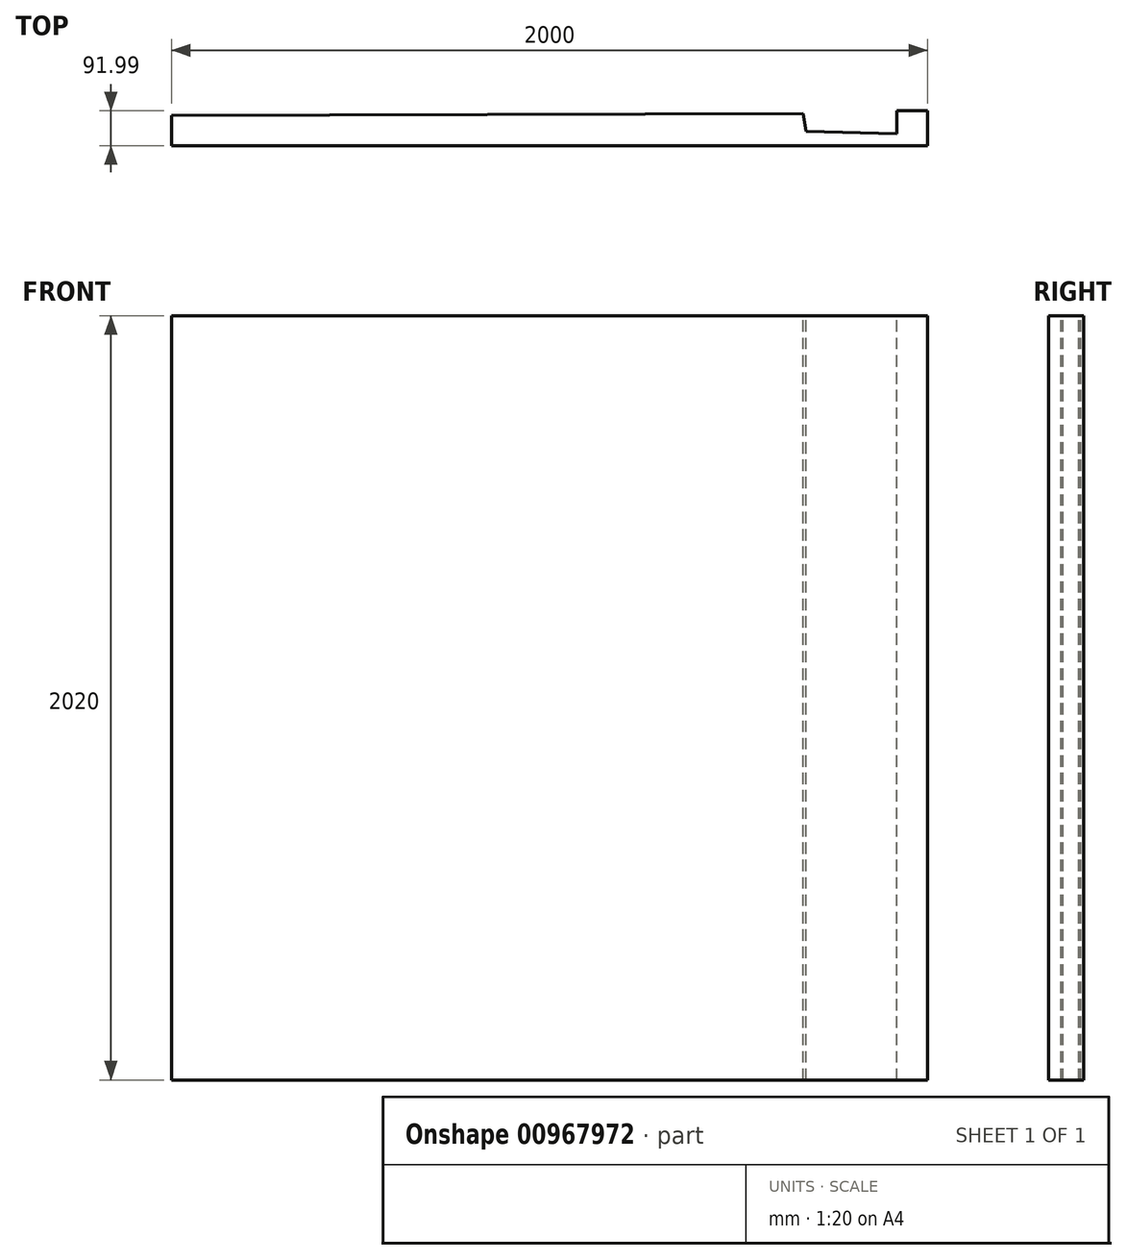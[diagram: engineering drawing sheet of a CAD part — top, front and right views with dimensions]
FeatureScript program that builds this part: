
annotation { "Feature Type Name" : "Feature", "Feature Type Description" : "" }
export const myFeature = defineFeature(function(context is Context, id is Id, definition is map)
    precondition{}
    {
        {
            var Q0;
            Q0=qCreatedBy(makeId("Front.planeOp"),FACE);
            var sketch = newSketch(context, id + "F0", { "sketchPlane" : qUnion([Q0])});
            skLineSegment(sketch, "E0.bottom", {"start": v(-1953.33, 1210) * mm, "end": v(46.67, 1210) * mm});
            skLineSegment(sketch, "E0.top", {"start": v(-1953.33, -810) * mm, "end": v(46.67, -810) * mm});
            skLineSegment(sketch, "E0.left", {"start": v(-1953.33, 1210) * mm, "end": v(-1953.33, -810) * mm});
            skLineSegment(sketch, "E0.right", {"start": v(46.67, 1210) * mm, "end": v(46.67, -810) * mm});
            skLineSegment(sketch, "E1.top", {"start": v(-1953.33, -870) * mm, "end": v(46.67, -870) * mm});
            skLineSegment(sketch, "E1.left", {"start": v(-1953.33, -810) * mm, "end": v(-1953.33, -870) * mm});
            skLineSegment(sketch, "E1.right", {"start": v(46.67, -810) * mm, "end": v(46.67, -870) * mm});
            skLineSegment(sketch, "E2.bottom", {"start": v(46.67, -870) * mm, "end": v(906.67, -870) * mm});
            skLineSegment(sketch, "E2.top", {"start": v(46.67, 1230) * mm, "end": v(906.67, 1230) * mm});
            skLineSegment(sketch, "E2.left", {"start": v(46.67, -870) * mm, "end": v(46.67, 1230) * mm});
            skLineSegment(sketch, "E2.right", {"start": v(906.67, -870) * mm, "end": v(906.67, 1230) * mm});
            skLineSegment(sketch, "E3.bottom", {"start": v(906.67, -870) * mm, "end": v(1451.67, -870) * mm});
            skLineSegment(sketch, "E3.top", {"start": v(906.67, 1210) * mm, "end": v(1451.67, 1210) * mm});
            skLineSegment(sketch, "E3.left", {"start": v(906.67, -870) * mm, "end": v(906.67, 1210) * mm});
            skLineSegment(sketch, "E3.right", {"start": v(1451.67, -870) * mm, "end": v(1451.67, 1210) * mm});
            skLineSegment(sketch, "E4.bottom", {"start": v(1451.67, 1210) * mm, "end": v(2111.67, 1210) * mm});
            skLineSegment(sketch, "E4.top", {"start": v(1451.67, 0) * mm, "end": v(2111.67, 0) * mm});
            skLineSegment(sketch, "E4.left", {"start": v(1451.67, 1210) * mm, "end": v(1451.67, 0) * mm});
            skLineSegment(sketch, "E4.right", {"start": v(2111.67, 1210) * mm, "end": v(2111.67, 0) * mm});
            skLineSegment(sketch, "E5.bottom", {"start": v(2111.67, 0) * mm, "end": v(3431.67, 0) * mm});
            skLineSegment(sketch, "E5.top", {"start": v(2111.67, 1210) * mm, "end": v(3431.67, 1210) * mm});
            skLineSegment(sketch, "E5.left", {"start": v(2111.67, 0) * mm, "end": v(2111.67, 1210) * mm});
            skLineSegment(sketch, "E5.right", {"start": v(3431.67, 0) * mm, "end": v(3431.67, 1210) * mm});
            skLineSegment(sketch, "E6.bottom", {"start": v(3431.67, 0) * mm, "end": v(3871.67, 0) * mm});
            skLineSegment(sketch, "E6.top", {"start": v(3431.67, 1210) * mm, "end": v(3871.67, 1210) * mm});
            skLineSegment(sketch, "E6.right", {"start": v(3871.67, 0) * mm, "end": v(3871.67, 1210) * mm});
            skSolve(sketch);
        }
        {
            var Q0;
            {var subQ0=sQuery(id+"F0.wireOp",EDGE,"E0.bottom");Q0=makeQuery(id+"F0.imprint","IMPRINT",FACE,{"disambiguationData":[TD([[makeQuery(id+"F0.imprint","IMPRINT",EDGE,{"derivedFrom":subQ0}),-1.0]])]});}
            var sketch = newSketch(context, id + "F1", { "sketchPlane" : qUnion([Q0])});
            skLineSegment(sketch, "E7.bottom", {"start": v(-1953.33, 1210) * mm, "end": v(-1799.33, 1210) * mm});
            skLineSegment(sketch, "E7.top", {"start": v(-1953.33, 1056) * mm, "end": v(-1799.33, 1056) * mm});
            skLineSegment(sketch, "E7.left", {"start": v(-1953.33, 1210) * mm, "end": v(-1953.33, 1056) * mm});
            skLineSegment(sketch, "E7.right", {"start": v(-1799.33, 1210) * mm, "end": v(-1799.33, 1056) * mm});
            skLineSegment(sketch, "E8.0.1.0", {"start": v(-1953.33, 1054) * mm, "end": v(-1799.33, 1054) * mm});
            skLineSegment(sketch, "E8.0.1.1", {"start": v(-1799.33, 1054) * mm, "end": v(-1799.33, 900) * mm});
            skLineSegment(sketch, "E8.0.1.2", {"start": v(-1953.33, 900) * mm, "end": v(-1799.33, 900) * mm});
            skLineSegment(sketch, "E8.0.1.3", {"start": v(-1953.33, 1054) * mm, "end": v(-1953.33, 900) * mm});
            skLineSegment(sketch, "E8.0.2.0", {"start": v(-1953.33, 898) * mm, "end": v(-1799.33, 898) * mm});
            skLineSegment(sketch, "E8.0.2.1", {"start": v(-1799.33, 898) * mm, "end": v(-1799.33, 744) * mm});
            skLineSegment(sketch, "E8.0.2.2", {"start": v(-1953.33, 744) * mm, "end": v(-1799.33, 744) * mm});
            skLineSegment(sketch, "E8.0.2.3", {"start": v(-1953.33, 898) * mm, "end": v(-1953.33, 744) * mm});
            skLineSegment(sketch, "E8.0.3.0", {"start": v(-1953.33, 742) * mm, "end": v(-1799.33, 742) * mm});
            skLineSegment(sketch, "E8.0.3.1", {"start": v(-1799.33, 742) * mm, "end": v(-1799.33, 588) * mm});
            skLineSegment(sketch, "E8.0.3.2", {"start": v(-1953.33, 588) * mm, "end": v(-1799.33, 588) * mm});
            skLineSegment(sketch, "E8.0.3.3", {"start": v(-1953.33, 742) * mm, "end": v(-1953.33, 588) * mm});
            skLineSegment(sketch, "E8.0.4.0", {"start": v(-1953.33, 586) * mm, "end": v(-1799.33, 586) * mm});
            skLineSegment(sketch, "E8.0.4.1", {"start": v(-1799.33, 586) * mm, "end": v(-1799.33, 432) * mm});
            skLineSegment(sketch, "E8.0.4.2", {"start": v(-1953.33, 432) * mm, "end": v(-1799.33, 432) * mm});
            skLineSegment(sketch, "E8.0.4.3", {"start": v(-1953.33, 586) * mm, "end": v(-1953.33, 432) * mm});
            skLineSegment(sketch, "E8.0.5.0", {"start": v(-1953.33, 430) * mm, "end": v(-1799.33, 430) * mm});
            skLineSegment(sketch, "E8.0.5.1", {"start": v(-1799.33, 430) * mm, "end": v(-1799.33, 276) * mm});
            skLineSegment(sketch, "E8.0.5.2", {"start": v(-1953.33, 276) * mm, "end": v(-1799.33, 276) * mm});
            skLineSegment(sketch, "E8.0.5.3", {"start": v(-1953.33, 430) * mm, "end": v(-1953.33, 276) * mm});
            skLineSegment(sketch, "E8.0.6.0", {"start": v(-1953.33, 274) * mm, "end": v(-1799.33, 274) * mm});
            skLineSegment(sketch, "E8.0.6.1", {"start": v(-1799.33, 274) * mm, "end": v(-1799.33, 120) * mm});
            skLineSegment(sketch, "E8.0.6.2", {"start": v(-1953.33, 120) * mm, "end": v(-1799.33, 120) * mm});
            skLineSegment(sketch, "E8.0.6.3", {"start": v(-1953.33, 274) * mm, "end": v(-1953.33, 120) * mm});
            skLineSegment(sketch, "E8.0.7.0", {"start": v(-1953.33, 118) * mm, "end": v(-1799.33, 118) * mm});
            skLineSegment(sketch, "E8.0.7.1", {"start": v(-1799.33, 118) * mm, "end": v(-1799.33, -36) * mm});
            skLineSegment(sketch, "E8.0.7.2", {"start": v(-1953.33, -36) * mm, "end": v(-1799.33, -36) * mm});
            skLineSegment(sketch, "E8.0.7.3", {"start": v(-1953.33, 118) * mm, "end": v(-1953.33, -36) * mm});
            skLineSegment(sketch, "E8.0.8.0", {"start": v(-1953.33, -38) * mm, "end": v(-1799.33, -38) * mm});
            skLineSegment(sketch, "E8.0.8.1", {"start": v(-1799.33, -38) * mm, "end": v(-1799.33, -192) * mm});
            skLineSegment(sketch, "E8.0.8.2", {"start": v(-1953.33, -192) * mm, "end": v(-1799.33, -192) * mm});
            skLineSegment(sketch, "E8.0.8.3", {"start": v(-1953.33, -38) * mm, "end": v(-1953.33, -192) * mm});
            skLineSegment(sketch, "E8.0.9.0", {"start": v(-1953.33, -194) * mm, "end": v(-1799.33, -194) * mm});
            skLineSegment(sketch, "E8.0.9.1", {"start": v(-1799.33, -194) * mm, "end": v(-1799.33, -348) * mm});
            skLineSegment(sketch, "E8.0.9.2", {"start": v(-1953.33, -348) * mm, "end": v(-1799.33, -348) * mm});
            skLineSegment(sketch, "E8.0.9.3", {"start": v(-1953.33, -194) * mm, "end": v(-1953.33, -348) * mm});
            skLineSegment(sketch, "E8.0.10.0", {"start": v(-1953.33, -350) * mm, "end": v(-1799.33, -350) * mm});
            skLineSegment(sketch, "E8.0.10.1", {"start": v(-1799.33, -350) * mm, "end": v(-1799.33, -504) * mm});
            skLineSegment(sketch, "E8.0.10.2", {"start": v(-1953.33, -504) * mm, "end": v(-1799.33, -504) * mm});
            skLineSegment(sketch, "E8.0.10.3", {"start": v(-1953.33, -350) * mm, "end": v(-1953.33, -504) * mm});
            skLineSegment(sketch, "E8.0.11.0", {"start": v(-1953.33, -506) * mm, "end": v(-1799.33, -506) * mm});
            skLineSegment(sketch, "E8.0.11.1", {"start": v(-1799.33, -506) * mm, "end": v(-1799.33, -660) * mm});
            skLineSegment(sketch, "E8.0.11.2", {"start": v(-1953.33, -660) * mm, "end": v(-1799.33, -660) * mm});
            skLineSegment(sketch, "E8.0.11.3", {"start": v(-1953.33, -506) * mm, "end": v(-1953.33, -660) * mm});
            skLineSegment(sketch, "E8.0.12.0", {"start": v(-1953.33, -662) * mm, "end": v(-1799.33, -662) * mm});
            skLineSegment(sketch, "E8.0.12.1", {"start": v(-1799.33, -662) * mm, "end": v(-1799.33, -816) * mm});
            skLineSegment(sketch, "E8.0.12.2", {"start": v(-1953.33, -816) * mm, "end": v(-1799.33, -816) * mm});
            skLineSegment(sketch, "E8.0.12.3", {"start": v(-1953.33, -662) * mm, "end": v(-1953.33, -816) * mm});
            skLineSegment(sketch, "E8.1.0.0", {"start": v(-1797.33, 1210) * mm, "end": v(-1643.33, 1210) * mm});
            skLineSegment(sketch, "E8.1.0.1", {"start": v(-1643.33, 1210) * mm, "end": v(-1643.33, 1056) * mm});
            skLineSegment(sketch, "E8.1.0.2", {"start": v(-1797.33, 1056) * mm, "end": v(-1643.33, 1056) * mm});
            skLineSegment(sketch, "E8.1.0.3", {"start": v(-1797.33, 1210) * mm, "end": v(-1797.33, 1056) * mm});
            skLineSegment(sketch, "E8.1.1.0", {"start": v(-1797.33, 1054) * mm, "end": v(-1643.33, 1054) * mm});
            skLineSegment(sketch, "E8.1.1.1", {"start": v(-1643.33, 1054) * mm, "end": v(-1643.33, 900) * mm});
            skLineSegment(sketch, "E8.1.1.2", {"start": v(-1797.33, 900) * mm, "end": v(-1643.33, 900) * mm});
            skLineSegment(sketch, "E8.1.1.3", {"start": v(-1797.33, 1054) * mm, "end": v(-1797.33, 900) * mm});
            skLineSegment(sketch, "E8.1.2.0", {"start": v(-1797.33, 898) * mm, "end": v(-1643.33, 898) * mm});
            skLineSegment(sketch, "E8.1.2.1", {"start": v(-1643.33, 898) * mm, "end": v(-1643.33, 744) * mm});
            skLineSegment(sketch, "E8.1.2.2", {"start": v(-1797.33, 744) * mm, "end": v(-1643.33, 744) * mm});
            skLineSegment(sketch, "E8.1.2.3", {"start": v(-1797.33, 898) * mm, "end": v(-1797.33, 744) * mm});
            skLineSegment(sketch, "E8.1.3.0", {"start": v(-1797.33, 742) * mm, "end": v(-1643.33, 742) * mm});
            skLineSegment(sketch, "E8.1.3.1", {"start": v(-1643.33, 742) * mm, "end": v(-1643.33, 588) * mm});
            skLineSegment(sketch, "E8.1.3.2", {"start": v(-1797.33, 588) * mm, "end": v(-1643.33, 588) * mm});
            skLineSegment(sketch, "E8.1.3.3", {"start": v(-1797.33, 742) * mm, "end": v(-1797.33, 588) * mm});
            skLineSegment(sketch, "E8.1.4.0", {"start": v(-1797.33, 586) * mm, "end": v(-1643.33, 586) * mm});
            skLineSegment(sketch, "E8.1.4.1", {"start": v(-1643.33, 586) * mm, "end": v(-1643.33, 432) * mm});
            skLineSegment(sketch, "E8.1.4.2", {"start": v(-1797.33, 432) * mm, "end": v(-1643.33, 432) * mm});
            skLineSegment(sketch, "E8.1.4.3", {"start": v(-1797.33, 586) * mm, "end": v(-1797.33, 432) * mm});
            skLineSegment(sketch, "E8.1.5.0", {"start": v(-1797.33, 430) * mm, "end": v(-1643.33, 430) * mm});
            skLineSegment(sketch, "E8.1.5.1", {"start": v(-1643.33, 430) * mm, "end": v(-1643.33, 276) * mm});
            skLineSegment(sketch, "E8.1.5.2", {"start": v(-1797.33, 276) * mm, "end": v(-1643.33, 276) * mm});
            skLineSegment(sketch, "E8.1.5.3", {"start": v(-1797.33, 430) * mm, "end": v(-1797.33, 276) * mm});
            skLineSegment(sketch, "E8.1.6.0", {"start": v(-1797.33, 274) * mm, "end": v(-1643.33, 274) * mm});
            skLineSegment(sketch, "E8.1.6.1", {"start": v(-1643.33, 274) * mm, "end": v(-1643.33, 120) * mm});
            skLineSegment(sketch, "E8.1.6.2", {"start": v(-1797.33, 120) * mm, "end": v(-1643.33, 120) * mm});
            skLineSegment(sketch, "E8.1.6.3", {"start": v(-1797.33, 274) * mm, "end": v(-1797.33, 120) * mm});
            skLineSegment(sketch, "E8.1.7.0", {"start": v(-1797.33, 118) * mm, "end": v(-1643.33, 118) * mm});
            skLineSegment(sketch, "E8.1.7.1", {"start": v(-1643.33, 118) * mm, "end": v(-1643.33, -36) * mm});
            skLineSegment(sketch, "E8.1.7.2", {"start": v(-1797.33, -36) * mm, "end": v(-1643.33, -36) * mm});
            skLineSegment(sketch, "E8.1.7.3", {"start": v(-1797.33, 118) * mm, "end": v(-1797.33, -36) * mm});
            skLineSegment(sketch, "E8.1.8.0", {"start": v(-1797.33, -38) * mm, "end": v(-1643.33, -38) * mm});
            skLineSegment(sketch, "E8.1.8.1", {"start": v(-1643.33, -38) * mm, "end": v(-1643.33, -192) * mm});
            skLineSegment(sketch, "E8.1.8.2", {"start": v(-1797.33, -192) * mm, "end": v(-1643.33, -192) * mm});
            skLineSegment(sketch, "E8.1.8.3", {"start": v(-1797.33, -38) * mm, "end": v(-1797.33, -192) * mm});
            skLineSegment(sketch, "E8.1.9.0", {"start": v(-1797.33, -194) * mm, "end": v(-1643.33, -194) * mm});
            skLineSegment(sketch, "E8.1.9.1", {"start": v(-1643.33, -194) * mm, "end": v(-1643.33, -348) * mm});
            skLineSegment(sketch, "E8.1.9.2", {"start": v(-1797.33, -348) * mm, "end": v(-1643.33, -348) * mm});
            skLineSegment(sketch, "E8.1.9.3", {"start": v(-1797.33, -194) * mm, "end": v(-1797.33, -348) * mm});
            skLineSegment(sketch, "E8.1.10.0", {"start": v(-1797.33, -350) * mm, "end": v(-1643.33, -350) * mm});
            skLineSegment(sketch, "E8.1.10.1", {"start": v(-1643.33, -350) * mm, "end": v(-1643.33, -504) * mm});
            skLineSegment(sketch, "E8.1.10.2", {"start": v(-1797.33, -504) * mm, "end": v(-1643.33, -504) * mm});
            skLineSegment(sketch, "E8.1.10.3", {"start": v(-1797.33, -350) * mm, "end": v(-1797.33, -504) * mm});
            skLineSegment(sketch, "E8.1.11.0", {"start": v(-1797.33, -506) * mm, "end": v(-1643.33, -506) * mm});
            skLineSegment(sketch, "E8.1.11.1", {"start": v(-1643.33, -506) * mm, "end": v(-1643.33, -660) * mm});
            skLineSegment(sketch, "E8.1.11.2", {"start": v(-1797.33, -660) * mm, "end": v(-1643.33, -660) * mm});
            skLineSegment(sketch, "E8.1.11.3", {"start": v(-1797.33, -506) * mm, "end": v(-1797.33, -660) * mm});
            skLineSegment(sketch, "E8.1.12.0", {"start": v(-1797.33, -662) * mm, "end": v(-1643.33, -662) * mm});
            skLineSegment(sketch, "E8.1.12.1", {"start": v(-1643.33, -662) * mm, "end": v(-1643.33, -816) * mm});
            skLineSegment(sketch, "E8.1.12.2", {"start": v(-1797.33, -816) * mm, "end": v(-1643.33, -816) * mm});
            skLineSegment(sketch, "E8.1.12.3", {"start": v(-1797.33, -662) * mm, "end": v(-1797.33, -816) * mm});
            skLineSegment(sketch, "E8.2.0.0", {"start": v(-1641.33, 1210) * mm, "end": v(-1487.33, 1210) * mm});
            skLineSegment(sketch, "E8.2.0.1", {"start": v(-1487.33, 1210) * mm, "end": v(-1487.33, 1056) * mm});
            skLineSegment(sketch, "E8.2.0.2", {"start": v(-1641.33, 1056) * mm, "end": v(-1487.33, 1056) * mm});
            skLineSegment(sketch, "E8.2.0.3", {"start": v(-1641.33, 1210) * mm, "end": v(-1641.33, 1056) * mm});
            skLineSegment(sketch, "E8.2.1.0", {"start": v(-1641.33, 1054) * mm, "end": v(-1487.33, 1054) * mm});
            skLineSegment(sketch, "E8.2.1.1", {"start": v(-1487.33, 1054) * mm, "end": v(-1487.33, 900) * mm});
            skLineSegment(sketch, "E8.2.1.2", {"start": v(-1641.33, 900) * mm, "end": v(-1487.33, 900) * mm});
            skLineSegment(sketch, "E8.2.1.3", {"start": v(-1641.33, 1054) * mm, "end": v(-1641.33, 900) * mm});
            skLineSegment(sketch, "E8.2.2.0", {"start": v(-1641.33, 898) * mm, "end": v(-1487.33, 898) * mm});
            skLineSegment(sketch, "E8.2.2.1", {"start": v(-1487.33, 898) * mm, "end": v(-1487.33, 744) * mm});
            skLineSegment(sketch, "E8.2.2.2", {"start": v(-1641.33, 744) * mm, "end": v(-1487.33, 744) * mm});
            skLineSegment(sketch, "E8.2.2.3", {"start": v(-1641.33, 898) * mm, "end": v(-1641.33, 744) * mm});
            skLineSegment(sketch, "E8.2.3.0", {"start": v(-1641.33, 742) * mm, "end": v(-1487.33, 742) * mm});
            skLineSegment(sketch, "E8.2.3.1", {"start": v(-1487.33, 742) * mm, "end": v(-1487.33, 588) * mm});
            skLineSegment(sketch, "E8.2.3.2", {"start": v(-1641.33, 588) * mm, "end": v(-1487.33, 588) * mm});
            skLineSegment(sketch, "E8.2.3.3", {"start": v(-1641.33, 742) * mm, "end": v(-1641.33, 588) * mm});
            skLineSegment(sketch, "E8.2.4.0", {"start": v(-1641.33, 586) * mm, "end": v(-1487.33, 586) * mm});
            skLineSegment(sketch, "E8.2.4.1", {"start": v(-1487.33, 586) * mm, "end": v(-1487.33, 432) * mm});
            skLineSegment(sketch, "E8.2.4.2", {"start": v(-1641.33, 432) * mm, "end": v(-1487.33, 432) * mm});
            skLineSegment(sketch, "E8.2.4.3", {"start": v(-1641.33, 586) * mm, "end": v(-1641.33, 432) * mm});
            skLineSegment(sketch, "E8.2.5.0", {"start": v(-1641.33, 430) * mm, "end": v(-1487.33, 430) * mm});
            skLineSegment(sketch, "E8.2.5.1", {"start": v(-1487.33, 430) * mm, "end": v(-1487.33, 276) * mm});
            skLineSegment(sketch, "E8.2.5.2", {"start": v(-1641.33, 276) * mm, "end": v(-1487.33, 276) * mm});
            skLineSegment(sketch, "E8.2.5.3", {"start": v(-1641.33, 430) * mm, "end": v(-1641.33, 276) * mm});
            skLineSegment(sketch, "E8.2.6.0", {"start": v(-1641.33, 274) * mm, "end": v(-1487.33, 274) * mm});
            skLineSegment(sketch, "E8.2.6.1", {"start": v(-1487.33, 274) * mm, "end": v(-1487.33, 120) * mm});
            skLineSegment(sketch, "E8.2.6.2", {"start": v(-1641.33, 120) * mm, "end": v(-1487.33, 120) * mm});
            skLineSegment(sketch, "E8.2.6.3", {"start": v(-1641.33, 274) * mm, "end": v(-1641.33, 120) * mm});
            skLineSegment(sketch, "E8.2.7.0", {"start": v(-1641.33, 118) * mm, "end": v(-1487.33, 118) * mm});
            skLineSegment(sketch, "E8.2.7.1", {"start": v(-1487.33, 118) * mm, "end": v(-1487.33, -36) * mm});
            skLineSegment(sketch, "E8.2.7.2", {"start": v(-1641.33, -36) * mm, "end": v(-1487.33, -36) * mm});
            skLineSegment(sketch, "E8.2.7.3", {"start": v(-1641.33, 118) * mm, "end": v(-1641.33, -36) * mm});
            skLineSegment(sketch, "E8.2.8.0", {"start": v(-1641.33, -38) * mm, "end": v(-1487.33, -38) * mm});
            skLineSegment(sketch, "E8.2.8.1", {"start": v(-1487.33, -38) * mm, "end": v(-1487.33, -192) * mm});
            skLineSegment(sketch, "E8.2.8.2", {"start": v(-1641.33, -192) * mm, "end": v(-1487.33, -192) * mm});
            skLineSegment(sketch, "E8.2.8.3", {"start": v(-1641.33, -38) * mm, "end": v(-1641.33, -192) * mm});
            skLineSegment(sketch, "E8.2.9.0", {"start": v(-1641.33, -194) * mm, "end": v(-1487.33, -194) * mm});
            skLineSegment(sketch, "E8.2.9.1", {"start": v(-1487.33, -194) * mm, "end": v(-1487.33, -348) * mm});
            skLineSegment(sketch, "E8.2.9.2", {"start": v(-1641.33, -348) * mm, "end": v(-1487.33, -348) * mm});
            skLineSegment(sketch, "E8.2.9.3", {"start": v(-1641.33, -194) * mm, "end": v(-1641.33, -348) * mm});
            skLineSegment(sketch, "E8.2.10.0", {"start": v(-1641.33, -350) * mm, "end": v(-1487.33, -350) * mm});
            skLineSegment(sketch, "E8.2.10.1", {"start": v(-1487.33, -350) * mm, "end": v(-1487.33, -504) * mm});
            skLineSegment(sketch, "E8.2.10.2", {"start": v(-1641.33, -504) * mm, "end": v(-1487.33, -504) * mm});
            skLineSegment(sketch, "E8.2.10.3", {"start": v(-1641.33, -350) * mm, "end": v(-1641.33, -504) * mm});
            skLineSegment(sketch, "E8.2.11.0", {"start": v(-1641.33, -506) * mm, "end": v(-1487.33, -506) * mm});
            skLineSegment(sketch, "E8.2.11.1", {"start": v(-1487.33, -506) * mm, "end": v(-1487.33, -660) * mm});
            skLineSegment(sketch, "E8.2.11.2", {"start": v(-1641.33, -660) * mm, "end": v(-1487.33, -660) * mm});
            skLineSegment(sketch, "E8.2.11.3", {"start": v(-1641.33, -506) * mm, "end": v(-1641.33, -660) * mm});
            skLineSegment(sketch, "E8.2.12.0", {"start": v(-1641.33, -662) * mm, "end": v(-1487.33, -662) * mm});
            skLineSegment(sketch, "E8.2.12.1", {"start": v(-1487.33, -662) * mm, "end": v(-1487.33, -816) * mm});
            skLineSegment(sketch, "E8.2.12.2", {"start": v(-1641.33, -816) * mm, "end": v(-1487.33, -816) * mm});
            skLineSegment(sketch, "E8.2.12.3", {"start": v(-1641.33, -662) * mm, "end": v(-1641.33, -816) * mm});
            skLineSegment(sketch, "E8.3.0.0", {"start": v(-1485.33, 1210) * mm, "end": v(-1331.33, 1210) * mm});
            skLineSegment(sketch, "E8.3.0.1", {"start": v(-1331.33, 1210) * mm, "end": v(-1331.33, 1056) * mm});
            skLineSegment(sketch, "E8.3.0.2", {"start": v(-1485.33, 1056) * mm, "end": v(-1331.33, 1056) * mm});
            skLineSegment(sketch, "E8.3.0.3", {"start": v(-1485.33, 1210) * mm, "end": v(-1485.33, 1056) * mm});
            skLineSegment(sketch, "E8.3.1.0", {"start": v(-1485.33, 1054) * mm, "end": v(-1331.33, 1054) * mm});
            skLineSegment(sketch, "E8.3.1.1", {"start": v(-1331.33, 1054) * mm, "end": v(-1331.33, 900) * mm});
            skLineSegment(sketch, "E8.3.1.2", {"start": v(-1485.33, 900) * mm, "end": v(-1331.33, 900) * mm});
            skLineSegment(sketch, "E8.3.1.3", {"start": v(-1485.33, 1054) * mm, "end": v(-1485.33, 900) * mm});
            skLineSegment(sketch, "E8.3.2.0", {"start": v(-1485.33, 898) * mm, "end": v(-1331.33, 898) * mm});
            skLineSegment(sketch, "E8.3.2.1", {"start": v(-1331.33, 898) * mm, "end": v(-1331.33, 744) * mm});
            skLineSegment(sketch, "E8.3.2.2", {"start": v(-1485.33, 744) * mm, "end": v(-1331.33, 744) * mm});
            skLineSegment(sketch, "E8.3.2.3", {"start": v(-1485.33, 898) * mm, "end": v(-1485.33, 744) * mm});
            skLineSegment(sketch, "E8.3.3.0", {"start": v(-1485.33, 742) * mm, "end": v(-1331.33, 742) * mm});
            skLineSegment(sketch, "E8.3.3.1", {"start": v(-1331.33, 742) * mm, "end": v(-1331.33, 588) * mm});
            skLineSegment(sketch, "E8.3.3.2", {"start": v(-1485.33, 588) * mm, "end": v(-1331.33, 588) * mm});
            skLineSegment(sketch, "E8.3.3.3", {"start": v(-1485.33, 742) * mm, "end": v(-1485.33, 588) * mm});
            skLineSegment(sketch, "E8.3.4.0", {"start": v(-1485.33, 586) * mm, "end": v(-1331.33, 586) * mm});
            skLineSegment(sketch, "E8.3.4.1", {"start": v(-1331.33, 586) * mm, "end": v(-1331.33, 432) * mm});
            skLineSegment(sketch, "E8.3.4.2", {"start": v(-1485.33, 432) * mm, "end": v(-1331.33, 432) * mm});
            skLineSegment(sketch, "E8.3.4.3", {"start": v(-1485.33, 586) * mm, "end": v(-1485.33, 432) * mm});
            skLineSegment(sketch, "E8.3.5.0", {"start": v(-1485.33, 430) * mm, "end": v(-1331.33, 430) * mm});
            skLineSegment(sketch, "E8.3.5.1", {"start": v(-1331.33, 430) * mm, "end": v(-1331.33, 276) * mm});
            skLineSegment(sketch, "E8.3.5.2", {"start": v(-1485.33, 276) * mm, "end": v(-1331.33, 276) * mm});
            skLineSegment(sketch, "E8.3.5.3", {"start": v(-1485.33, 430) * mm, "end": v(-1485.33, 276) * mm});
            skLineSegment(sketch, "E8.3.6.0", {"start": v(-1485.33, 274) * mm, "end": v(-1331.33, 274) * mm});
            skLineSegment(sketch, "E8.3.6.1", {"start": v(-1331.33, 274) * mm, "end": v(-1331.33, 120) * mm});
            skLineSegment(sketch, "E8.3.6.2", {"start": v(-1485.33, 120) * mm, "end": v(-1331.33, 120) * mm});
            skLineSegment(sketch, "E8.3.6.3", {"start": v(-1485.33, 274) * mm, "end": v(-1485.33, 120) * mm});
            skLineSegment(sketch, "E8.3.7.0", {"start": v(-1485.33, 118) * mm, "end": v(-1331.33, 118) * mm});
            skLineSegment(sketch, "E8.3.7.1", {"start": v(-1331.33, 118) * mm, "end": v(-1331.33, -36) * mm});
            skLineSegment(sketch, "E8.3.7.2", {"start": v(-1485.33, -36) * mm, "end": v(-1331.33, -36) * mm});
            skLineSegment(sketch, "E8.3.7.3", {"start": v(-1485.33, 118) * mm, "end": v(-1485.33, -36) * mm});
            skLineSegment(sketch, "E8.3.8.0", {"start": v(-1485.33, -38) * mm, "end": v(-1331.33, -38) * mm});
            skLineSegment(sketch, "E8.3.8.1", {"start": v(-1331.33, -38) * mm, "end": v(-1331.33, -192) * mm});
            skLineSegment(sketch, "E8.3.8.2", {"start": v(-1485.33, -192) * mm, "end": v(-1331.33, -192) * mm});
            skLineSegment(sketch, "E8.3.8.3", {"start": v(-1485.33, -38) * mm, "end": v(-1485.33, -192) * mm});
            skLineSegment(sketch, "E8.3.9.0", {"start": v(-1485.33, -194) * mm, "end": v(-1331.33, -194) * mm});
            skLineSegment(sketch, "E8.3.9.1", {"start": v(-1331.33, -194) * mm, "end": v(-1331.33, -348) * mm});
            skLineSegment(sketch, "E8.3.9.2", {"start": v(-1485.33, -348) * mm, "end": v(-1331.33, -348) * mm});
            skLineSegment(sketch, "E8.3.9.3", {"start": v(-1485.33, -194) * mm, "end": v(-1485.33, -348) * mm});
            skLineSegment(sketch, "E8.3.10.0", {"start": v(-1485.33, -350) * mm, "end": v(-1331.33, -350) * mm});
            skLineSegment(sketch, "E8.3.10.1", {"start": v(-1331.33, -350) * mm, "end": v(-1331.33, -504) * mm});
            skLineSegment(sketch, "E8.3.10.2", {"start": v(-1485.33, -504) * mm, "end": v(-1331.33, -504) * mm});
            skLineSegment(sketch, "E8.3.10.3", {"start": v(-1485.33, -350) * mm, "end": v(-1485.33, -504) * mm});
            skLineSegment(sketch, "E8.3.11.0", {"start": v(-1485.33, -506) * mm, "end": v(-1331.33, -506) * mm});
            skLineSegment(sketch, "E8.3.11.1", {"start": v(-1331.33, -506) * mm, "end": v(-1331.33, -660) * mm});
            skLineSegment(sketch, "E8.3.11.2", {"start": v(-1485.33, -660) * mm, "end": v(-1331.33, -660) * mm});
            skLineSegment(sketch, "E8.3.11.3", {"start": v(-1485.33, -506) * mm, "end": v(-1485.33, -660) * mm});
            skLineSegment(sketch, "E8.3.12.0", {"start": v(-1485.33, -662) * mm, "end": v(-1331.33, -662) * mm});
            skLineSegment(sketch, "E8.3.12.1", {"start": v(-1331.33, -662) * mm, "end": v(-1331.33, -816) * mm});
            skLineSegment(sketch, "E8.3.12.2", {"start": v(-1485.33, -816) * mm, "end": v(-1331.33, -816) * mm});
            skLineSegment(sketch, "E8.3.12.3", {"start": v(-1485.33, -662) * mm, "end": v(-1485.33, -816) * mm});
            skLineSegment(sketch, "E8.4.0.0", {"start": v(-1329.33, 1210) * mm, "end": v(-1175.33, 1210) * mm});
            skLineSegment(sketch, "E8.4.0.1", {"start": v(-1175.33, 1210) * mm, "end": v(-1175.33, 1056) * mm});
            skLineSegment(sketch, "E8.4.0.2", {"start": v(-1329.33, 1056) * mm, "end": v(-1175.33, 1056) * mm});
            skLineSegment(sketch, "E8.4.0.3", {"start": v(-1329.33, 1210) * mm, "end": v(-1329.33, 1056) * mm});
            skLineSegment(sketch, "E8.4.1.0", {"start": v(-1329.33, 1054) * mm, "end": v(-1175.33, 1054) * mm});
            skLineSegment(sketch, "E8.4.1.1", {"start": v(-1175.33, 1054) * mm, "end": v(-1175.33, 900) * mm});
            skLineSegment(sketch, "E8.4.1.2", {"start": v(-1329.33, 900) * mm, "end": v(-1175.33, 900) * mm});
            skLineSegment(sketch, "E8.4.1.3", {"start": v(-1329.33, 1054) * mm, "end": v(-1329.33, 900) * mm});
            skLineSegment(sketch, "E8.4.2.0", {"start": v(-1329.33, 898) * mm, "end": v(-1175.33, 898) * mm});
            skLineSegment(sketch, "E8.4.2.1", {"start": v(-1175.33, 898) * mm, "end": v(-1175.33, 744) * mm});
            skLineSegment(sketch, "E8.4.2.2", {"start": v(-1329.33, 744) * mm, "end": v(-1175.33, 744) * mm});
            skLineSegment(sketch, "E8.4.2.3", {"start": v(-1329.33, 898) * mm, "end": v(-1329.33, 744) * mm});
            skLineSegment(sketch, "E8.4.3.0", {"start": v(-1329.33, 742) * mm, "end": v(-1175.33, 742) * mm});
            skLineSegment(sketch, "E8.4.3.1", {"start": v(-1175.33, 742) * mm, "end": v(-1175.33, 588) * mm});
            skLineSegment(sketch, "E8.4.3.2", {"start": v(-1329.33, 588) * mm, "end": v(-1175.33, 588) * mm});
            skLineSegment(sketch, "E8.4.3.3", {"start": v(-1329.33, 742) * mm, "end": v(-1329.33, 588) * mm});
            skLineSegment(sketch, "E8.4.4.0", {"start": v(-1329.33, 586) * mm, "end": v(-1175.33, 586) * mm});
            skLineSegment(sketch, "E8.4.4.1", {"start": v(-1175.33, 586) * mm, "end": v(-1175.33, 432) * mm});
            skLineSegment(sketch, "E8.4.4.2", {"start": v(-1329.33, 432) * mm, "end": v(-1175.33, 432) * mm});
            skLineSegment(sketch, "E8.4.4.3", {"start": v(-1329.33, 586) * mm, "end": v(-1329.33, 432) * mm});
            skLineSegment(sketch, "E8.4.5.0", {"start": v(-1329.33, 430) * mm, "end": v(-1175.33, 430) * mm});
            skLineSegment(sketch, "E8.4.5.1", {"start": v(-1175.33, 430) * mm, "end": v(-1175.33, 276) * mm});
            skLineSegment(sketch, "E8.4.5.2", {"start": v(-1329.33, 276) * mm, "end": v(-1175.33, 276) * mm});
            skLineSegment(sketch, "E8.4.5.3", {"start": v(-1329.33, 430) * mm, "end": v(-1329.33, 276) * mm});
            skLineSegment(sketch, "E8.4.6.0", {"start": v(-1329.33, 274) * mm, "end": v(-1175.33, 274) * mm});
            skLineSegment(sketch, "E8.4.6.1", {"start": v(-1175.33, 274) * mm, "end": v(-1175.33, 120) * mm});
            skLineSegment(sketch, "E8.4.6.2", {"start": v(-1329.33, 120) * mm, "end": v(-1175.33, 120) * mm});
            skLineSegment(sketch, "E8.4.6.3", {"start": v(-1329.33, 274) * mm, "end": v(-1329.33, 120) * mm});
            skLineSegment(sketch, "E8.4.7.0", {"start": v(-1329.33, 118) * mm, "end": v(-1175.33, 118) * mm});
            skLineSegment(sketch, "E8.4.7.1", {"start": v(-1175.33, 118) * mm, "end": v(-1175.33, -36) * mm});
            skLineSegment(sketch, "E8.4.7.2", {"start": v(-1329.33, -36) * mm, "end": v(-1175.33, -36) * mm});
            skLineSegment(sketch, "E8.4.7.3", {"start": v(-1329.33, 118) * mm, "end": v(-1329.33, -36) * mm});
            skLineSegment(sketch, "E8.4.8.0", {"start": v(-1329.33, -38) * mm, "end": v(-1175.33, -38) * mm});
            skLineSegment(sketch, "E8.4.8.1", {"start": v(-1175.33, -38) * mm, "end": v(-1175.33, -192) * mm});
            skLineSegment(sketch, "E8.4.8.2", {"start": v(-1329.33, -192) * mm, "end": v(-1175.33, -192) * mm});
            skLineSegment(sketch, "E8.4.8.3", {"start": v(-1329.33, -38) * mm, "end": v(-1329.33, -192) * mm});
            skLineSegment(sketch, "E8.4.9.0", {"start": v(-1329.33, -194) * mm, "end": v(-1175.33, -194) * mm});
            skLineSegment(sketch, "E8.4.9.1", {"start": v(-1175.33, -194) * mm, "end": v(-1175.33, -348) * mm});
            skLineSegment(sketch, "E8.4.9.2", {"start": v(-1329.33, -348) * mm, "end": v(-1175.33, -348) * mm});
            skLineSegment(sketch, "E8.4.9.3", {"start": v(-1329.33, -194) * mm, "end": v(-1329.33, -348) * mm});
            skLineSegment(sketch, "E8.4.10.0", {"start": v(-1329.33, -350) * mm, "end": v(-1175.33, -350) * mm});
            skLineSegment(sketch, "E8.4.10.1", {"start": v(-1175.33, -350) * mm, "end": v(-1175.33, -504) * mm});
            skLineSegment(sketch, "E8.4.10.2", {"start": v(-1329.33, -504) * mm, "end": v(-1175.33, -504) * mm});
            skLineSegment(sketch, "E8.4.10.3", {"start": v(-1329.33, -350) * mm, "end": v(-1329.33, -504) * mm});
            skLineSegment(sketch, "E8.4.11.0", {"start": v(-1329.33, -506) * mm, "end": v(-1175.33, -506) * mm});
            skLineSegment(sketch, "E8.4.11.1", {"start": v(-1175.33, -506) * mm, "end": v(-1175.33, -660) * mm});
            skLineSegment(sketch, "E8.4.11.2", {"start": v(-1329.33, -660) * mm, "end": v(-1175.33, -660) * mm});
            skLineSegment(sketch, "E8.4.11.3", {"start": v(-1329.33, -506) * mm, "end": v(-1329.33, -660) * mm});
            skLineSegment(sketch, "E8.4.12.0", {"start": v(-1329.33, -662) * mm, "end": v(-1175.33, -662) * mm});
            skLineSegment(sketch, "E8.4.12.1", {"start": v(-1175.33, -662) * mm, "end": v(-1175.33, -816) * mm});
            skLineSegment(sketch, "E8.4.12.2", {"start": v(-1329.33, -816) * mm, "end": v(-1175.33, -816) * mm});
            skLineSegment(sketch, "E8.4.12.3", {"start": v(-1329.33, -662) * mm, "end": v(-1329.33, -816) * mm});
            skLineSegment(sketch, "E8.5.0.0", {"start": v(-1173.33, 1210) * mm, "end": v(-1019.33, 1210) * mm});
            skLineSegment(sketch, "E8.5.0.1", {"start": v(-1019.33, 1210) * mm, "end": v(-1019.33, 1056) * mm});
            skLineSegment(sketch, "E8.5.0.2", {"start": v(-1173.33, 1056) * mm, "end": v(-1019.33, 1056) * mm});
            skLineSegment(sketch, "E8.5.0.3", {"start": v(-1173.33, 1210) * mm, "end": v(-1173.33, 1056) * mm});
            skLineSegment(sketch, "E8.5.1.0", {"start": v(-1173.33, 1054) * mm, "end": v(-1019.33, 1054) * mm});
            skLineSegment(sketch, "E8.5.1.1", {"start": v(-1019.33, 1054) * mm, "end": v(-1019.33, 900) * mm});
            skLineSegment(sketch, "E8.5.1.2", {"start": v(-1173.33, 900) * mm, "end": v(-1019.33, 900) * mm});
            skLineSegment(sketch, "E8.5.1.3", {"start": v(-1173.33, 1054) * mm, "end": v(-1173.33, 900) * mm});
            skLineSegment(sketch, "E8.5.2.0", {"start": v(-1173.33, 898) * mm, "end": v(-1019.33, 898) * mm});
            skLineSegment(sketch, "E8.5.2.1", {"start": v(-1019.33, 898) * mm, "end": v(-1019.33, 744) * mm});
            skLineSegment(sketch, "E8.5.2.2", {"start": v(-1173.33, 744) * mm, "end": v(-1019.33, 744) * mm});
            skLineSegment(sketch, "E8.5.2.3", {"start": v(-1173.33, 898) * mm, "end": v(-1173.33, 744) * mm});
            skLineSegment(sketch, "E8.5.3.0", {"start": v(-1173.33, 742) * mm, "end": v(-1019.33, 742) * mm});
            skLineSegment(sketch, "E8.5.3.1", {"start": v(-1019.33, 742) * mm, "end": v(-1019.33, 588) * mm});
            skLineSegment(sketch, "E8.5.3.2", {"start": v(-1173.33, 588) * mm, "end": v(-1019.33, 588) * mm});
            skLineSegment(sketch, "E8.5.3.3", {"start": v(-1173.33, 742) * mm, "end": v(-1173.33, 588) * mm});
            skLineSegment(sketch, "E8.5.4.0", {"start": v(-1173.33, 586) * mm, "end": v(-1019.33, 586) * mm});
            skLineSegment(sketch, "E8.5.4.1", {"start": v(-1019.33, 586) * mm, "end": v(-1019.33, 432) * mm});
            skLineSegment(sketch, "E8.5.4.2", {"start": v(-1173.33, 432) * mm, "end": v(-1019.33, 432) * mm});
            skLineSegment(sketch, "E8.5.4.3", {"start": v(-1173.33, 586) * mm, "end": v(-1173.33, 432) * mm});
            skLineSegment(sketch, "E8.5.5.0", {"start": v(-1173.33, 430) * mm, "end": v(-1019.33, 430) * mm});
            skLineSegment(sketch, "E8.5.5.1", {"start": v(-1019.33, 430) * mm, "end": v(-1019.33, 276) * mm});
            skLineSegment(sketch, "E8.5.5.2", {"start": v(-1173.33, 276) * mm, "end": v(-1019.33, 276) * mm});
            skLineSegment(sketch, "E8.5.5.3", {"start": v(-1173.33, 430) * mm, "end": v(-1173.33, 276) * mm});
            skLineSegment(sketch, "E8.5.6.0", {"start": v(-1173.33, 274) * mm, "end": v(-1019.33, 274) * mm});
            skLineSegment(sketch, "E8.5.6.1", {"start": v(-1019.33, 274) * mm, "end": v(-1019.33, 120) * mm});
            skLineSegment(sketch, "E8.5.6.2", {"start": v(-1173.33, 120) * mm, "end": v(-1019.33, 120) * mm});
            skLineSegment(sketch, "E8.5.6.3", {"start": v(-1173.33, 274) * mm, "end": v(-1173.33, 120) * mm});
            skLineSegment(sketch, "E8.5.7.0", {"start": v(-1173.33, 118) * mm, "end": v(-1019.33, 118) * mm});
            skLineSegment(sketch, "E8.5.7.1", {"start": v(-1019.33, 118) * mm, "end": v(-1019.33, -36) * mm});
            skLineSegment(sketch, "E8.5.7.2", {"start": v(-1173.33, -36) * mm, "end": v(-1019.33, -36) * mm});
            skLineSegment(sketch, "E8.5.7.3", {"start": v(-1173.33, 118) * mm, "end": v(-1173.33, -36) * mm});
            skLineSegment(sketch, "E8.5.8.0", {"start": v(-1173.33, -38) * mm, "end": v(-1019.33, -38) * mm});
            skLineSegment(sketch, "E8.5.8.1", {"start": v(-1019.33, -38) * mm, "end": v(-1019.33, -192) * mm});
            skLineSegment(sketch, "E8.5.8.2", {"start": v(-1173.33, -192) * mm, "end": v(-1019.33, -192) * mm});
            skLineSegment(sketch, "E8.5.8.3", {"start": v(-1173.33, -38) * mm, "end": v(-1173.33, -192) * mm});
            skLineSegment(sketch, "E8.5.9.0", {"start": v(-1173.33, -194) * mm, "end": v(-1019.33, -194) * mm});
            skLineSegment(sketch, "E8.5.9.1", {"start": v(-1019.33, -194) * mm, "end": v(-1019.33, -348) * mm});
            skLineSegment(sketch, "E8.5.9.2", {"start": v(-1173.33, -348) * mm, "end": v(-1019.33, -348) * mm});
            skLineSegment(sketch, "E8.5.9.3", {"start": v(-1173.33, -194) * mm, "end": v(-1173.33, -348) * mm});
            skLineSegment(sketch, "E8.5.10.0", {"start": v(-1173.33, -350) * mm, "end": v(-1019.33, -350) * mm});
            skLineSegment(sketch, "E8.5.10.1", {"start": v(-1019.33, -350) * mm, "end": v(-1019.33, -504) * mm});
            skLineSegment(sketch, "E8.5.10.2", {"start": v(-1173.33, -504) * mm, "end": v(-1019.33, -504) * mm});
            skLineSegment(sketch, "E8.5.10.3", {"start": v(-1173.33, -350) * mm, "end": v(-1173.33, -504) * mm});
            skLineSegment(sketch, "E8.5.11.0", {"start": v(-1173.33, -506) * mm, "end": v(-1019.33, -506) * mm});
            skLineSegment(sketch, "E8.5.11.1", {"start": v(-1019.33, -506) * mm, "end": v(-1019.33, -660) * mm});
            skLineSegment(sketch, "E8.5.11.2", {"start": v(-1173.33, -660) * mm, "end": v(-1019.33, -660) * mm});
            skLineSegment(sketch, "E8.5.11.3", {"start": v(-1173.33, -506) * mm, "end": v(-1173.33, -660) * mm});
            skLineSegment(sketch, "E8.5.12.0", {"start": v(-1173.33, -662) * mm, "end": v(-1019.33, -662) * mm});
            skLineSegment(sketch, "E8.5.12.1", {"start": v(-1019.33, -662) * mm, "end": v(-1019.33, -816) * mm});
            skLineSegment(sketch, "E8.5.12.2", {"start": v(-1173.33, -816) * mm, "end": v(-1019.33, -816) * mm});
            skLineSegment(sketch, "E8.5.12.3", {"start": v(-1173.33, -662) * mm, "end": v(-1173.33, -816) * mm});
            skLineSegment(sketch, "E8.6.0.0", {"start": v(-1017.33, 1210) * mm, "end": v(-863.33, 1210) * mm});
            skLineSegment(sketch, "E8.6.0.1", {"start": v(-863.33, 1210) * mm, "end": v(-863.33, 1056) * mm});
            skLineSegment(sketch, "E8.6.0.2", {"start": v(-1017.33, 1056) * mm, "end": v(-863.33, 1056) * mm});
            skLineSegment(sketch, "E8.6.0.3", {"start": v(-1017.33, 1210) * mm, "end": v(-1017.33, 1056) * mm});
            skLineSegment(sketch, "E8.6.1.0", {"start": v(-1017.33, 1054) * mm, "end": v(-863.33, 1054) * mm});
            skLineSegment(sketch, "E8.6.1.1", {"start": v(-863.33, 1054) * mm, "end": v(-863.33, 900) * mm});
            skLineSegment(sketch, "E8.6.1.2", {"start": v(-1017.33, 900) * mm, "end": v(-863.33, 900) * mm});
            skLineSegment(sketch, "E8.6.1.3", {"start": v(-1017.33, 1054) * mm, "end": v(-1017.33, 900) * mm});
            skLineSegment(sketch, "E8.6.2.0", {"start": v(-1017.33, 898) * mm, "end": v(-863.33, 898) * mm});
            skLineSegment(sketch, "E8.6.2.1", {"start": v(-863.33, 898) * mm, "end": v(-863.33, 744) * mm});
            skLineSegment(sketch, "E8.6.2.2", {"start": v(-1017.33, 744) * mm, "end": v(-863.33, 744) * mm});
            skLineSegment(sketch, "E8.6.2.3", {"start": v(-1017.33, 898) * mm, "end": v(-1017.33, 744) * mm});
            skLineSegment(sketch, "E8.6.3.0", {"start": v(-1017.33, 742) * mm, "end": v(-863.33, 742) * mm});
            skLineSegment(sketch, "E8.6.3.1", {"start": v(-863.33, 742) * mm, "end": v(-863.33, 588) * mm});
            skLineSegment(sketch, "E8.6.3.2", {"start": v(-1017.33, 588) * mm, "end": v(-863.33, 588) * mm});
            skLineSegment(sketch, "E8.6.3.3", {"start": v(-1017.33, 742) * mm, "end": v(-1017.33, 588) * mm});
            skLineSegment(sketch, "E8.6.4.0", {"start": v(-1017.33, 586) * mm, "end": v(-863.33, 586) * mm});
            skLineSegment(sketch, "E8.6.4.1", {"start": v(-863.33, 586) * mm, "end": v(-863.33, 432) * mm});
            skLineSegment(sketch, "E8.6.4.2", {"start": v(-1017.33, 432) * mm, "end": v(-863.33, 432) * mm});
            skLineSegment(sketch, "E8.6.4.3", {"start": v(-1017.33, 586) * mm, "end": v(-1017.33, 432) * mm});
            skLineSegment(sketch, "E8.6.5.0", {"start": v(-1017.33, 430) * mm, "end": v(-863.33, 430) * mm});
            skLineSegment(sketch, "E8.6.5.1", {"start": v(-863.33, 430) * mm, "end": v(-863.33, 276) * mm});
            skLineSegment(sketch, "E8.6.5.2", {"start": v(-1017.33, 276) * mm, "end": v(-863.33, 276) * mm});
            skLineSegment(sketch, "E8.6.5.3", {"start": v(-1017.33, 430) * mm, "end": v(-1017.33, 276) * mm});
            skLineSegment(sketch, "E8.6.6.0", {"start": v(-1017.33, 274) * mm, "end": v(-863.33, 274) * mm});
            skLineSegment(sketch, "E8.6.6.1", {"start": v(-863.33, 274) * mm, "end": v(-863.33, 120) * mm});
            skLineSegment(sketch, "E8.6.6.2", {"start": v(-1017.33, 120) * mm, "end": v(-863.33, 120) * mm});
            skLineSegment(sketch, "E8.6.6.3", {"start": v(-1017.33, 274) * mm, "end": v(-1017.33, 120) * mm});
            skLineSegment(sketch, "E8.6.7.0", {"start": v(-1017.33, 118) * mm, "end": v(-863.33, 118) * mm});
            skLineSegment(sketch, "E8.6.7.1", {"start": v(-863.33, 118) * mm, "end": v(-863.33, -36) * mm});
            skLineSegment(sketch, "E8.6.7.2", {"start": v(-1017.33, -36) * mm, "end": v(-863.33, -36) * mm});
            skLineSegment(sketch, "E8.6.7.3", {"start": v(-1017.33, 118) * mm, "end": v(-1017.33, -36) * mm});
            skLineSegment(sketch, "E8.6.8.0", {"start": v(-1017.33, -38) * mm, "end": v(-863.33, -38) * mm});
            skLineSegment(sketch, "E8.6.8.1", {"start": v(-863.33, -38) * mm, "end": v(-863.33, -192) * mm});
            skLineSegment(sketch, "E8.6.8.2", {"start": v(-1017.33, -192) * mm, "end": v(-863.33, -192) * mm});
            skLineSegment(sketch, "E8.6.8.3", {"start": v(-1017.33, -38) * mm, "end": v(-1017.33, -192) * mm});
            skLineSegment(sketch, "E8.6.9.0", {"start": v(-1017.33, -194) * mm, "end": v(-863.33, -194) * mm});
            skLineSegment(sketch, "E8.6.9.1", {"start": v(-863.33, -194) * mm, "end": v(-863.33, -348) * mm});
            skLineSegment(sketch, "E8.6.9.2", {"start": v(-1017.33, -348) * mm, "end": v(-863.33, -348) * mm});
            skLineSegment(sketch, "E8.6.9.3", {"start": v(-1017.33, -194) * mm, "end": v(-1017.33, -348) * mm});
            skLineSegment(sketch, "E8.6.10.0", {"start": v(-1017.33, -350) * mm, "end": v(-863.33, -350) * mm});
            skLineSegment(sketch, "E8.6.10.1", {"start": v(-863.33, -350) * mm, "end": v(-863.33, -504) * mm});
            skLineSegment(sketch, "E8.6.10.2", {"start": v(-1017.33, -504) * mm, "end": v(-863.33, -504) * mm});
            skLineSegment(sketch, "E8.6.10.3", {"start": v(-1017.33, -350) * mm, "end": v(-1017.33, -504) * mm});
            skLineSegment(sketch, "E8.6.11.0", {"start": v(-1017.33, -506) * mm, "end": v(-863.33, -506) * mm});
            skLineSegment(sketch, "E8.6.11.1", {"start": v(-863.33, -506) * mm, "end": v(-863.33, -660) * mm});
            skLineSegment(sketch, "E8.6.11.2", {"start": v(-1017.33, -660) * mm, "end": v(-863.33, -660) * mm});
            skLineSegment(sketch, "E8.6.11.3", {"start": v(-1017.33, -506) * mm, "end": v(-1017.33, -660) * mm});
            skLineSegment(sketch, "E8.6.12.0", {"start": v(-1017.33, -662) * mm, "end": v(-863.33, -662) * mm});
            skLineSegment(sketch, "E8.6.12.1", {"start": v(-863.33, -662) * mm, "end": v(-863.33, -816) * mm});
            skLineSegment(sketch, "E8.6.12.2", {"start": v(-1017.33, -816) * mm, "end": v(-863.33, -816) * mm});
            skLineSegment(sketch, "E8.6.12.3", {"start": v(-1017.33, -662) * mm, "end": v(-1017.33, -816) * mm});
            skLineSegment(sketch, "E8.7.0.0", {"start": v(-861.33, 1210) * mm, "end": v(-707.33, 1210) * mm});
            skLineSegment(sketch, "E8.7.0.1", {"start": v(-707.33, 1210) * mm, "end": v(-707.33, 1056) * mm});
            skLineSegment(sketch, "E8.7.0.2", {"start": v(-861.33, 1056) * mm, "end": v(-707.33, 1056) * mm});
            skLineSegment(sketch, "E8.7.0.3", {"start": v(-861.33, 1210) * mm, "end": v(-861.33, 1056) * mm});
            skLineSegment(sketch, "E8.7.1.0", {"start": v(-861.33, 1054) * mm, "end": v(-707.33, 1054) * mm});
            skLineSegment(sketch, "E8.7.1.1", {"start": v(-707.33, 1054) * mm, "end": v(-707.33, 900) * mm});
            skLineSegment(sketch, "E8.7.1.2", {"start": v(-861.33, 900) * mm, "end": v(-707.33, 900) * mm});
            skLineSegment(sketch, "E8.7.1.3", {"start": v(-861.33, 1054) * mm, "end": v(-861.33, 900) * mm});
            skLineSegment(sketch, "E8.7.2.0", {"start": v(-861.33, 898) * mm, "end": v(-707.33, 898) * mm});
            skLineSegment(sketch, "E8.7.2.1", {"start": v(-707.33, 898) * mm, "end": v(-707.33, 744) * mm});
            skLineSegment(sketch, "E8.7.2.2", {"start": v(-861.33, 744) * mm, "end": v(-707.33, 744) * mm});
            skLineSegment(sketch, "E8.7.2.3", {"start": v(-861.33, 898) * mm, "end": v(-861.33, 744) * mm});
            skLineSegment(sketch, "E8.7.3.0", {"start": v(-861.33, 742) * mm, "end": v(-707.33, 742) * mm});
            skLineSegment(sketch, "E8.7.3.1", {"start": v(-707.33, 742) * mm, "end": v(-707.33, 588) * mm});
            skLineSegment(sketch, "E8.7.3.2", {"start": v(-861.33, 588) * mm, "end": v(-707.33, 588) * mm});
            skLineSegment(sketch, "E8.7.3.3", {"start": v(-861.33, 742) * mm, "end": v(-861.33, 588) * mm});
            skLineSegment(sketch, "E8.7.4.0", {"start": v(-861.33, 586) * mm, "end": v(-707.33, 586) * mm});
            skLineSegment(sketch, "E8.7.4.1", {"start": v(-707.33, 586) * mm, "end": v(-707.33, 432) * mm});
            skLineSegment(sketch, "E8.7.4.2", {"start": v(-861.33, 432) * mm, "end": v(-707.33, 432) * mm});
            skLineSegment(sketch, "E8.7.4.3", {"start": v(-861.33, 586) * mm, "end": v(-861.33, 432) * mm});
            skLineSegment(sketch, "E8.7.5.0", {"start": v(-861.33, 430) * mm, "end": v(-707.33, 430) * mm});
            skLineSegment(sketch, "E8.7.5.1", {"start": v(-707.33, 430) * mm, "end": v(-707.33, 276) * mm});
            skLineSegment(sketch, "E8.7.5.2", {"start": v(-861.33, 276) * mm, "end": v(-707.33, 276) * mm});
            skLineSegment(sketch, "E8.7.5.3", {"start": v(-861.33, 430) * mm, "end": v(-861.33, 276) * mm});
            skLineSegment(sketch, "E8.7.6.0", {"start": v(-861.33, 274) * mm, "end": v(-707.33, 274) * mm});
            skLineSegment(sketch, "E8.7.6.1", {"start": v(-707.33, 274) * mm, "end": v(-707.33, 120) * mm});
            skLineSegment(sketch, "E8.7.6.2", {"start": v(-861.33, 120) * mm, "end": v(-707.33, 120) * mm});
            skLineSegment(sketch, "E8.7.6.3", {"start": v(-861.33, 274) * mm, "end": v(-861.33, 120) * mm});
            skLineSegment(sketch, "E8.7.7.0", {"start": v(-861.33, 118) * mm, "end": v(-707.33, 118) * mm});
            skLineSegment(sketch, "E8.7.7.1", {"start": v(-707.33, 118) * mm, "end": v(-707.33, -36) * mm});
            skLineSegment(sketch, "E8.7.7.2", {"start": v(-861.33, -36) * mm, "end": v(-707.33, -36) * mm});
            skLineSegment(sketch, "E8.7.7.3", {"start": v(-861.33, 118) * mm, "end": v(-861.33, -36) * mm});
            skLineSegment(sketch, "E8.7.8.0", {"start": v(-861.33, -38) * mm, "end": v(-707.33, -38) * mm});
            skLineSegment(sketch, "E8.7.8.1", {"start": v(-707.33, -38) * mm, "end": v(-707.33, -192) * mm});
            skLineSegment(sketch, "E8.7.8.2", {"start": v(-861.33, -192) * mm, "end": v(-707.33, -192) * mm});
            skLineSegment(sketch, "E8.7.8.3", {"start": v(-861.33, -38) * mm, "end": v(-861.33, -192) * mm});
            skLineSegment(sketch, "E8.7.9.0", {"start": v(-861.33, -194) * mm, "end": v(-707.33, -194) * mm});
            skLineSegment(sketch, "E8.7.9.1", {"start": v(-707.33, -194) * mm, "end": v(-707.33, -348) * mm});
            skLineSegment(sketch, "E8.7.9.2", {"start": v(-861.33, -348) * mm, "end": v(-707.33, -348) * mm});
            skLineSegment(sketch, "E8.7.9.3", {"start": v(-861.33, -194) * mm, "end": v(-861.33, -348) * mm});
            skLineSegment(sketch, "E8.7.10.0", {"start": v(-861.33, -350) * mm, "end": v(-707.33, -350) * mm});
            skLineSegment(sketch, "E8.7.10.1", {"start": v(-707.33, -350) * mm, "end": v(-707.33, -504) * mm});
            skLineSegment(sketch, "E8.7.10.2", {"start": v(-861.33, -504) * mm, "end": v(-707.33, -504) * mm});
            skLineSegment(sketch, "E8.7.10.3", {"start": v(-861.33, -350) * mm, "end": v(-861.33, -504) * mm});
            skLineSegment(sketch, "E8.7.11.0", {"start": v(-861.33, -506) * mm, "end": v(-707.33, -506) * mm});
            skLineSegment(sketch, "E8.7.11.1", {"start": v(-707.33, -506) * mm, "end": v(-707.33, -660) * mm});
            skLineSegment(sketch, "E8.7.11.2", {"start": v(-861.33, -660) * mm, "end": v(-707.33, -660) * mm});
            skLineSegment(sketch, "E8.7.11.3", {"start": v(-861.33, -506) * mm, "end": v(-861.33, -660) * mm});
            skLineSegment(sketch, "E8.7.12.0", {"start": v(-861.33, -662) * mm, "end": v(-707.33, -662) * mm});
            skLineSegment(sketch, "E8.7.12.1", {"start": v(-707.33, -662) * mm, "end": v(-707.33, -816) * mm});
            skLineSegment(sketch, "E8.7.12.2", {"start": v(-861.33, -816) * mm, "end": v(-707.33, -816) * mm});
            skLineSegment(sketch, "E8.7.12.3", {"start": v(-861.33, -662) * mm, "end": v(-861.33, -816) * mm});
            skLineSegment(sketch, "E8.8.0.0", {"start": v(-705.33, 1210) * mm, "end": v(-551.33, 1210) * mm});
            skLineSegment(sketch, "E8.8.0.1", {"start": v(-551.33, 1210) * mm, "end": v(-551.33, 1056) * mm});
            skLineSegment(sketch, "E8.8.0.2", {"start": v(-705.33, 1056) * mm, "end": v(-551.33, 1056) * mm});
            skLineSegment(sketch, "E8.8.0.3", {"start": v(-705.33, 1210) * mm, "end": v(-705.33, 1056) * mm});
            skLineSegment(sketch, "E8.8.1.0", {"start": v(-705.33, 1054) * mm, "end": v(-551.33, 1054) * mm});
            skLineSegment(sketch, "E8.8.1.1", {"start": v(-551.33, 1054) * mm, "end": v(-551.33, 900) * mm});
            skLineSegment(sketch, "E8.8.1.2", {"start": v(-705.33, 900) * mm, "end": v(-551.33, 900) * mm});
            skLineSegment(sketch, "E8.8.1.3", {"start": v(-705.33, 1054) * mm, "end": v(-705.33, 900) * mm});
            skLineSegment(sketch, "E8.8.2.0", {"start": v(-705.33, 898) * mm, "end": v(-551.33, 898) * mm});
            skLineSegment(sketch, "E8.8.2.1", {"start": v(-551.33, 898) * mm, "end": v(-551.33, 744) * mm});
            skLineSegment(sketch, "E8.8.2.2", {"start": v(-705.33, 744) * mm, "end": v(-551.33, 744) * mm});
            skLineSegment(sketch, "E8.8.2.3", {"start": v(-705.33, 898) * mm, "end": v(-705.33, 744) * mm});
            skLineSegment(sketch, "E8.8.3.0", {"start": v(-705.33, 742) * mm, "end": v(-551.33, 742) * mm});
            skLineSegment(sketch, "E8.8.3.1", {"start": v(-551.33, 742) * mm, "end": v(-551.33, 588) * mm});
            skLineSegment(sketch, "E8.8.3.2", {"start": v(-705.33, 588) * mm, "end": v(-551.33, 588) * mm});
            skLineSegment(sketch, "E8.8.3.3", {"start": v(-705.33, 742) * mm, "end": v(-705.33, 588) * mm});
            skLineSegment(sketch, "E8.8.4.0", {"start": v(-705.33, 586) * mm, "end": v(-551.33, 586) * mm});
            skLineSegment(sketch, "E8.8.4.1", {"start": v(-551.33, 586) * mm, "end": v(-551.33, 432) * mm});
            skLineSegment(sketch, "E8.8.4.2", {"start": v(-705.33, 432) * mm, "end": v(-551.33, 432) * mm});
            skLineSegment(sketch, "E8.8.4.3", {"start": v(-705.33, 586) * mm, "end": v(-705.33, 432) * mm});
            skLineSegment(sketch, "E8.8.5.0", {"start": v(-705.33, 430) * mm, "end": v(-551.33, 430) * mm});
            skLineSegment(sketch, "E8.8.5.1", {"start": v(-551.33, 430) * mm, "end": v(-551.33, 276) * mm});
            skLineSegment(sketch, "E8.8.5.2", {"start": v(-705.33, 276) * mm, "end": v(-551.33, 276) * mm});
            skLineSegment(sketch, "E8.8.5.3", {"start": v(-705.33, 430) * mm, "end": v(-705.33, 276) * mm});
            skLineSegment(sketch, "E8.8.6.0", {"start": v(-705.33, 274) * mm, "end": v(-551.33, 274) * mm});
            skLineSegment(sketch, "E8.8.6.1", {"start": v(-551.33, 274) * mm, "end": v(-551.33, 120) * mm});
            skLineSegment(sketch, "E8.8.6.2", {"start": v(-705.33, 120) * mm, "end": v(-551.33, 120) * mm});
            skLineSegment(sketch, "E8.8.6.3", {"start": v(-705.33, 274) * mm, "end": v(-705.33, 120) * mm});
            skLineSegment(sketch, "E8.8.7.0", {"start": v(-705.33, 118) * mm, "end": v(-551.33, 118) * mm});
            skLineSegment(sketch, "E8.8.7.1", {"start": v(-551.33, 118) * mm, "end": v(-551.33, -36) * mm});
            skLineSegment(sketch, "E8.8.7.2", {"start": v(-705.33, -36) * mm, "end": v(-551.33, -36) * mm});
            skLineSegment(sketch, "E8.8.7.3", {"start": v(-705.33, 118) * mm, "end": v(-705.33, -36) * mm});
            skLineSegment(sketch, "E8.8.8.0", {"start": v(-705.33, -38) * mm, "end": v(-551.33, -38) * mm});
            skLineSegment(sketch, "E8.8.8.1", {"start": v(-551.33, -38) * mm, "end": v(-551.33, -192) * mm});
            skLineSegment(sketch, "E8.8.8.2", {"start": v(-705.33, -192) * mm, "end": v(-551.33, -192) * mm});
            skLineSegment(sketch, "E8.8.8.3", {"start": v(-705.33, -38) * mm, "end": v(-705.33, -192) * mm});
            skLineSegment(sketch, "E8.8.9.0", {"start": v(-705.33, -194) * mm, "end": v(-551.33, -194) * mm});
            skLineSegment(sketch, "E8.8.9.1", {"start": v(-551.33, -194) * mm, "end": v(-551.33, -348) * mm});
            skLineSegment(sketch, "E8.8.9.2", {"start": v(-705.33, -348) * mm, "end": v(-551.33, -348) * mm});
            skLineSegment(sketch, "E8.8.9.3", {"start": v(-705.33, -194) * mm, "end": v(-705.33, -348) * mm});
            skLineSegment(sketch, "E8.8.10.0", {"start": v(-705.33, -350) * mm, "end": v(-551.33, -350) * mm});
            skLineSegment(sketch, "E8.8.10.1", {"start": v(-551.33, -350) * mm, "end": v(-551.33, -504) * mm});
            skLineSegment(sketch, "E8.8.10.2", {"start": v(-705.33, -504) * mm, "end": v(-551.33, -504) * mm});
            skLineSegment(sketch, "E8.8.10.3", {"start": v(-705.33, -350) * mm, "end": v(-705.33, -504) * mm});
            skLineSegment(sketch, "E8.8.11.0", {"start": v(-705.33, -506) * mm, "end": v(-551.33, -506) * mm});
            skLineSegment(sketch, "E8.8.11.1", {"start": v(-551.33, -506) * mm, "end": v(-551.33, -660) * mm});
            skLineSegment(sketch, "E8.8.11.2", {"start": v(-705.33, -660) * mm, "end": v(-551.33, -660) * mm});
            skLineSegment(sketch, "E8.8.11.3", {"start": v(-705.33, -506) * mm, "end": v(-705.33, -660) * mm});
            skLineSegment(sketch, "E8.8.12.0", {"start": v(-705.33, -662) * mm, "end": v(-551.33, -662) * mm});
            skLineSegment(sketch, "E8.8.12.1", {"start": v(-551.33, -662) * mm, "end": v(-551.33, -816) * mm});
            skLineSegment(sketch, "E8.8.12.2", {"start": v(-705.33, -816) * mm, "end": v(-551.33, -816) * mm});
            skLineSegment(sketch, "E8.8.12.3", {"start": v(-705.33, -662) * mm, "end": v(-705.33, -816) * mm});
            skLineSegment(sketch, "E8.9.0.0", {"start": v(-549.33, 1210) * mm, "end": v(-395.33, 1210) * mm});
            skLineSegment(sketch, "E8.9.0.1", {"start": v(-395.33, 1210) * mm, "end": v(-395.33, 1056) * mm});
            skLineSegment(sketch, "E8.9.0.2", {"start": v(-549.33, 1056) * mm, "end": v(-395.33, 1056) * mm});
            skLineSegment(sketch, "E8.9.0.3", {"start": v(-549.33, 1210) * mm, "end": v(-549.33, 1056) * mm});
            skLineSegment(sketch, "E8.9.1.0", {"start": v(-549.33, 1054) * mm, "end": v(-395.33, 1054) * mm});
            skLineSegment(sketch, "E8.9.1.1", {"start": v(-395.33, 1054) * mm, "end": v(-395.33, 900) * mm});
            skLineSegment(sketch, "E8.9.1.2", {"start": v(-549.33, 900) * mm, "end": v(-395.33, 900) * mm});
            skLineSegment(sketch, "E8.9.1.3", {"start": v(-549.33, 1054) * mm, "end": v(-549.33, 900) * mm});
            skLineSegment(sketch, "E8.9.2.0", {"start": v(-549.33, 898) * mm, "end": v(-395.33, 898) * mm});
            skLineSegment(sketch, "E8.9.2.1", {"start": v(-395.33, 898) * mm, "end": v(-395.33, 744) * mm});
            skLineSegment(sketch, "E8.9.2.2", {"start": v(-549.33, 744) * mm, "end": v(-395.33, 744) * mm});
            skLineSegment(sketch, "E8.9.2.3", {"start": v(-549.33, 898) * mm, "end": v(-549.33, 744) * mm});
            skLineSegment(sketch, "E8.9.3.0", {"start": v(-549.33, 742) * mm, "end": v(-395.33, 742) * mm});
            skLineSegment(sketch, "E8.9.3.1", {"start": v(-395.33, 742) * mm, "end": v(-395.33, 588) * mm});
            skLineSegment(sketch, "E8.9.3.2", {"start": v(-549.33, 588) * mm, "end": v(-395.33, 588) * mm});
            skLineSegment(sketch, "E8.9.3.3", {"start": v(-549.33, 742) * mm, "end": v(-549.33, 588) * mm});
            skLineSegment(sketch, "E8.9.4.0", {"start": v(-549.33, 586) * mm, "end": v(-395.33, 586) * mm});
            skLineSegment(sketch, "E8.9.4.1", {"start": v(-395.33, 586) * mm, "end": v(-395.33, 432) * mm});
            skLineSegment(sketch, "E8.9.4.2", {"start": v(-549.33, 432) * mm, "end": v(-395.33, 432) * mm});
            skLineSegment(sketch, "E8.9.4.3", {"start": v(-549.33, 586) * mm, "end": v(-549.33, 432) * mm});
            skLineSegment(sketch, "E8.9.5.0", {"start": v(-549.33, 430) * mm, "end": v(-395.33, 430) * mm});
            skLineSegment(sketch, "E8.9.5.1", {"start": v(-395.33, 430) * mm, "end": v(-395.33, 276) * mm});
            skLineSegment(sketch, "E8.9.5.2", {"start": v(-549.33, 276) * mm, "end": v(-395.33, 276) * mm});
            skLineSegment(sketch, "E8.9.5.3", {"start": v(-549.33, 430) * mm, "end": v(-549.33, 276) * mm});
            skLineSegment(sketch, "E8.9.6.0", {"start": v(-549.33, 274) * mm, "end": v(-395.33, 274) * mm});
            skLineSegment(sketch, "E8.9.6.1", {"start": v(-395.33, 274) * mm, "end": v(-395.33, 120) * mm});
            skLineSegment(sketch, "E8.9.6.2", {"start": v(-549.33, 120) * mm, "end": v(-395.33, 120) * mm});
            skLineSegment(sketch, "E8.9.6.3", {"start": v(-549.33, 274) * mm, "end": v(-549.33, 120) * mm});
            skLineSegment(sketch, "E8.9.7.0", {"start": v(-549.33, 118) * mm, "end": v(-395.33, 118) * mm});
            skLineSegment(sketch, "E8.9.7.1", {"start": v(-395.33, 118) * mm, "end": v(-395.33, -36) * mm});
            skLineSegment(sketch, "E8.9.7.2", {"start": v(-549.33, -36) * mm, "end": v(-395.33, -36) * mm});
            skLineSegment(sketch, "E8.9.7.3", {"start": v(-549.33, 118) * mm, "end": v(-549.33, -36) * mm});
            skLineSegment(sketch, "E8.9.8.0", {"start": v(-549.33, -38) * mm, "end": v(-395.33, -38) * mm});
            skLineSegment(sketch, "E8.9.8.1", {"start": v(-395.33, -38) * mm, "end": v(-395.33, -192) * mm});
            skLineSegment(sketch, "E8.9.8.2", {"start": v(-549.33, -192) * mm, "end": v(-395.33, -192) * mm});
            skLineSegment(sketch, "E8.9.8.3", {"start": v(-549.33, -38) * mm, "end": v(-549.33, -192) * mm});
            skLineSegment(sketch, "E8.9.9.0", {"start": v(-549.33, -194) * mm, "end": v(-395.33, -194) * mm});
            skLineSegment(sketch, "E8.9.9.1", {"start": v(-395.33, -194) * mm, "end": v(-395.33, -348) * mm});
            skLineSegment(sketch, "E8.9.9.2", {"start": v(-549.33, -348) * mm, "end": v(-395.33, -348) * mm});
            skLineSegment(sketch, "E8.9.9.3", {"start": v(-549.33, -194) * mm, "end": v(-549.33, -348) * mm});
            skLineSegment(sketch, "E8.9.10.0", {"start": v(-549.33, -350) * mm, "end": v(-395.33, -350) * mm});
            skLineSegment(sketch, "E8.9.10.1", {"start": v(-395.33, -350) * mm, "end": v(-395.33, -504) * mm});
            skLineSegment(sketch, "E8.9.10.2", {"start": v(-549.33, -504) * mm, "end": v(-395.33, -504) * mm});
            skLineSegment(sketch, "E8.9.10.3", {"start": v(-549.33, -350) * mm, "end": v(-549.33, -504) * mm});
            skLineSegment(sketch, "E8.9.11.0", {"start": v(-549.33, -506) * mm, "end": v(-395.33, -506) * mm});
            skLineSegment(sketch, "E8.9.11.1", {"start": v(-395.33, -506) * mm, "end": v(-395.33, -660) * mm});
            skLineSegment(sketch, "E8.9.11.2", {"start": v(-549.33, -660) * mm, "end": v(-395.33, -660) * mm});
            skLineSegment(sketch, "E8.9.11.3", {"start": v(-549.33, -506) * mm, "end": v(-549.33, -660) * mm});
            skLineSegment(sketch, "E8.9.12.0", {"start": v(-549.33, -662) * mm, "end": v(-395.33, -662) * mm});
            skLineSegment(sketch, "E8.9.12.1", {"start": v(-395.33, -662) * mm, "end": v(-395.33, -816) * mm});
            skLineSegment(sketch, "E8.9.12.2", {"start": v(-549.33, -816) * mm, "end": v(-395.33, -816) * mm});
            skLineSegment(sketch, "E8.9.12.3", {"start": v(-549.33, -662) * mm, "end": v(-549.33, -816) * mm});
            skLineSegment(sketch, "E8.10.0.0", {"start": v(-393.33, 1210) * mm, "end": v(-239.33, 1210) * mm});
            skLineSegment(sketch, "E8.10.0.1", {"start": v(-239.33, 1210) * mm, "end": v(-239.33, 1056) * mm});
            skLineSegment(sketch, "E8.10.0.2", {"start": v(-393.33, 1056) * mm, "end": v(-239.33, 1056) * mm});
            skLineSegment(sketch, "E8.10.0.3", {"start": v(-393.33, 1210) * mm, "end": v(-393.33, 1056) * mm});
            skLineSegment(sketch, "E8.10.1.0", {"start": v(-393.33, 1054) * mm, "end": v(-239.33, 1054) * mm});
            skLineSegment(sketch, "E8.10.1.1", {"start": v(-239.33, 1054) * mm, "end": v(-239.33, 900) * mm});
            skLineSegment(sketch, "E8.10.1.2", {"start": v(-393.33, 900) * mm, "end": v(-239.33, 900) * mm});
            skLineSegment(sketch, "E8.10.1.3", {"start": v(-393.33, 1054) * mm, "end": v(-393.33, 900) * mm});
            skLineSegment(sketch, "E8.10.2.0", {"start": v(-393.33, 898) * mm, "end": v(-239.33, 898) * mm});
            skLineSegment(sketch, "E8.10.2.1", {"start": v(-239.33, 898) * mm, "end": v(-239.33, 744) * mm});
            skLineSegment(sketch, "E8.10.2.2", {"start": v(-393.33, 744) * mm, "end": v(-239.33, 744) * mm});
            skLineSegment(sketch, "E8.10.2.3", {"start": v(-393.33, 898) * mm, "end": v(-393.33, 744) * mm});
            skLineSegment(sketch, "E8.10.3.0", {"start": v(-393.33, 742) * mm, "end": v(-239.33, 742) * mm});
            skLineSegment(sketch, "E8.10.3.1", {"start": v(-239.33, 742) * mm, "end": v(-239.33, 588) * mm});
            skLineSegment(sketch, "E8.10.3.2", {"start": v(-393.33, 588) * mm, "end": v(-239.33, 588) * mm});
            skLineSegment(sketch, "E8.10.3.3", {"start": v(-393.33, 742) * mm, "end": v(-393.33, 588) * mm});
            skLineSegment(sketch, "E8.10.4.0", {"start": v(-393.33, 586) * mm, "end": v(-239.33, 586) * mm});
            skLineSegment(sketch, "E8.10.4.1", {"start": v(-239.33, 586) * mm, "end": v(-239.33, 432) * mm});
            skLineSegment(sketch, "E8.10.4.2", {"start": v(-393.33, 432) * mm, "end": v(-239.33, 432) * mm});
            skLineSegment(sketch, "E8.10.4.3", {"start": v(-393.33, 586) * mm, "end": v(-393.33, 432) * mm});
            skLineSegment(sketch, "E8.10.5.0", {"start": v(-393.33, 430) * mm, "end": v(-239.33, 430) * mm});
            skLineSegment(sketch, "E8.10.5.1", {"start": v(-239.33, 430) * mm, "end": v(-239.33, 276) * mm});
            skLineSegment(sketch, "E8.10.5.2", {"start": v(-393.33, 276) * mm, "end": v(-239.33, 276) * mm});
            skLineSegment(sketch, "E8.10.5.3", {"start": v(-393.33, 430) * mm, "end": v(-393.33, 276) * mm});
            skLineSegment(sketch, "E8.10.6.0", {"start": v(-393.33, 274) * mm, "end": v(-239.33, 274) * mm});
            skLineSegment(sketch, "E8.10.6.1", {"start": v(-239.33, 274) * mm, "end": v(-239.33, 120) * mm});
            skLineSegment(sketch, "E8.10.6.2", {"start": v(-393.33, 120) * mm, "end": v(-239.33, 120) * mm});
            skLineSegment(sketch, "E8.10.6.3", {"start": v(-393.33, 274) * mm, "end": v(-393.33, 120) * mm});
            skLineSegment(sketch, "E8.10.7.0", {"start": v(-393.33, 118) * mm, "end": v(-239.33, 118) * mm});
            skLineSegment(sketch, "E8.10.7.1", {"start": v(-239.33, 118) * mm, "end": v(-239.33, -36) * mm});
            skLineSegment(sketch, "E8.10.7.2", {"start": v(-393.33, -36) * mm, "end": v(-239.33, -36) * mm});
            skLineSegment(sketch, "E8.10.7.3", {"start": v(-393.33, 118) * mm, "end": v(-393.33, -36) * mm});
            skLineSegment(sketch, "E8.10.8.0", {"start": v(-393.33, -38) * mm, "end": v(-239.33, -38) * mm});
            skLineSegment(sketch, "E8.10.8.1", {"start": v(-239.33, -38) * mm, "end": v(-239.33, -192) * mm});
            skLineSegment(sketch, "E8.10.8.2", {"start": v(-393.33, -192) * mm, "end": v(-239.33, -192) * mm});
            skLineSegment(sketch, "E8.10.8.3", {"start": v(-393.33, -38) * mm, "end": v(-393.33, -192) * mm});
            skLineSegment(sketch, "E8.10.9.0", {"start": v(-393.33, -194) * mm, "end": v(-239.33, -194) * mm});
            skLineSegment(sketch, "E8.10.9.1", {"start": v(-239.33, -194) * mm, "end": v(-239.33, -348) * mm});
            skLineSegment(sketch, "E8.10.9.2", {"start": v(-393.33, -348) * mm, "end": v(-239.33, -348) * mm});
            skLineSegment(sketch, "E8.10.9.3", {"start": v(-393.33, -194) * mm, "end": v(-393.33, -348) * mm});
            skLineSegment(sketch, "E8.10.10.0", {"start": v(-393.33, -350) * mm, "end": v(-239.33, -350) * mm});
            skLineSegment(sketch, "E8.10.10.1", {"start": v(-239.33, -350) * mm, "end": v(-239.33, -504) * mm});
            skLineSegment(sketch, "E8.10.10.2", {"start": v(-393.33, -504) * mm, "end": v(-239.33, -504) * mm});
            skLineSegment(sketch, "E8.10.10.3", {"start": v(-393.33, -350) * mm, "end": v(-393.33, -504) * mm});
            skLineSegment(sketch, "E8.10.11.0", {"start": v(-393.33, -506) * mm, "end": v(-239.33, -506) * mm});
            skLineSegment(sketch, "E8.10.11.1", {"start": v(-239.33, -506) * mm, "end": v(-239.33, -660) * mm});
            skLineSegment(sketch, "E8.10.11.2", {"start": v(-393.33, -660) * mm, "end": v(-239.33, -660) * mm});
            skLineSegment(sketch, "E8.10.11.3", {"start": v(-393.33, -506) * mm, "end": v(-393.33, -660) * mm});
            skLineSegment(sketch, "E8.10.12.0", {"start": v(-393.33, -662) * mm, "end": v(-239.33, -662) * mm});
            skLineSegment(sketch, "E8.10.12.1", {"start": v(-239.33, -662) * mm, "end": v(-239.33, -816) * mm});
            skLineSegment(sketch, "E8.10.12.2", {"start": v(-393.33, -816) * mm, "end": v(-239.33, -816) * mm});
            skLineSegment(sketch, "E8.10.12.3", {"start": v(-393.33, -662) * mm, "end": v(-393.33, -816) * mm});
            skLineSegment(sketch, "E8.11.0.0", {"start": v(-237.33, 1210) * mm, "end": v(-83.33, 1210) * mm});
            skLineSegment(sketch, "E8.11.0.1", {"start": v(-83.33, 1210) * mm, "end": v(-83.33, 1056) * mm});
            skLineSegment(sketch, "E8.11.0.2", {"start": v(-237.33, 1056) * mm, "end": v(-83.33, 1056) * mm});
            skLineSegment(sketch, "E8.11.0.3", {"start": v(-237.33, 1210) * mm, "end": v(-237.33, 1056) * mm});
            skLineSegment(sketch, "E8.11.1.0", {"start": v(-237.33, 1054) * mm, "end": v(-83.33, 1054) * mm});
            skLineSegment(sketch, "E8.11.1.1", {"start": v(-83.33, 1054) * mm, "end": v(-83.33, 900) * mm});
            skLineSegment(sketch, "E8.11.1.2", {"start": v(-237.33, 900) * mm, "end": v(-83.33, 900) * mm});
            skLineSegment(sketch, "E8.11.1.3", {"start": v(-237.33, 1054) * mm, "end": v(-237.33, 900) * mm});
            skLineSegment(sketch, "E8.11.2.0", {"start": v(-237.33, 898) * mm, "end": v(-83.33, 898) * mm});
            skLineSegment(sketch, "E8.11.2.1", {"start": v(-83.33, 898) * mm, "end": v(-83.33, 744) * mm});
            skLineSegment(sketch, "E8.11.2.2", {"start": v(-237.33, 744) * mm, "end": v(-83.33, 744) * mm});
            skLineSegment(sketch, "E8.11.2.3", {"start": v(-237.33, 898) * mm, "end": v(-237.33, 744) * mm});
            skLineSegment(sketch, "E8.11.3.0", {"start": v(-237.33, 742) * mm, "end": v(-83.33, 742) * mm});
            skLineSegment(sketch, "E8.11.3.1", {"start": v(-83.33, 742) * mm, "end": v(-83.33, 588) * mm});
            skLineSegment(sketch, "E8.11.3.2", {"start": v(-237.33, 588) * mm, "end": v(-83.33, 588) * mm});
            skLineSegment(sketch, "E8.11.3.3", {"start": v(-237.33, 742) * mm, "end": v(-237.33, 588) * mm});
            skLineSegment(sketch, "E8.11.4.0", {"start": v(-237.33, 586) * mm, "end": v(-83.33, 586) * mm});
            skLineSegment(sketch, "E8.11.4.1", {"start": v(-83.33, 586) * mm, "end": v(-83.33, 432) * mm});
            skLineSegment(sketch, "E8.11.4.2", {"start": v(-237.33, 432) * mm, "end": v(-83.33, 432) * mm});
            skLineSegment(sketch, "E8.11.4.3", {"start": v(-237.33, 586) * mm, "end": v(-237.33, 432) * mm});
            skLineSegment(sketch, "E8.11.5.0", {"start": v(-237.33, 430) * mm, "end": v(-83.33, 430) * mm});
            skLineSegment(sketch, "E8.11.5.1", {"start": v(-83.33, 430) * mm, "end": v(-83.33, 276) * mm});
            skLineSegment(sketch, "E8.11.5.2", {"start": v(-237.33, 276) * mm, "end": v(-83.33, 276) * mm});
            skLineSegment(sketch, "E8.11.5.3", {"start": v(-237.33, 430) * mm, "end": v(-237.33, 276) * mm});
            skLineSegment(sketch, "E8.11.6.0", {"start": v(-237.33, 274) * mm, "end": v(-83.33, 274) * mm});
            skLineSegment(sketch, "E8.11.6.1", {"start": v(-83.33, 274) * mm, "end": v(-83.33, 120) * mm});
            skLineSegment(sketch, "E8.11.6.2", {"start": v(-237.33, 120) * mm, "end": v(-83.33, 120) * mm});
            skLineSegment(sketch, "E8.11.6.3", {"start": v(-237.33, 274) * mm, "end": v(-237.33, 120) * mm});
            skLineSegment(sketch, "E8.11.7.0", {"start": v(-237.33, 118) * mm, "end": v(-83.33, 118) * mm});
            skLineSegment(sketch, "E8.11.7.1", {"start": v(-83.33, 118) * mm, "end": v(-83.33, -36) * mm});
            skLineSegment(sketch, "E8.11.7.2", {"start": v(-237.33, -36) * mm, "end": v(-83.33, -36) * mm});
            skLineSegment(sketch, "E8.11.7.3", {"start": v(-237.33, 118) * mm, "end": v(-237.33, -36) * mm});
            skLineSegment(sketch, "E8.11.8.0", {"start": v(-237.33, -38) * mm, "end": v(-83.33, -38) * mm});
            skLineSegment(sketch, "E8.11.8.1", {"start": v(-83.33, -38) * mm, "end": v(-83.33, -192) * mm});
            skLineSegment(sketch, "E8.11.8.2", {"start": v(-237.33, -192) * mm, "end": v(-83.33, -192) * mm});
            skLineSegment(sketch, "E8.11.8.3", {"start": v(-237.33, -38) * mm, "end": v(-237.33, -192) * mm});
            skLineSegment(sketch, "E8.11.9.0", {"start": v(-237.33, -194) * mm, "end": v(-83.33, -194) * mm});
            skLineSegment(sketch, "E8.11.9.1", {"start": v(-83.33, -194) * mm, "end": v(-83.33, -348) * mm});
            skLineSegment(sketch, "E8.11.9.2", {"start": v(-237.33, -348) * mm, "end": v(-83.33, -348) * mm});
            skLineSegment(sketch, "E8.11.9.3", {"start": v(-237.33, -194) * mm, "end": v(-237.33, -348) * mm});
            skLineSegment(sketch, "E8.11.10.0", {"start": v(-237.33, -350) * mm, "end": v(-83.33, -350) * mm});
            skLineSegment(sketch, "E8.11.10.1", {"start": v(-83.33, -350) * mm, "end": v(-83.33, -504) * mm});
            skLineSegment(sketch, "E8.11.10.2", {"start": v(-237.33, -504) * mm, "end": v(-83.33, -504) * mm});
            skLineSegment(sketch, "E8.11.10.3", {"start": v(-237.33, -350) * mm, "end": v(-237.33, -504) * mm});
            skLineSegment(sketch, "E8.11.11.0", {"start": v(-237.33, -506) * mm, "end": v(-83.33, -506) * mm});
            skLineSegment(sketch, "E8.11.11.1", {"start": v(-83.33, -506) * mm, "end": v(-83.33, -660) * mm});
            skLineSegment(sketch, "E8.11.11.2", {"start": v(-237.33, -660) * mm, "end": v(-83.33, -660) * mm});
            skLineSegment(sketch, "E8.11.11.3", {"start": v(-237.33, -506) * mm, "end": v(-237.33, -660) * mm});
            skLineSegment(sketch, "E8.11.12.0", {"start": v(-237.33, -662) * mm, "end": v(-83.33, -662) * mm});
            skLineSegment(sketch, "E8.11.12.1", {"start": v(-83.33, -662) * mm, "end": v(-83.33, -816) * mm});
            skLineSegment(sketch, "E8.11.12.2", {"start": v(-237.33, -816) * mm, "end": v(-83.33, -816) * mm});
            skLineSegment(sketch, "E8.11.12.3", {"start": v(-237.33, -662) * mm, "end": v(-237.33, -816) * mm});
            skLineSegment(sketch, "E8.12.0.0", {"start": v(-81.33, 1210) * mm, "end": v(72.67, 1210) * mm});
            skLineSegment(sketch, "E8.12.0.1", {"start": v(72.67, 1210) * mm, "end": v(72.67, 1056) * mm});
            skLineSegment(sketch, "E8.12.0.2", {"start": v(-81.33, 1056) * mm, "end": v(72.67, 1056) * mm});
            skLineSegment(sketch, "E8.12.0.3", {"start": v(-81.33, 1210) * mm, "end": v(-81.33, 1056) * mm});
            skLineSegment(sketch, "E8.12.1.0", {"start": v(-81.33, 1054) * mm, "end": v(72.67, 1054) * mm});
            skLineSegment(sketch, "E8.12.1.1", {"start": v(72.67, 1054) * mm, "end": v(72.67, 900) * mm});
            skLineSegment(sketch, "E8.12.1.2", {"start": v(-81.33, 900) * mm, "end": v(72.67, 900) * mm});
            skLineSegment(sketch, "E8.12.1.3", {"start": v(-81.33, 1054) * mm, "end": v(-81.33, 900) * mm});
            skLineSegment(sketch, "E8.12.2.0", {"start": v(-81.33, 898) * mm, "end": v(72.67, 898) * mm});
            skLineSegment(sketch, "E8.12.2.1", {"start": v(72.67, 898) * mm, "end": v(72.67, 744) * mm});
            skLineSegment(sketch, "E8.12.2.2", {"start": v(-81.33, 744) * mm, "end": v(72.67, 744) * mm});
            skLineSegment(sketch, "E8.12.2.3", {"start": v(-81.33, 898) * mm, "end": v(-81.33, 744) * mm});
            skLineSegment(sketch, "E8.12.3.0", {"start": v(-81.33, 742) * mm, "end": v(72.67, 742) * mm});
            skLineSegment(sketch, "E8.12.3.1", {"start": v(72.67, 742) * mm, "end": v(72.67, 588) * mm});
            skLineSegment(sketch, "E8.12.3.2", {"start": v(-81.33, 588) * mm, "end": v(72.67, 588) * mm});
            skLineSegment(sketch, "E8.12.3.3", {"start": v(-81.33, 742) * mm, "end": v(-81.33, 588) * mm});
            skLineSegment(sketch, "E8.12.4.0", {"start": v(-81.33, 586) * mm, "end": v(72.67, 586) * mm});
            skLineSegment(sketch, "E8.12.4.1", {"start": v(72.67, 586) * mm, "end": v(72.67, 432) * mm});
            skLineSegment(sketch, "E8.12.4.2", {"start": v(-81.33, 432) * mm, "end": v(72.67, 432) * mm});
            skLineSegment(sketch, "E8.12.4.3", {"start": v(-81.33, 586) * mm, "end": v(-81.33, 432) * mm});
            skLineSegment(sketch, "E8.12.5.0", {"start": v(-81.33, 430) * mm, "end": v(72.67, 430) * mm});
            skLineSegment(sketch, "E8.12.5.1", {"start": v(72.67, 430) * mm, "end": v(72.67, 276) * mm});
            skLineSegment(sketch, "E8.12.5.2", {"start": v(-81.33, 276) * mm, "end": v(72.67, 276) * mm});
            skLineSegment(sketch, "E8.12.5.3", {"start": v(-81.33, 430) * mm, "end": v(-81.33, 276) * mm});
            skLineSegment(sketch, "E8.12.6.0", {"start": v(-81.33, 274) * mm, "end": v(72.67, 274) * mm});
            skLineSegment(sketch, "E8.12.6.1", {"start": v(72.67, 274) * mm, "end": v(72.67, 120) * mm});
            skLineSegment(sketch, "E8.12.6.2", {"start": v(-81.33, 120) * mm, "end": v(72.67, 120) * mm});
            skLineSegment(sketch, "E8.12.6.3", {"start": v(-81.33, 274) * mm, "end": v(-81.33, 120) * mm});
            skLineSegment(sketch, "E8.12.7.0", {"start": v(-81.33, 118) * mm, "end": v(72.67, 118) * mm});
            skLineSegment(sketch, "E8.12.7.1", {"start": v(72.67, 118) * mm, "end": v(72.67, -36) * mm});
            skLineSegment(sketch, "E8.12.7.2", {"start": v(-81.33, -36) * mm, "end": v(72.67, -36) * mm});
            skLineSegment(sketch, "E8.12.7.3", {"start": v(-81.33, 118) * mm, "end": v(-81.33, -36) * mm});
            skLineSegment(sketch, "E8.12.8.0", {"start": v(-81.33, -38) * mm, "end": v(72.67, -38) * mm});
            skLineSegment(sketch, "E8.12.8.1", {"start": v(72.67, -38) * mm, "end": v(72.67, -192) * mm});
            skLineSegment(sketch, "E8.12.8.2", {"start": v(-81.33, -192) * mm, "end": v(72.67, -192) * mm});
            skLineSegment(sketch, "E8.12.8.3", {"start": v(-81.33, -38) * mm, "end": v(-81.33, -192) * mm});
            skLineSegment(sketch, "E8.12.9.0", {"start": v(-81.33, -194) * mm, "end": v(72.67, -194) * mm});
            skLineSegment(sketch, "E8.12.9.1", {"start": v(72.67, -194) * mm, "end": v(72.67, -348) * mm});
            skLineSegment(sketch, "E8.12.9.2", {"start": v(-81.33, -348) * mm, "end": v(72.67, -348) * mm});
            skLineSegment(sketch, "E8.12.9.3", {"start": v(-81.33, -194) * mm, "end": v(-81.33, -348) * mm});
            skLineSegment(sketch, "E8.12.10.0", {"start": v(-81.33, -350) * mm, "end": v(72.67, -350) * mm});
            skLineSegment(sketch, "E8.12.10.1", {"start": v(72.67, -350) * mm, "end": v(72.67, -504) * mm});
            skLineSegment(sketch, "E8.12.10.2", {"start": v(-81.33, -504) * mm, "end": v(72.67, -504) * mm});
            skLineSegment(sketch, "E8.12.10.3", {"start": v(-81.33, -350) * mm, "end": v(-81.33, -504) * mm});
            skLineSegment(sketch, "E8.12.11.0", {"start": v(-81.33, -506) * mm, "end": v(72.67, -506) * mm});
            skLineSegment(sketch, "E8.12.11.1", {"start": v(72.67, -506) * mm, "end": v(72.67, -660) * mm});
            skLineSegment(sketch, "E8.12.11.2", {"start": v(-81.33, -660) * mm, "end": v(72.67, -660) * mm});
            skLineSegment(sketch, "E8.12.11.3", {"start": v(-81.33, -506) * mm, "end": v(-81.33, -660) * mm});
            skLineSegment(sketch, "E8.12.12.0", {"start": v(-81.33, -662) * mm, "end": v(72.67, -662) * mm});
            skLineSegment(sketch, "E8.12.12.1", {"start": v(72.67, -662) * mm, "end": v(72.67, -816) * mm});
            skLineSegment(sketch, "E8.12.12.2", {"start": v(-81.33, -816) * mm, "end": v(72.67, -816) * mm});
            skLineSegment(sketch, "E8.12.12.3", {"start": v(-81.33, -662) * mm, "end": v(-81.33, -816) * mm});
            skLineSegment(sketch, "E8.13.0.0", {"start": v(74.67, 1210) * mm, "end": v(228.67, 1210) * mm});
            skLineSegment(sketch, "E8.13.0.1", {"start": v(228.67, 1210) * mm, "end": v(228.67, 1056) * mm});
            skLineSegment(sketch, "E8.13.0.2", {"start": v(74.67, 1056) * mm, "end": v(228.67, 1056) * mm});
            skLineSegment(sketch, "E8.13.0.3", {"start": v(74.67, 1210) * mm, "end": v(74.67, 1056) * mm});
            skLineSegment(sketch, "E8.13.1.0", {"start": v(74.67, 1054) * mm, "end": v(228.67, 1054) * mm});
            skLineSegment(sketch, "E8.13.1.1", {"start": v(228.67, 1054) * mm, "end": v(228.67, 900) * mm});
            skLineSegment(sketch, "E8.13.1.2", {"start": v(74.67, 900) * mm, "end": v(228.67, 900) * mm});
            skLineSegment(sketch, "E8.13.1.3", {"start": v(74.67, 1054) * mm, "end": v(74.67, 900) * mm});
            skLineSegment(sketch, "E8.13.2.0", {"start": v(74.67, 898) * mm, "end": v(228.67, 898) * mm});
            skLineSegment(sketch, "E8.13.2.1", {"start": v(228.67, 898) * mm, "end": v(228.67, 744) * mm});
            skLineSegment(sketch, "E8.13.2.2", {"start": v(74.67, 744) * mm, "end": v(228.67, 744) * mm});
            skLineSegment(sketch, "E8.13.2.3", {"start": v(74.67, 898) * mm, "end": v(74.67, 744) * mm});
            skLineSegment(sketch, "E8.13.3.0", {"start": v(74.67, 742) * mm, "end": v(228.67, 742) * mm});
            skLineSegment(sketch, "E8.13.3.1", {"start": v(228.67, 742) * mm, "end": v(228.67, 588) * mm});
            skLineSegment(sketch, "E8.13.3.2", {"start": v(74.67, 588) * mm, "end": v(228.67, 588) * mm});
            skLineSegment(sketch, "E8.13.3.3", {"start": v(74.67, 742) * mm, "end": v(74.67, 588) * mm});
            skLineSegment(sketch, "E8.13.4.0", {"start": v(74.67, 586) * mm, "end": v(228.67, 586) * mm});
            skLineSegment(sketch, "E8.13.4.1", {"start": v(228.67, 586) * mm, "end": v(228.67, 432) * mm});
            skLineSegment(sketch, "E8.13.4.2", {"start": v(74.67, 432) * mm, "end": v(228.67, 432) * mm});
            skLineSegment(sketch, "E8.13.4.3", {"start": v(74.67, 586) * mm, "end": v(74.67, 432) * mm});
            skLineSegment(sketch, "E8.13.5.0", {"start": v(74.67, 430) * mm, "end": v(228.67, 430) * mm});
            skLineSegment(sketch, "E8.13.5.1", {"start": v(228.67, 430) * mm, "end": v(228.67, 276) * mm});
            skLineSegment(sketch, "E8.13.5.2", {"start": v(74.67, 276) * mm, "end": v(228.67, 276) * mm});
            skLineSegment(sketch, "E8.13.5.3", {"start": v(74.67, 430) * mm, "end": v(74.67, 276) * mm});
            skLineSegment(sketch, "E8.13.6.0", {"start": v(74.67, 274) * mm, "end": v(228.67, 274) * mm});
            skLineSegment(sketch, "E8.13.6.1", {"start": v(228.67, 274) * mm, "end": v(228.67, 120) * mm});
            skLineSegment(sketch, "E8.13.6.2", {"start": v(74.67, 120) * mm, "end": v(228.67, 120) * mm});
            skLineSegment(sketch, "E8.13.6.3", {"start": v(74.67, 274) * mm, "end": v(74.67, 120) * mm});
            skLineSegment(sketch, "E8.13.7.0", {"start": v(74.67, 118) * mm, "end": v(228.67, 118) * mm});
            skLineSegment(sketch, "E8.13.7.1", {"start": v(228.67, 118) * mm, "end": v(228.67, -36) * mm});
            skLineSegment(sketch, "E8.13.7.2", {"start": v(74.67, -36) * mm, "end": v(228.67, -36) * mm});
            skLineSegment(sketch, "E8.13.7.3", {"start": v(74.67, 118) * mm, "end": v(74.67, -36) * mm});
            skLineSegment(sketch, "E8.13.8.0", {"start": v(74.67, -38) * mm, "end": v(228.67, -38) * mm});
            skLineSegment(sketch, "E8.13.8.1", {"start": v(228.67, -38) * mm, "end": v(228.67, -192) * mm});
            skLineSegment(sketch, "E8.13.8.2", {"start": v(74.67, -192) * mm, "end": v(228.67, -192) * mm});
            skLineSegment(sketch, "E8.13.8.3", {"start": v(74.67, -38) * mm, "end": v(74.67, -192) * mm});
            skLineSegment(sketch, "E8.13.9.0", {"start": v(74.67, -194) * mm, "end": v(228.67, -194) * mm});
            skLineSegment(sketch, "E8.13.9.1", {"start": v(228.67, -194) * mm, "end": v(228.67, -348) * mm});
            skLineSegment(sketch, "E8.13.9.2", {"start": v(74.67, -348) * mm, "end": v(228.67, -348) * mm});
            skLineSegment(sketch, "E8.13.9.3", {"start": v(74.67, -194) * mm, "end": v(74.67, -348) * mm});
            skLineSegment(sketch, "E8.13.10.0", {"start": v(74.67, -350) * mm, "end": v(228.67, -350) * mm});
            skLineSegment(sketch, "E8.13.10.1", {"start": v(228.67, -350) * mm, "end": v(228.67, -504) * mm});
            skLineSegment(sketch, "E8.13.10.2", {"start": v(74.67, -504) * mm, "end": v(228.67, -504) * mm});
            skLineSegment(sketch, "E8.13.10.3", {"start": v(74.67, -350) * mm, "end": v(74.67, -504) * mm});
            skLineSegment(sketch, "E8.13.11.0", {"start": v(74.67, -506) * mm, "end": v(228.67, -506) * mm});
            skLineSegment(sketch, "E8.13.11.1", {"start": v(228.67, -506) * mm, "end": v(228.67, -660) * mm});
            skLineSegment(sketch, "E8.13.11.2", {"start": v(74.67, -660) * mm, "end": v(228.67, -660) * mm});
            skLineSegment(sketch, "E8.13.11.3", {"start": v(74.67, -506) * mm, "end": v(74.67, -660) * mm});
            skLineSegment(sketch, "E8.13.12.0", {"start": v(74.67, -662) * mm, "end": v(228.67, -662) * mm});
            skLineSegment(sketch, "E8.13.12.1", {"start": v(228.67, -662) * mm, "end": v(228.67, -816) * mm});
            skLineSegment(sketch, "E8.13.12.2", {"start": v(74.67, -816) * mm, "end": v(228.67, -816) * mm});
            skLineSegment(sketch, "E8.13.12.3", {"start": v(74.67, -662) * mm, "end": v(74.67, -816) * mm});
            skLineSegment(sketch, "E8.14.0.0", {"start": v(230.67, 1210) * mm, "end": v(384.67, 1210) * mm});
            skLineSegment(sketch, "E8.14.0.1", {"start": v(384.67, 1210) * mm, "end": v(384.67, 1056) * mm});
            skLineSegment(sketch, "E8.14.0.2", {"start": v(230.67, 1056) * mm, "end": v(384.67, 1056) * mm});
            skLineSegment(sketch, "E8.14.0.3", {"start": v(230.67, 1210) * mm, "end": v(230.67, 1056) * mm});
            skLineSegment(sketch, "E8.14.1.0", {"start": v(230.67, 1054) * mm, "end": v(384.67, 1054) * mm});
            skLineSegment(sketch, "E8.14.1.1", {"start": v(384.67, 1054) * mm, "end": v(384.67, 900) * mm});
            skLineSegment(sketch, "E8.14.1.2", {"start": v(230.67, 900) * mm, "end": v(384.67, 900) * mm});
            skLineSegment(sketch, "E8.14.1.3", {"start": v(230.67, 1054) * mm, "end": v(230.67, 900) * mm});
            skLineSegment(sketch, "E8.14.2.0", {"start": v(230.67, 898) * mm, "end": v(384.67, 898) * mm});
            skLineSegment(sketch, "E8.14.2.1", {"start": v(384.67, 898) * mm, "end": v(384.67, 744) * mm});
            skLineSegment(sketch, "E8.14.2.2", {"start": v(230.67, 744) * mm, "end": v(384.67, 744) * mm});
            skLineSegment(sketch, "E8.14.2.3", {"start": v(230.67, 898) * mm, "end": v(230.67, 744) * mm});
            skLineSegment(sketch, "E8.14.3.0", {"start": v(230.67, 742) * mm, "end": v(384.67, 742) * mm});
            skLineSegment(sketch, "E8.14.3.1", {"start": v(384.67, 742) * mm, "end": v(384.67, 588) * mm});
            skLineSegment(sketch, "E8.14.3.2", {"start": v(230.67, 588) * mm, "end": v(384.67, 588) * mm});
            skLineSegment(sketch, "E8.14.3.3", {"start": v(230.67, 742) * mm, "end": v(230.67, 588) * mm});
            skLineSegment(sketch, "E8.14.4.0", {"start": v(230.67, 586) * mm, "end": v(384.67, 586) * mm});
            skLineSegment(sketch, "E8.14.4.1", {"start": v(384.67, 586) * mm, "end": v(384.67, 432) * mm});
            skLineSegment(sketch, "E8.14.4.2", {"start": v(230.67, 432) * mm, "end": v(384.67, 432) * mm});
            skLineSegment(sketch, "E8.14.4.3", {"start": v(230.67, 586) * mm, "end": v(230.67, 432) * mm});
            skLineSegment(sketch, "E8.14.5.0", {"start": v(230.67, 430) * mm, "end": v(384.67, 430) * mm});
            skLineSegment(sketch, "E8.14.5.1", {"start": v(384.67, 430) * mm, "end": v(384.67, 276) * mm});
            skLineSegment(sketch, "E8.14.5.2", {"start": v(230.67, 276) * mm, "end": v(384.67, 276) * mm});
            skLineSegment(sketch, "E8.14.5.3", {"start": v(230.67, 430) * mm, "end": v(230.67, 276) * mm});
            skLineSegment(sketch, "E8.14.6.0", {"start": v(230.67, 274) * mm, "end": v(384.67, 274) * mm});
            skLineSegment(sketch, "E8.14.6.1", {"start": v(384.67, 274) * mm, "end": v(384.67, 120) * mm});
            skLineSegment(sketch, "E8.14.6.2", {"start": v(230.67, 120) * mm, "end": v(384.67, 120) * mm});
            skLineSegment(sketch, "E8.14.6.3", {"start": v(230.67, 274) * mm, "end": v(230.67, 120) * mm});
            skLineSegment(sketch, "E8.14.7.0", {"start": v(230.67, 118) * mm, "end": v(384.67, 118) * mm});
            skLineSegment(sketch, "E8.14.7.1", {"start": v(384.67, 118) * mm, "end": v(384.67, -36) * mm});
            skLineSegment(sketch, "E8.14.7.2", {"start": v(230.67, -36) * mm, "end": v(384.67, -36) * mm});
            skLineSegment(sketch, "E8.14.7.3", {"start": v(230.67, 118) * mm, "end": v(230.67, -36) * mm});
            skLineSegment(sketch, "E8.14.8.0", {"start": v(230.67, -38) * mm, "end": v(384.67, -38) * mm});
            skLineSegment(sketch, "E8.14.8.1", {"start": v(384.67, -38) * mm, "end": v(384.67, -192) * mm});
            skLineSegment(sketch, "E8.14.8.2", {"start": v(230.67, -192) * mm, "end": v(384.67, -192) * mm});
            skLineSegment(sketch, "E8.14.8.3", {"start": v(230.67, -38) * mm, "end": v(230.67, -192) * mm});
            skLineSegment(sketch, "E8.14.9.0", {"start": v(230.67, -194) * mm, "end": v(384.67, -194) * mm});
            skLineSegment(sketch, "E8.14.9.1", {"start": v(384.67, -194) * mm, "end": v(384.67, -348) * mm});
            skLineSegment(sketch, "E8.14.9.2", {"start": v(230.67, -348) * mm, "end": v(384.67, -348) * mm});
            skLineSegment(sketch, "E8.14.9.3", {"start": v(230.67, -194) * mm, "end": v(230.67, -348) * mm});
            skLineSegment(sketch, "E8.14.10.0", {"start": v(230.67, -350) * mm, "end": v(384.67, -350) * mm});
            skLineSegment(sketch, "E8.14.10.1", {"start": v(384.67, -350) * mm, "end": v(384.67, -504) * mm});
            skLineSegment(sketch, "E8.14.10.2", {"start": v(230.67, -504) * mm, "end": v(384.67, -504) * mm});
            skLineSegment(sketch, "E8.14.10.3", {"start": v(230.67, -350) * mm, "end": v(230.67, -504) * mm});
            skLineSegment(sketch, "E8.14.11.0", {"start": v(230.67, -506) * mm, "end": v(384.67, -506) * mm});
            skLineSegment(sketch, "E8.14.11.1", {"start": v(384.67, -506) * mm, "end": v(384.67, -660) * mm});
            skLineSegment(sketch, "E8.14.11.2", {"start": v(230.67, -660) * mm, "end": v(384.67, -660) * mm});
            skLineSegment(sketch, "E8.14.11.3", {"start": v(230.67, -506) * mm, "end": v(230.67, -660) * mm});
            skLineSegment(sketch, "E8.14.12.0", {"start": v(230.67, -662) * mm, "end": v(384.67, -662) * mm});
            skLineSegment(sketch, "E8.14.12.1", {"start": v(384.67, -662) * mm, "end": v(384.67, -816) * mm});
            skLineSegment(sketch, "E8.14.12.2", {"start": v(230.67, -816) * mm, "end": v(384.67, -816) * mm});
            skLineSegment(sketch, "E8.14.12.3", {"start": v(230.67, -662) * mm, "end": v(230.67, -816) * mm});
            skLineSegment(sketch, "E8.15.0.0", {"start": v(386.67, 1210) * mm, "end": v(540.67, 1210) * mm});
            skLineSegment(sketch, "E8.15.0.1", {"start": v(540.67, 1210) * mm, "end": v(540.67, 1056) * mm});
            skLineSegment(sketch, "E8.15.0.2", {"start": v(386.67, 1056) * mm, "end": v(540.67, 1056) * mm});
            skLineSegment(sketch, "E8.15.0.3", {"start": v(386.67, 1210) * mm, "end": v(386.67, 1056) * mm});
            skLineSegment(sketch, "E8.15.1.0", {"start": v(386.67, 1054) * mm, "end": v(540.67, 1054) * mm});
            skLineSegment(sketch, "E8.15.1.1", {"start": v(540.67, 1054) * mm, "end": v(540.67, 900) * mm});
            skLineSegment(sketch, "E8.15.1.2", {"start": v(386.67, 900) * mm, "end": v(540.67, 900) * mm});
            skLineSegment(sketch, "E8.15.1.3", {"start": v(386.67, 1054) * mm, "end": v(386.67, 900) * mm});
            skLineSegment(sketch, "E8.15.2.0", {"start": v(386.67, 898) * mm, "end": v(540.67, 898) * mm});
            skLineSegment(sketch, "E8.15.2.1", {"start": v(540.67, 898) * mm, "end": v(540.67, 744) * mm});
            skLineSegment(sketch, "E8.15.2.2", {"start": v(386.67, 744) * mm, "end": v(540.67, 744) * mm});
            skLineSegment(sketch, "E8.15.2.3", {"start": v(386.67, 898) * mm, "end": v(386.67, 744) * mm});
            skLineSegment(sketch, "E8.15.3.0", {"start": v(386.67, 742) * mm, "end": v(540.67, 742) * mm});
            skLineSegment(sketch, "E8.15.3.1", {"start": v(540.67, 742) * mm, "end": v(540.67, 588) * mm});
            skLineSegment(sketch, "E8.15.3.2", {"start": v(386.67, 588) * mm, "end": v(540.67, 588) * mm});
            skLineSegment(sketch, "E8.15.3.3", {"start": v(386.67, 742) * mm, "end": v(386.67, 588) * mm});
            skLineSegment(sketch, "E8.15.4.0", {"start": v(386.67, 586) * mm, "end": v(540.67, 586) * mm});
            skLineSegment(sketch, "E8.15.4.1", {"start": v(540.67, 586) * mm, "end": v(540.67, 432) * mm});
            skLineSegment(sketch, "E8.15.4.2", {"start": v(386.67, 432) * mm, "end": v(540.67, 432) * mm});
            skLineSegment(sketch, "E8.15.4.3", {"start": v(386.67, 586) * mm, "end": v(386.67, 432) * mm});
            skLineSegment(sketch, "E8.15.5.0", {"start": v(386.67, 430) * mm, "end": v(540.67, 430) * mm});
            skLineSegment(sketch, "E8.15.5.1", {"start": v(540.67, 430) * mm, "end": v(540.67, 276) * mm});
            skLineSegment(sketch, "E8.15.5.2", {"start": v(386.67, 276) * mm, "end": v(540.67, 276) * mm});
            skLineSegment(sketch, "E8.15.5.3", {"start": v(386.67, 430) * mm, "end": v(386.67, 276) * mm});
            skLineSegment(sketch, "E8.15.6.0", {"start": v(386.67, 274) * mm, "end": v(540.67, 274) * mm});
            skLineSegment(sketch, "E8.15.6.1", {"start": v(540.67, 274) * mm, "end": v(540.67, 120) * mm});
            skLineSegment(sketch, "E8.15.6.2", {"start": v(386.67, 120) * mm, "end": v(540.67, 120) * mm});
            skLineSegment(sketch, "E8.15.6.3", {"start": v(386.67, 274) * mm, "end": v(386.67, 120) * mm});
            skLineSegment(sketch, "E8.15.7.0", {"start": v(386.67, 118) * mm, "end": v(540.67, 118) * mm});
            skLineSegment(sketch, "E8.15.7.1", {"start": v(540.67, 118) * mm, "end": v(540.67, -36) * mm});
            skLineSegment(sketch, "E8.15.7.2", {"start": v(386.67, -36) * mm, "end": v(540.67, -36) * mm});
            skLineSegment(sketch, "E8.15.7.3", {"start": v(386.67, 118) * mm, "end": v(386.67, -36) * mm});
            skLineSegment(sketch, "E8.15.8.0", {"start": v(386.67, -38) * mm, "end": v(540.67, -38) * mm});
            skLineSegment(sketch, "E8.15.8.1", {"start": v(540.67, -38) * mm, "end": v(540.67, -192) * mm});
            skLineSegment(sketch, "E8.15.8.2", {"start": v(386.67, -192) * mm, "end": v(540.67, -192) * mm});
            skLineSegment(sketch, "E8.15.8.3", {"start": v(386.67, -38) * mm, "end": v(386.67, -192) * mm});
            skLineSegment(sketch, "E8.15.9.0", {"start": v(386.67, -194) * mm, "end": v(540.67, -194) * mm});
            skLineSegment(sketch, "E8.15.9.1", {"start": v(540.67, -194) * mm, "end": v(540.67, -348) * mm});
            skLineSegment(sketch, "E8.15.9.2", {"start": v(386.67, -348) * mm, "end": v(540.67, -348) * mm});
            skLineSegment(sketch, "E8.15.9.3", {"start": v(386.67, -194) * mm, "end": v(386.67, -348) * mm});
            skLineSegment(sketch, "E8.15.10.0", {"start": v(386.67, -350) * mm, "end": v(540.67, -350) * mm});
            skLineSegment(sketch, "E8.15.10.1", {"start": v(540.67, -350) * mm, "end": v(540.67, -504) * mm});
            skLineSegment(sketch, "E8.15.10.2", {"start": v(386.67, -504) * mm, "end": v(540.67, -504) * mm});
            skLineSegment(sketch, "E8.15.10.3", {"start": v(386.67, -350) * mm, "end": v(386.67, -504) * mm});
            skLineSegment(sketch, "E8.15.11.0", {"start": v(386.67, -506) * mm, "end": v(540.67, -506) * mm});
            skLineSegment(sketch, "E8.15.11.1", {"start": v(540.67, -506) * mm, "end": v(540.67, -660) * mm});
            skLineSegment(sketch, "E8.15.11.2", {"start": v(386.67, -660) * mm, "end": v(540.67, -660) * mm});
            skLineSegment(sketch, "E8.15.11.3", {"start": v(386.67, -506) * mm, "end": v(386.67, -660) * mm});
            skLineSegment(sketch, "E8.15.12.0", {"start": v(386.67, -662) * mm, "end": v(540.67, -662) * mm});
            skLineSegment(sketch, "E8.15.12.1", {"start": v(540.67, -662) * mm, "end": v(540.67, -816) * mm});
            skLineSegment(sketch, "E8.15.12.2", {"start": v(386.67, -816) * mm, "end": v(540.67, -816) * mm});
            skLineSegment(sketch, "E8.15.12.3", {"start": v(386.67, -662) * mm, "end": v(386.67, -816) * mm});
            skLineSegment(sketch, "E8.16.0.0", {"start": v(542.67, 1210) * mm, "end": v(696.67, 1210) * mm});
            skLineSegment(sketch, "E8.16.0.1", {"start": v(696.67, 1210) * mm, "end": v(696.67, 1056) * mm});
            skLineSegment(sketch, "E8.16.0.2", {"start": v(542.67, 1056) * mm, "end": v(696.67, 1056) * mm});
            skLineSegment(sketch, "E8.16.0.3", {"start": v(542.67, 1210) * mm, "end": v(542.67, 1056) * mm});
            skLineSegment(sketch, "E8.16.1.0", {"start": v(542.67, 1054) * mm, "end": v(696.67, 1054) * mm});
            skLineSegment(sketch, "E8.16.1.1", {"start": v(696.67, 1054) * mm, "end": v(696.67, 900) * mm});
            skLineSegment(sketch, "E8.16.1.2", {"start": v(542.67, 900) * mm, "end": v(696.67, 900) * mm});
            skLineSegment(sketch, "E8.16.1.3", {"start": v(542.67, 1054) * mm, "end": v(542.67, 900) * mm});
            skLineSegment(sketch, "E8.16.2.0", {"start": v(542.67, 898) * mm, "end": v(696.67, 898) * mm});
            skLineSegment(sketch, "E8.16.2.1", {"start": v(696.67, 898) * mm, "end": v(696.67, 744) * mm});
            skLineSegment(sketch, "E8.16.2.2", {"start": v(542.67, 744) * mm, "end": v(696.67, 744) * mm});
            skLineSegment(sketch, "E8.16.2.3", {"start": v(542.67, 898) * mm, "end": v(542.67, 744) * mm});
            skLineSegment(sketch, "E8.16.3.0", {"start": v(542.67, 742) * mm, "end": v(696.67, 742) * mm});
            skLineSegment(sketch, "E8.16.3.1", {"start": v(696.67, 742) * mm, "end": v(696.67, 588) * mm});
            skLineSegment(sketch, "E8.16.3.2", {"start": v(542.67, 588) * mm, "end": v(696.67, 588) * mm});
            skLineSegment(sketch, "E8.16.3.3", {"start": v(542.67, 742) * mm, "end": v(542.67, 588) * mm});
            skLineSegment(sketch, "E8.16.4.0", {"start": v(542.67, 586) * mm, "end": v(696.67, 586) * mm});
            skLineSegment(sketch, "E8.16.4.1", {"start": v(696.67, 586) * mm, "end": v(696.67, 432) * mm});
            skLineSegment(sketch, "E8.16.4.2", {"start": v(542.67, 432) * mm, "end": v(696.67, 432) * mm});
            skLineSegment(sketch, "E8.16.4.3", {"start": v(542.67, 586) * mm, "end": v(542.67, 432) * mm});
            skLineSegment(sketch, "E8.16.5.0", {"start": v(542.67, 430) * mm, "end": v(696.67, 430) * mm});
            skLineSegment(sketch, "E8.16.5.1", {"start": v(696.67, 430) * mm, "end": v(696.67, 276) * mm});
            skLineSegment(sketch, "E8.16.5.2", {"start": v(542.67, 276) * mm, "end": v(696.67, 276) * mm});
            skLineSegment(sketch, "E8.16.5.3", {"start": v(542.67, 430) * mm, "end": v(542.67, 276) * mm});
            skLineSegment(sketch, "E8.16.6.0", {"start": v(542.67, 274) * mm, "end": v(696.67, 274) * mm});
            skLineSegment(sketch, "E8.16.6.1", {"start": v(696.67, 274) * mm, "end": v(696.67, 120) * mm});
            skLineSegment(sketch, "E8.16.6.2", {"start": v(542.67, 120) * mm, "end": v(696.67, 120) * mm});
            skLineSegment(sketch, "E8.16.6.3", {"start": v(542.67, 274) * mm, "end": v(542.67, 120) * mm});
            skLineSegment(sketch, "E8.16.7.0", {"start": v(542.67, 118) * mm, "end": v(696.67, 118) * mm});
            skLineSegment(sketch, "E8.16.7.1", {"start": v(696.67, 118) * mm, "end": v(696.67, -36) * mm});
            skLineSegment(sketch, "E8.16.7.2", {"start": v(542.67, -36) * mm, "end": v(696.67, -36) * mm});
            skLineSegment(sketch, "E8.16.7.3", {"start": v(542.67, 118) * mm, "end": v(542.67, -36) * mm});
            skLineSegment(sketch, "E8.16.8.0", {"start": v(542.67, -38) * mm, "end": v(696.67, -38) * mm});
            skLineSegment(sketch, "E8.16.8.1", {"start": v(696.67, -38) * mm, "end": v(696.67, -192) * mm});
            skLineSegment(sketch, "E8.16.8.2", {"start": v(542.67, -192) * mm, "end": v(696.67, -192) * mm});
            skLineSegment(sketch, "E8.16.8.3", {"start": v(542.67, -38) * mm, "end": v(542.67, -192) * mm});
            skLineSegment(sketch, "E8.16.9.0", {"start": v(542.67, -194) * mm, "end": v(696.67, -194) * mm});
            skLineSegment(sketch, "E8.16.9.1", {"start": v(696.67, -194) * mm, "end": v(696.67, -348) * mm});
            skLineSegment(sketch, "E8.16.9.2", {"start": v(542.67, -348) * mm, "end": v(696.67, -348) * mm});
            skLineSegment(sketch, "E8.16.9.3", {"start": v(542.67, -194) * mm, "end": v(542.67, -348) * mm});
            skLineSegment(sketch, "E8.16.10.0", {"start": v(542.67, -350) * mm, "end": v(696.67, -350) * mm});
            skLineSegment(sketch, "E8.16.10.1", {"start": v(696.67, -350) * mm, "end": v(696.67, -504) * mm});
            skLineSegment(sketch, "E8.16.10.2", {"start": v(542.67, -504) * mm, "end": v(696.67, -504) * mm});
            skLineSegment(sketch, "E8.16.10.3", {"start": v(542.67, -350) * mm, "end": v(542.67, -504) * mm});
            skLineSegment(sketch, "E8.16.11.0", {"start": v(542.67, -506) * mm, "end": v(696.67, -506) * mm});
            skLineSegment(sketch, "E8.16.11.1", {"start": v(696.67, -506) * mm, "end": v(696.67, -660) * mm});
            skLineSegment(sketch, "E8.16.11.2", {"start": v(542.67, -660) * mm, "end": v(696.67, -660) * mm});
            skLineSegment(sketch, "E8.16.11.3", {"start": v(542.67, -506) * mm, "end": v(542.67, -660) * mm});
            skLineSegment(sketch, "E8.16.12.0", {"start": v(542.67, -662) * mm, "end": v(696.67, -662) * mm});
            skLineSegment(sketch, "E8.16.12.1", {"start": v(696.67, -662) * mm, "end": v(696.67, -816) * mm});
            skLineSegment(sketch, "E8.16.12.2", {"start": v(542.67, -816) * mm, "end": v(696.67, -816) * mm});
            skLineSegment(sketch, "E8.16.12.3", {"start": v(542.67, -662) * mm, "end": v(542.67, -816) * mm});
            skLineSegment(sketch, "E8.17.0.0", {"start": v(698.67, 1210) * mm, "end": v(852.67, 1210) * mm});
            skLineSegment(sketch, "E8.17.0.1", {"start": v(852.67, 1210) * mm, "end": v(852.67, 1056) * mm});
            skLineSegment(sketch, "E8.17.0.2", {"start": v(698.67, 1056) * mm, "end": v(852.67, 1056) * mm});
            skLineSegment(sketch, "E8.17.0.3", {"start": v(698.67, 1210) * mm, "end": v(698.67, 1056) * mm});
            skLineSegment(sketch, "E8.17.1.0", {"start": v(698.67, 1054) * mm, "end": v(852.67, 1054) * mm});
            skLineSegment(sketch, "E8.17.1.1", {"start": v(852.67, 1054) * mm, "end": v(852.67, 900) * mm});
            skLineSegment(sketch, "E8.17.1.2", {"start": v(698.67, 900) * mm, "end": v(852.67, 900) * mm});
            skLineSegment(sketch, "E8.17.1.3", {"start": v(698.67, 1054) * mm, "end": v(698.67, 900) * mm});
            skLineSegment(sketch, "E8.17.2.0", {"start": v(698.67, 898) * mm, "end": v(852.67, 898) * mm});
            skLineSegment(sketch, "E8.17.2.1", {"start": v(852.67, 898) * mm, "end": v(852.67, 744) * mm});
            skLineSegment(sketch, "E8.17.2.2", {"start": v(698.67, 744) * mm, "end": v(852.67, 744) * mm});
            skLineSegment(sketch, "E8.17.2.3", {"start": v(698.67, 898) * mm, "end": v(698.67, 744) * mm});
            skLineSegment(sketch, "E8.17.3.0", {"start": v(698.67, 742) * mm, "end": v(852.67, 742) * mm});
            skLineSegment(sketch, "E8.17.3.1", {"start": v(852.67, 742) * mm, "end": v(852.67, 588) * mm});
            skLineSegment(sketch, "E8.17.3.2", {"start": v(698.67, 588) * mm, "end": v(852.67, 588) * mm});
            skLineSegment(sketch, "E8.17.3.3", {"start": v(698.67, 742) * mm, "end": v(698.67, 588) * mm});
            skLineSegment(sketch, "E8.17.4.0", {"start": v(698.67, 586) * mm, "end": v(852.67, 586) * mm});
            skLineSegment(sketch, "E8.17.4.1", {"start": v(852.67, 586) * mm, "end": v(852.67, 432) * mm});
            skLineSegment(sketch, "E8.17.4.2", {"start": v(698.67, 432) * mm, "end": v(852.67, 432) * mm});
            skLineSegment(sketch, "E8.17.4.3", {"start": v(698.67, 586) * mm, "end": v(698.67, 432) * mm});
            skLineSegment(sketch, "E8.17.5.0", {"start": v(698.67, 430) * mm, "end": v(852.67, 430) * mm});
            skLineSegment(sketch, "E8.17.5.1", {"start": v(852.67, 430) * mm, "end": v(852.67, 276) * mm});
            skLineSegment(sketch, "E8.17.5.2", {"start": v(698.67, 276) * mm, "end": v(852.67, 276) * mm});
            skLineSegment(sketch, "E8.17.5.3", {"start": v(698.67, 430) * mm, "end": v(698.67, 276) * mm});
            skLineSegment(sketch, "E8.17.6.0", {"start": v(698.67, 274) * mm, "end": v(852.67, 274) * mm});
            skLineSegment(sketch, "E8.17.6.1", {"start": v(852.67, 274) * mm, "end": v(852.67, 120) * mm});
            skLineSegment(sketch, "E8.17.6.2", {"start": v(698.67, 120) * mm, "end": v(852.67, 120) * mm});
            skLineSegment(sketch, "E8.17.6.3", {"start": v(698.67, 274) * mm, "end": v(698.67, 120) * mm});
            skLineSegment(sketch, "E8.17.7.0", {"start": v(698.67, 118) * mm, "end": v(852.67, 118) * mm});
            skLineSegment(sketch, "E8.17.7.1", {"start": v(852.67, 118) * mm, "end": v(852.67, -36) * mm});
            skLineSegment(sketch, "E8.17.7.2", {"start": v(698.67, -36) * mm, "end": v(852.67, -36) * mm});
            skLineSegment(sketch, "E8.17.7.3", {"start": v(698.67, 118) * mm, "end": v(698.67, -36) * mm});
            skLineSegment(sketch, "E8.17.8.0", {"start": v(698.67, -38) * mm, "end": v(852.67, -38) * mm});
            skLineSegment(sketch, "E8.17.8.1", {"start": v(852.67, -38) * mm, "end": v(852.67, -192) * mm});
            skLineSegment(sketch, "E8.17.8.2", {"start": v(698.67, -192) * mm, "end": v(852.67, -192) * mm});
            skLineSegment(sketch, "E8.17.8.3", {"start": v(698.67, -38) * mm, "end": v(698.67, -192) * mm});
            skLineSegment(sketch, "E8.17.9.0", {"start": v(698.67, -194) * mm, "end": v(852.67, -194) * mm});
            skLineSegment(sketch, "E8.17.9.1", {"start": v(852.67, -194) * mm, "end": v(852.67, -348) * mm});
            skLineSegment(sketch, "E8.17.9.2", {"start": v(698.67, -348) * mm, "end": v(852.67, -348) * mm});
            skLineSegment(sketch, "E8.17.9.3", {"start": v(698.67, -194) * mm, "end": v(698.67, -348) * mm});
            skLineSegment(sketch, "E8.17.10.0", {"start": v(698.67, -350) * mm, "end": v(852.67, -350) * mm});
            skLineSegment(sketch, "E8.17.10.1", {"start": v(852.67, -350) * mm, "end": v(852.67, -504) * mm});
            skLineSegment(sketch, "E8.17.10.2", {"start": v(698.67, -504) * mm, "end": v(852.67, -504) * mm});
            skLineSegment(sketch, "E8.17.10.3", {"start": v(698.67, -350) * mm, "end": v(698.67, -504) * mm});
            skLineSegment(sketch, "E8.17.11.0", {"start": v(698.67, -506) * mm, "end": v(852.67, -506) * mm});
            skLineSegment(sketch, "E8.17.11.1", {"start": v(852.67, -506) * mm, "end": v(852.67, -660) * mm});
            skLineSegment(sketch, "E8.17.11.2", {"start": v(698.67, -660) * mm, "end": v(852.67, -660) * mm});
            skLineSegment(sketch, "E8.17.11.3", {"start": v(698.67, -506) * mm, "end": v(698.67, -660) * mm});
            skLineSegment(sketch, "E8.17.12.0", {"start": v(698.67, -662) * mm, "end": v(852.67, -662) * mm});
            skLineSegment(sketch, "E8.17.12.1", {"start": v(852.67, -662) * mm, "end": v(852.67, -816) * mm});
            skLineSegment(sketch, "E8.17.12.2", {"start": v(698.67, -816) * mm, "end": v(852.67, -816) * mm});
            skLineSegment(sketch, "E8.17.12.3", {"start": v(698.67, -662) * mm, "end": v(698.67, -816) * mm});
            skLineSegment(sketch, "E8.18.0.0", {"start": v(854.67, 1210) * mm, "end": v(1008.67, 1210) * mm});
            skLineSegment(sketch, "E8.18.0.1", {"start": v(1008.67, 1210) * mm, "end": v(1008.67, 1056) * mm});
            skLineSegment(sketch, "E8.18.0.2", {"start": v(854.67, 1056) * mm, "end": v(1008.67, 1056) * mm});
            skLineSegment(sketch, "E8.18.0.3", {"start": v(854.67, 1210) * mm, "end": v(854.67, 1056) * mm});
            skLineSegment(sketch, "E8.18.1.0", {"start": v(854.67, 1054) * mm, "end": v(1008.67, 1054) * mm});
            skLineSegment(sketch, "E8.18.1.1", {"start": v(1008.67, 1054) * mm, "end": v(1008.67, 900) * mm});
            skLineSegment(sketch, "E8.18.1.2", {"start": v(854.67, 900) * mm, "end": v(1008.67, 900) * mm});
            skLineSegment(sketch, "E8.18.1.3", {"start": v(854.67, 1054) * mm, "end": v(854.67, 900) * mm});
            skLineSegment(sketch, "E8.18.2.0", {"start": v(854.67, 898) * mm, "end": v(1008.67, 898) * mm});
            skLineSegment(sketch, "E8.18.2.1", {"start": v(1008.67, 898) * mm, "end": v(1008.67, 744) * mm});
            skLineSegment(sketch, "E8.18.2.2", {"start": v(854.67, 744) * mm, "end": v(1008.67, 744) * mm});
            skLineSegment(sketch, "E8.18.2.3", {"start": v(854.67, 898) * mm, "end": v(854.67, 744) * mm});
            skLineSegment(sketch, "E8.18.3.0", {"start": v(854.67, 742) * mm, "end": v(1008.67, 742) * mm});
            skLineSegment(sketch, "E8.18.3.1", {"start": v(1008.67, 742) * mm, "end": v(1008.67, 588) * mm});
            skLineSegment(sketch, "E8.18.3.2", {"start": v(854.67, 588) * mm, "end": v(1008.67, 588) * mm});
            skLineSegment(sketch, "E8.18.3.3", {"start": v(854.67, 742) * mm, "end": v(854.67, 588) * mm});
            skLineSegment(sketch, "E8.18.4.0", {"start": v(854.67, 586) * mm, "end": v(1008.67, 586) * mm});
            skLineSegment(sketch, "E8.18.4.1", {"start": v(1008.67, 586) * mm, "end": v(1008.67, 432) * mm});
            skLineSegment(sketch, "E8.18.4.2", {"start": v(854.67, 432) * mm, "end": v(1008.67, 432) * mm});
            skLineSegment(sketch, "E8.18.4.3", {"start": v(854.67, 586) * mm, "end": v(854.67, 432) * mm});
            skLineSegment(sketch, "E8.18.5.0", {"start": v(854.67, 430) * mm, "end": v(1008.67, 430) * mm});
            skLineSegment(sketch, "E8.18.5.1", {"start": v(1008.67, 430) * mm, "end": v(1008.67, 276) * mm});
            skLineSegment(sketch, "E8.18.5.2", {"start": v(854.67, 276) * mm, "end": v(1008.67, 276) * mm});
            skLineSegment(sketch, "E8.18.5.3", {"start": v(854.67, 430) * mm, "end": v(854.67, 276) * mm});
            skLineSegment(sketch, "E8.18.6.0", {"start": v(854.67, 274) * mm, "end": v(1008.67, 274) * mm});
            skLineSegment(sketch, "E8.18.6.1", {"start": v(1008.67, 274) * mm, "end": v(1008.67, 120) * mm});
            skLineSegment(sketch, "E8.18.6.2", {"start": v(854.67, 120) * mm, "end": v(1008.67, 120) * mm});
            skLineSegment(sketch, "E8.18.6.3", {"start": v(854.67, 274) * mm, "end": v(854.67, 120) * mm});
            skLineSegment(sketch, "E8.18.7.0", {"start": v(854.67, 118) * mm, "end": v(1008.67, 118) * mm});
            skLineSegment(sketch, "E8.18.7.1", {"start": v(1008.67, 118) * mm, "end": v(1008.67, -36) * mm});
            skLineSegment(sketch, "E8.18.7.2", {"start": v(854.67, -36) * mm, "end": v(1008.67, -36) * mm});
            skLineSegment(sketch, "E8.18.7.3", {"start": v(854.67, 118) * mm, "end": v(854.67, -36) * mm});
            skLineSegment(sketch, "E8.18.8.0", {"start": v(854.67, -38) * mm, "end": v(1008.67, -38) * mm});
            skLineSegment(sketch, "E8.18.8.1", {"start": v(1008.67, -38) * mm, "end": v(1008.67, -192) * mm});
            skLineSegment(sketch, "E8.18.8.2", {"start": v(854.67, -192) * mm, "end": v(1008.67, -192) * mm});
            skLineSegment(sketch, "E8.18.8.3", {"start": v(854.67, -38) * mm, "end": v(854.67, -192) * mm});
            skLineSegment(sketch, "E8.18.9.0", {"start": v(854.67, -194) * mm, "end": v(1008.67, -194) * mm});
            skLineSegment(sketch, "E8.18.9.1", {"start": v(1008.67, -194) * mm, "end": v(1008.67, -348) * mm});
            skLineSegment(sketch, "E8.18.9.2", {"start": v(854.67, -348) * mm, "end": v(1008.67, -348) * mm});
            skLineSegment(sketch, "E8.18.9.3", {"start": v(854.67, -194) * mm, "end": v(854.67, -348) * mm});
            skLineSegment(sketch, "E8.18.10.0", {"start": v(854.67, -350) * mm, "end": v(1008.67, -350) * mm});
            skLineSegment(sketch, "E8.18.10.1", {"start": v(1008.67, -350) * mm, "end": v(1008.67, -504) * mm});
            skLineSegment(sketch, "E8.18.10.2", {"start": v(854.67, -504) * mm, "end": v(1008.67, -504) * mm});
            skLineSegment(sketch, "E8.18.10.3", {"start": v(854.67, -350) * mm, "end": v(854.67, -504) * mm});
            skLineSegment(sketch, "E8.18.11.0", {"start": v(854.67, -506) * mm, "end": v(1008.67, -506) * mm});
            skLineSegment(sketch, "E8.18.11.1", {"start": v(1008.67, -506) * mm, "end": v(1008.67, -660) * mm});
            skLineSegment(sketch, "E8.18.11.2", {"start": v(854.67, -660) * mm, "end": v(1008.67, -660) * mm});
            skLineSegment(sketch, "E8.18.11.3", {"start": v(854.67, -506) * mm, "end": v(854.67, -660) * mm});
            skLineSegment(sketch, "E8.18.12.0", {"start": v(854.67, -662) * mm, "end": v(1008.67, -662) * mm});
            skLineSegment(sketch, "E8.18.12.1", {"start": v(1008.67, -662) * mm, "end": v(1008.67, -816) * mm});
            skLineSegment(sketch, "E8.18.12.2", {"start": v(854.67, -816) * mm, "end": v(1008.67, -816) * mm});
            skLineSegment(sketch, "E8.18.12.3", {"start": v(854.67, -662) * mm, "end": v(854.67, -816) * mm});
            skLineSegment(sketch, "E8.19.0.0", {"start": v(1010.67, 1210) * mm, "end": v(1164.67, 1210) * mm});
            skLineSegment(sketch, "E8.19.0.1", {"start": v(1164.67, 1210) * mm, "end": v(1164.67, 1056) * mm});
            skLineSegment(sketch, "E8.19.0.2", {"start": v(1010.67, 1056) * mm, "end": v(1164.67, 1056) * mm});
            skLineSegment(sketch, "E8.19.0.3", {"start": v(1010.67, 1210) * mm, "end": v(1010.67, 1056) * mm});
            skLineSegment(sketch, "E8.19.1.0", {"start": v(1010.67, 1054) * mm, "end": v(1164.67, 1054) * mm});
            skLineSegment(sketch, "E8.19.1.1", {"start": v(1164.67, 1054) * mm, "end": v(1164.67, 900) * mm});
            skLineSegment(sketch, "E8.19.1.2", {"start": v(1010.67, 900) * mm, "end": v(1164.67, 900) * mm});
            skLineSegment(sketch, "E8.19.1.3", {"start": v(1010.67, 1054) * mm, "end": v(1010.67, 900) * mm});
            skLineSegment(sketch, "E8.19.2.0", {"start": v(1010.67, 898) * mm, "end": v(1164.67, 898) * mm});
            skLineSegment(sketch, "E8.19.2.1", {"start": v(1164.67, 898) * mm, "end": v(1164.67, 744) * mm});
            skLineSegment(sketch, "E8.19.2.2", {"start": v(1010.67, 744) * mm, "end": v(1164.67, 744) * mm});
            skLineSegment(sketch, "E8.19.2.3", {"start": v(1010.67, 898) * mm, "end": v(1010.67, 744) * mm});
            skLineSegment(sketch, "E8.19.3.0", {"start": v(1010.67, 742) * mm, "end": v(1164.67, 742) * mm});
            skLineSegment(sketch, "E8.19.3.1", {"start": v(1164.67, 742) * mm, "end": v(1164.67, 588) * mm});
            skLineSegment(sketch, "E8.19.3.2", {"start": v(1010.67, 588) * mm, "end": v(1164.67, 588) * mm});
            skLineSegment(sketch, "E8.19.3.3", {"start": v(1010.67, 742) * mm, "end": v(1010.67, 588) * mm});
            skLineSegment(sketch, "E8.19.4.0", {"start": v(1010.67, 586) * mm, "end": v(1164.67, 586) * mm});
            skLineSegment(sketch, "E8.19.4.1", {"start": v(1164.67, 586) * mm, "end": v(1164.67, 432) * mm});
            skLineSegment(sketch, "E8.19.4.2", {"start": v(1010.67, 432) * mm, "end": v(1164.67, 432) * mm});
            skLineSegment(sketch, "E8.19.4.3", {"start": v(1010.67, 586) * mm, "end": v(1010.67, 432) * mm});
            skLineSegment(sketch, "E8.19.5.0", {"start": v(1010.67, 430) * mm, "end": v(1164.67, 430) * mm});
            skLineSegment(sketch, "E8.19.5.1", {"start": v(1164.67, 430) * mm, "end": v(1164.67, 276) * mm});
            skLineSegment(sketch, "E8.19.5.2", {"start": v(1010.67, 276) * mm, "end": v(1164.67, 276) * mm});
            skLineSegment(sketch, "E8.19.5.3", {"start": v(1010.67, 430) * mm, "end": v(1010.67, 276) * mm});
            skLineSegment(sketch, "E8.19.6.0", {"start": v(1010.67, 274) * mm, "end": v(1164.67, 274) * mm});
            skLineSegment(sketch, "E8.19.6.1", {"start": v(1164.67, 274) * mm, "end": v(1164.67, 120) * mm});
            skLineSegment(sketch, "E8.19.6.2", {"start": v(1010.67, 120) * mm, "end": v(1164.67, 120) * mm});
            skLineSegment(sketch, "E8.19.6.3", {"start": v(1010.67, 274) * mm, "end": v(1010.67, 120) * mm});
            skLineSegment(sketch, "E8.19.7.0", {"start": v(1010.67, 118) * mm, "end": v(1164.67, 118) * mm});
            skLineSegment(sketch, "E8.19.7.1", {"start": v(1164.67, 118) * mm, "end": v(1164.67, -36) * mm});
            skLineSegment(sketch, "E8.19.7.2", {"start": v(1010.67, -36) * mm, "end": v(1164.67, -36) * mm});
            skLineSegment(sketch, "E8.19.7.3", {"start": v(1010.67, 118) * mm, "end": v(1010.67, -36) * mm});
            skLineSegment(sketch, "E8.19.8.0", {"start": v(1010.67, -38) * mm, "end": v(1164.67, -38) * mm});
            skLineSegment(sketch, "E8.19.8.1", {"start": v(1164.67, -38) * mm, "end": v(1164.67, -192) * mm});
            skLineSegment(sketch, "E8.19.8.2", {"start": v(1010.67, -192) * mm, "end": v(1164.67, -192) * mm});
            skLineSegment(sketch, "E8.19.8.3", {"start": v(1010.67, -38) * mm, "end": v(1010.67, -192) * mm});
            skLineSegment(sketch, "E8.19.9.0", {"start": v(1010.67, -194) * mm, "end": v(1164.67, -194) * mm});
            skLineSegment(sketch, "E8.19.9.1", {"start": v(1164.67, -194) * mm, "end": v(1164.67, -348) * mm});
            skLineSegment(sketch, "E8.19.9.2", {"start": v(1010.67, -348) * mm, "end": v(1164.67, -348) * mm});
            skLineSegment(sketch, "E8.19.9.3", {"start": v(1010.67, -194) * mm, "end": v(1010.67, -348) * mm});
            skLineSegment(sketch, "E8.19.10.0", {"start": v(1010.67, -350) * mm, "end": v(1164.67, -350) * mm});
            skLineSegment(sketch, "E8.19.10.1", {"start": v(1164.67, -350) * mm, "end": v(1164.67, -504) * mm});
            skLineSegment(sketch, "E8.19.10.2", {"start": v(1010.67, -504) * mm, "end": v(1164.67, -504) * mm});
            skLineSegment(sketch, "E8.19.10.3", {"start": v(1010.67, -350) * mm, "end": v(1010.67, -504) * mm});
            skLineSegment(sketch, "E8.19.11.0", {"start": v(1010.67, -506) * mm, "end": v(1164.67, -506) * mm});
            skLineSegment(sketch, "E8.19.11.1", {"start": v(1164.67, -506) * mm, "end": v(1164.67, -660) * mm});
            skLineSegment(sketch, "E8.19.11.2", {"start": v(1010.67, -660) * mm, "end": v(1164.67, -660) * mm});
            skLineSegment(sketch, "E8.19.11.3", {"start": v(1010.67, -506) * mm, "end": v(1010.67, -660) * mm});
            skLineSegment(sketch, "E8.19.12.0", {"start": v(1010.67, -662) * mm, "end": v(1164.67, -662) * mm});
            skLineSegment(sketch, "E8.19.12.1", {"start": v(1164.67, -662) * mm, "end": v(1164.67, -816) * mm});
            skLineSegment(sketch, "E8.19.12.2", {"start": v(1010.67, -816) * mm, "end": v(1164.67, -816) * mm});
            skLineSegment(sketch, "E8.19.12.3", {"start": v(1010.67, -662) * mm, "end": v(1010.67, -816) * mm});
            skLineSegment(sketch, "E8.20.0.0", {"start": v(1166.67, 1210) * mm, "end": v(1320.67, 1210) * mm});
            skLineSegment(sketch, "E8.20.0.1", {"start": v(1320.67, 1210) * mm, "end": v(1320.67, 1056) * mm});
            skLineSegment(sketch, "E8.20.0.2", {"start": v(1166.67, 1056) * mm, "end": v(1320.67, 1056) * mm});
            skLineSegment(sketch, "E8.20.0.3", {"start": v(1166.67, 1210) * mm, "end": v(1166.67, 1056) * mm});
            skLineSegment(sketch, "E8.20.1.0", {"start": v(1166.67, 1054) * mm, "end": v(1320.67, 1054) * mm});
            skLineSegment(sketch, "E8.20.1.1", {"start": v(1320.67, 1054) * mm, "end": v(1320.67, 900) * mm});
            skLineSegment(sketch, "E8.20.1.2", {"start": v(1166.67, 900) * mm, "end": v(1320.67, 900) * mm});
            skLineSegment(sketch, "E8.20.1.3", {"start": v(1166.67, 1054) * mm, "end": v(1166.67, 900) * mm});
            skLineSegment(sketch, "E8.20.2.0", {"start": v(1166.67, 898) * mm, "end": v(1320.67, 898) * mm});
            skLineSegment(sketch, "E8.20.2.1", {"start": v(1320.67, 898) * mm, "end": v(1320.67, 744) * mm});
            skLineSegment(sketch, "E8.20.2.2", {"start": v(1166.67, 744) * mm, "end": v(1320.67, 744) * mm});
            skLineSegment(sketch, "E8.20.2.3", {"start": v(1166.67, 898) * mm, "end": v(1166.67, 744) * mm});
            skLineSegment(sketch, "E8.20.3.0", {"start": v(1166.67, 742) * mm, "end": v(1320.67, 742) * mm});
            skLineSegment(sketch, "E8.20.3.1", {"start": v(1320.67, 742) * mm, "end": v(1320.67, 588) * mm});
            skLineSegment(sketch, "E8.20.3.2", {"start": v(1166.67, 588) * mm, "end": v(1320.67, 588) * mm});
            skLineSegment(sketch, "E8.20.3.3", {"start": v(1166.67, 742) * mm, "end": v(1166.67, 588) * mm});
            skLineSegment(sketch, "E8.20.4.0", {"start": v(1166.67, 586) * mm, "end": v(1320.67, 586) * mm});
            skLineSegment(sketch, "E8.20.4.1", {"start": v(1320.67, 586) * mm, "end": v(1320.67, 432) * mm});
            skLineSegment(sketch, "E8.20.4.2", {"start": v(1166.67, 432) * mm, "end": v(1320.67, 432) * mm});
            skLineSegment(sketch, "E8.20.4.3", {"start": v(1166.67, 586) * mm, "end": v(1166.67, 432) * mm});
            skLineSegment(sketch, "E8.20.5.0", {"start": v(1166.67, 430) * mm, "end": v(1320.67, 430) * mm});
            skLineSegment(sketch, "E8.20.5.1", {"start": v(1320.67, 430) * mm, "end": v(1320.67, 276) * mm});
            skLineSegment(sketch, "E8.20.5.2", {"start": v(1166.67, 276) * mm, "end": v(1320.67, 276) * mm});
            skLineSegment(sketch, "E8.20.5.3", {"start": v(1166.67, 430) * mm, "end": v(1166.67, 276) * mm});
            skLineSegment(sketch, "E8.20.6.0", {"start": v(1166.67, 274) * mm, "end": v(1320.67, 274) * mm});
            skLineSegment(sketch, "E8.20.6.1", {"start": v(1320.67, 274) * mm, "end": v(1320.67, 120) * mm});
            skLineSegment(sketch, "E8.20.6.2", {"start": v(1166.67, 120) * mm, "end": v(1320.67, 120) * mm});
            skLineSegment(sketch, "E8.20.6.3", {"start": v(1166.67, 274) * mm, "end": v(1166.67, 120) * mm});
            skLineSegment(sketch, "E8.20.7.0", {"start": v(1166.67, 118) * mm, "end": v(1320.67, 118) * mm});
            skLineSegment(sketch, "E8.20.7.1", {"start": v(1320.67, 118) * mm, "end": v(1320.67, -36) * mm});
            skLineSegment(sketch, "E8.20.7.2", {"start": v(1166.67, -36) * mm, "end": v(1320.67, -36) * mm});
            skLineSegment(sketch, "E8.20.7.3", {"start": v(1166.67, 118) * mm, "end": v(1166.67, -36) * mm});
            skLineSegment(sketch, "E8.20.8.0", {"start": v(1166.67, -38) * mm, "end": v(1320.67, -38) * mm});
            skLineSegment(sketch, "E8.20.8.1", {"start": v(1320.67, -38) * mm, "end": v(1320.67, -192) * mm});
            skLineSegment(sketch, "E8.20.8.2", {"start": v(1166.67, -192) * mm, "end": v(1320.67, -192) * mm});
            skLineSegment(sketch, "E8.20.8.3", {"start": v(1166.67, -38) * mm, "end": v(1166.67, -192) * mm});
            skLineSegment(sketch, "E8.20.9.0", {"start": v(1166.67, -194) * mm, "end": v(1320.67, -194) * mm});
            skLineSegment(sketch, "E8.20.9.1", {"start": v(1320.67, -194) * mm, "end": v(1320.67, -348) * mm});
            skLineSegment(sketch, "E8.20.9.2", {"start": v(1166.67, -348) * mm, "end": v(1320.67, -348) * mm});
            skLineSegment(sketch, "E8.20.9.3", {"start": v(1166.67, -194) * mm, "end": v(1166.67, -348) * mm});
            skLineSegment(sketch, "E8.20.10.0", {"start": v(1166.67, -350) * mm, "end": v(1320.67, -350) * mm});
            skLineSegment(sketch, "E8.20.10.1", {"start": v(1320.67, -350) * mm, "end": v(1320.67, -504) * mm});
            skLineSegment(sketch, "E8.20.10.2", {"start": v(1166.67, -504) * mm, "end": v(1320.67, -504) * mm});
            skLineSegment(sketch, "E8.20.10.3", {"start": v(1166.67, -350) * mm, "end": v(1166.67, -504) * mm});
            skLineSegment(sketch, "E8.20.11.0", {"start": v(1166.67, -506) * mm, "end": v(1320.67, -506) * mm});
            skLineSegment(sketch, "E8.20.11.1", {"start": v(1320.67, -506) * mm, "end": v(1320.67, -660) * mm});
            skLineSegment(sketch, "E8.20.11.2", {"start": v(1166.67, -660) * mm, "end": v(1320.67, -660) * mm});
            skLineSegment(sketch, "E8.20.11.3", {"start": v(1166.67, -506) * mm, "end": v(1166.67, -660) * mm});
            skLineSegment(sketch, "E8.20.12.0", {"start": v(1166.67, -662) * mm, "end": v(1320.67, -662) * mm});
            skLineSegment(sketch, "E8.20.12.1", {"start": v(1320.67, -662) * mm, "end": v(1320.67, -816) * mm});
            skLineSegment(sketch, "E8.20.12.2", {"start": v(1166.67, -816) * mm, "end": v(1320.67, -816) * mm});
            skLineSegment(sketch, "E8.20.12.3", {"start": v(1166.67, -662) * mm, "end": v(1166.67, -816) * mm});
            skLineSegment(sketch, "E8.21.0.0", {"start": v(1322.67, 1210) * mm, "end": v(1476.67, 1210) * mm});
            skLineSegment(sketch, "E8.21.0.1", {"start": v(1476.67, 1210) * mm, "end": v(1476.67, 1056) * mm});
            skLineSegment(sketch, "E8.21.0.2", {"start": v(1322.67, 1056) * mm, "end": v(1476.67, 1056) * mm});
            skLineSegment(sketch, "E8.21.0.3", {"start": v(1322.67, 1210) * mm, "end": v(1322.67, 1056) * mm});
            skLineSegment(sketch, "E8.21.1.0", {"start": v(1322.67, 1054) * mm, "end": v(1476.67, 1054) * mm});
            skLineSegment(sketch, "E8.21.1.1", {"start": v(1476.67, 1054) * mm, "end": v(1476.67, 900) * mm});
            skLineSegment(sketch, "E8.21.1.2", {"start": v(1322.67, 900) * mm, "end": v(1476.67, 900) * mm});
            skLineSegment(sketch, "E8.21.1.3", {"start": v(1322.67, 1054) * mm, "end": v(1322.67, 900) * mm});
            skLineSegment(sketch, "E8.21.2.0", {"start": v(1322.67, 898) * mm, "end": v(1476.67, 898) * mm});
            skLineSegment(sketch, "E8.21.2.1", {"start": v(1476.67, 898) * mm, "end": v(1476.67, 744) * mm});
            skLineSegment(sketch, "E8.21.2.2", {"start": v(1322.67, 744) * mm, "end": v(1476.67, 744) * mm});
            skLineSegment(sketch, "E8.21.2.3", {"start": v(1322.67, 898) * mm, "end": v(1322.67, 744) * mm});
            skLineSegment(sketch, "E8.21.3.0", {"start": v(1322.67, 742) * mm, "end": v(1476.67, 742) * mm});
            skLineSegment(sketch, "E8.21.3.1", {"start": v(1476.67, 742) * mm, "end": v(1476.67, 588) * mm});
            skLineSegment(sketch, "E8.21.3.2", {"start": v(1322.67, 588) * mm, "end": v(1476.67, 588) * mm});
            skLineSegment(sketch, "E8.21.3.3", {"start": v(1322.67, 742) * mm, "end": v(1322.67, 588) * mm});
            skLineSegment(sketch, "E8.21.4.0", {"start": v(1322.67, 586) * mm, "end": v(1476.67, 586) * mm});
            skLineSegment(sketch, "E8.21.4.1", {"start": v(1476.67, 586) * mm, "end": v(1476.67, 432) * mm});
            skLineSegment(sketch, "E8.21.4.2", {"start": v(1322.67, 432) * mm, "end": v(1476.67, 432) * mm});
            skLineSegment(sketch, "E8.21.4.3", {"start": v(1322.67, 586) * mm, "end": v(1322.67, 432) * mm});
            skLineSegment(sketch, "E8.21.5.0", {"start": v(1322.67, 430) * mm, "end": v(1476.67, 430) * mm});
            skLineSegment(sketch, "E8.21.5.1", {"start": v(1476.67, 430) * mm, "end": v(1476.67, 276) * mm});
            skLineSegment(sketch, "E8.21.5.2", {"start": v(1322.67, 276) * mm, "end": v(1476.67, 276) * mm});
            skLineSegment(sketch, "E8.21.5.3", {"start": v(1322.67, 430) * mm, "end": v(1322.67, 276) * mm});
            skLineSegment(sketch, "E8.21.6.0", {"start": v(1322.67, 274) * mm, "end": v(1476.67, 274) * mm});
            skLineSegment(sketch, "E8.21.6.1", {"start": v(1476.67, 274) * mm, "end": v(1476.67, 120) * mm});
            skLineSegment(sketch, "E8.21.6.2", {"start": v(1322.67, 120) * mm, "end": v(1476.67, 120) * mm});
            skLineSegment(sketch, "E8.21.6.3", {"start": v(1322.67, 274) * mm, "end": v(1322.67, 120) * mm});
            skLineSegment(sketch, "E8.21.7.0", {"start": v(1322.67, 118) * mm, "end": v(1476.67, 118) * mm});
            skLineSegment(sketch, "E8.21.7.1", {"start": v(1476.67, 118) * mm, "end": v(1476.67, -36) * mm});
            skLineSegment(sketch, "E8.21.7.2", {"start": v(1322.67, -36) * mm, "end": v(1476.67, -36) * mm});
            skLineSegment(sketch, "E8.21.7.3", {"start": v(1322.67, 118) * mm, "end": v(1322.67, -36) * mm});
            skLineSegment(sketch, "E8.21.8.0", {"start": v(1322.67, -38) * mm, "end": v(1476.67, -38) * mm});
            skLineSegment(sketch, "E8.21.8.1", {"start": v(1476.67, -38) * mm, "end": v(1476.67, -192) * mm});
            skLineSegment(sketch, "E8.21.8.2", {"start": v(1322.67, -192) * mm, "end": v(1476.67, -192) * mm});
            skLineSegment(sketch, "E8.21.8.3", {"start": v(1322.67, -38) * mm, "end": v(1322.67, -192) * mm});
            skLineSegment(sketch, "E8.21.9.0", {"start": v(1322.67, -194) * mm, "end": v(1476.67, -194) * mm});
            skLineSegment(sketch, "E8.21.9.1", {"start": v(1476.67, -194) * mm, "end": v(1476.67, -348) * mm});
            skLineSegment(sketch, "E8.21.9.2", {"start": v(1322.67, -348) * mm, "end": v(1476.67, -348) * mm});
            skLineSegment(sketch, "E8.21.9.3", {"start": v(1322.67, -194) * mm, "end": v(1322.67, -348) * mm});
            skLineSegment(sketch, "E8.21.10.0", {"start": v(1322.67, -350) * mm, "end": v(1476.67, -350) * mm});
            skLineSegment(sketch, "E8.21.10.1", {"start": v(1476.67, -350) * mm, "end": v(1476.67, -504) * mm});
            skLineSegment(sketch, "E8.21.10.2", {"start": v(1322.67, -504) * mm, "end": v(1476.67, -504) * mm});
            skLineSegment(sketch, "E8.21.10.3", {"start": v(1322.67, -350) * mm, "end": v(1322.67, -504) * mm});
            skLineSegment(sketch, "E8.21.11.0", {"start": v(1322.67, -506) * mm, "end": v(1476.67, -506) * mm});
            skLineSegment(sketch, "E8.21.11.1", {"start": v(1476.67, -506) * mm, "end": v(1476.67, -660) * mm});
            skLineSegment(sketch, "E8.21.11.2", {"start": v(1322.67, -660) * mm, "end": v(1476.67, -660) * mm});
            skLineSegment(sketch, "E8.21.11.3", {"start": v(1322.67, -506) * mm, "end": v(1322.67, -660) * mm});
            skLineSegment(sketch, "E8.21.12.0", {"start": v(1322.67, -662) * mm, "end": v(1476.67, -662) * mm});
            skLineSegment(sketch, "E8.21.12.1", {"start": v(1476.67, -662) * mm, "end": v(1476.67, -816) * mm});
            skLineSegment(sketch, "E8.21.12.2", {"start": v(1322.67, -816) * mm, "end": v(1476.67, -816) * mm});
            skLineSegment(sketch, "E8.21.12.3", {"start": v(1322.67, -662) * mm, "end": v(1322.67, -816) * mm});
            skLineSegment(sketch, "E8.22.0.0", {"start": v(1478.67, 1210) * mm, "end": v(1632.67, 1210) * mm});
            skLineSegment(sketch, "E8.22.0.1", {"start": v(1632.67, 1210) * mm, "end": v(1632.67, 1056) * mm});
            skLineSegment(sketch, "E8.22.0.2", {"start": v(1478.67, 1056) * mm, "end": v(1632.67, 1056) * mm});
            skLineSegment(sketch, "E8.22.0.3", {"start": v(1478.67, 1210) * mm, "end": v(1478.67, 1056) * mm});
            skLineSegment(sketch, "E8.22.1.0", {"start": v(1478.67, 1054) * mm, "end": v(1632.67, 1054) * mm});
            skLineSegment(sketch, "E8.22.1.1", {"start": v(1632.67, 1054) * mm, "end": v(1632.67, 900) * mm});
            skLineSegment(sketch, "E8.22.1.2", {"start": v(1478.67, 900) * mm, "end": v(1632.67, 900) * mm});
            skLineSegment(sketch, "E8.22.1.3", {"start": v(1478.67, 1054) * mm, "end": v(1478.67, 900) * mm});
            skLineSegment(sketch, "E8.22.2.0", {"start": v(1478.67, 898) * mm, "end": v(1632.67, 898) * mm});
            skLineSegment(sketch, "E8.22.2.1", {"start": v(1632.67, 898) * mm, "end": v(1632.67, 744) * mm});
            skLineSegment(sketch, "E8.22.2.2", {"start": v(1478.67, 744) * mm, "end": v(1632.67, 744) * mm});
            skLineSegment(sketch, "E8.22.2.3", {"start": v(1478.67, 898) * mm, "end": v(1478.67, 744) * mm});
            skLineSegment(sketch, "E8.22.3.0", {"start": v(1478.67, 742) * mm, "end": v(1632.67, 742) * mm});
            skLineSegment(sketch, "E8.22.3.1", {"start": v(1632.67, 742) * mm, "end": v(1632.67, 588) * mm});
            skLineSegment(sketch, "E8.22.3.2", {"start": v(1478.67, 588) * mm, "end": v(1632.67, 588) * mm});
            skLineSegment(sketch, "E8.22.3.3", {"start": v(1478.67, 742) * mm, "end": v(1478.67, 588) * mm});
            skLineSegment(sketch, "E8.22.4.0", {"start": v(1478.67, 586) * mm, "end": v(1632.67, 586) * mm});
            skLineSegment(sketch, "E8.22.4.1", {"start": v(1632.67, 586) * mm, "end": v(1632.67, 432) * mm});
            skLineSegment(sketch, "E8.22.4.2", {"start": v(1478.67, 432) * mm, "end": v(1632.67, 432) * mm});
            skLineSegment(sketch, "E8.22.4.3", {"start": v(1478.67, 586) * mm, "end": v(1478.67, 432) * mm});
            skLineSegment(sketch, "E8.22.5.0", {"start": v(1478.67, 430) * mm, "end": v(1632.67, 430) * mm});
            skLineSegment(sketch, "E8.22.5.1", {"start": v(1632.67, 430) * mm, "end": v(1632.67, 276) * mm});
            skLineSegment(sketch, "E8.22.5.2", {"start": v(1478.67, 276) * mm, "end": v(1632.67, 276) * mm});
            skLineSegment(sketch, "E8.22.5.3", {"start": v(1478.67, 430) * mm, "end": v(1478.67, 276) * mm});
            skLineSegment(sketch, "E8.22.6.0", {"start": v(1478.67, 274) * mm, "end": v(1632.67, 274) * mm});
            skLineSegment(sketch, "E8.22.6.1", {"start": v(1632.67, 274) * mm, "end": v(1632.67, 120) * mm});
            skLineSegment(sketch, "E8.22.6.2", {"start": v(1478.67, 120) * mm, "end": v(1632.67, 120) * mm});
            skLineSegment(sketch, "E8.22.6.3", {"start": v(1478.67, 274) * mm, "end": v(1478.67, 120) * mm});
            skLineSegment(sketch, "E8.22.7.0", {"start": v(1478.67, 118) * mm, "end": v(1632.67, 118) * mm});
            skLineSegment(sketch, "E8.22.7.1", {"start": v(1632.67, 118) * mm, "end": v(1632.67, -36) * mm});
            skLineSegment(sketch, "E8.22.7.2", {"start": v(1478.67, -36) * mm, "end": v(1632.67, -36) * mm});
            skLineSegment(sketch, "E8.22.7.3", {"start": v(1478.67, 118) * mm, "end": v(1478.67, -36) * mm});
            skLineSegment(sketch, "E8.22.8.0", {"start": v(1478.67, -38) * mm, "end": v(1632.67, -38) * mm});
            skLineSegment(sketch, "E8.22.8.1", {"start": v(1632.67, -38) * mm, "end": v(1632.67, -192) * mm});
            skLineSegment(sketch, "E8.22.8.2", {"start": v(1478.67, -192) * mm, "end": v(1632.67, -192) * mm});
            skLineSegment(sketch, "E8.22.8.3", {"start": v(1478.67, -38) * mm, "end": v(1478.67, -192) * mm});
            skLineSegment(sketch, "E8.22.9.0", {"start": v(1478.67, -194) * mm, "end": v(1632.67, -194) * mm});
            skLineSegment(sketch, "E8.22.9.1", {"start": v(1632.67, -194) * mm, "end": v(1632.67, -348) * mm});
            skLineSegment(sketch, "E8.22.9.2", {"start": v(1478.67, -348) * mm, "end": v(1632.67, -348) * mm});
            skLineSegment(sketch, "E8.22.9.3", {"start": v(1478.67, -194) * mm, "end": v(1478.67, -348) * mm});
            skLineSegment(sketch, "E8.22.10.0", {"start": v(1478.67, -350) * mm, "end": v(1632.67, -350) * mm});
            skLineSegment(sketch, "E8.22.10.1", {"start": v(1632.67, -350) * mm, "end": v(1632.67, -504) * mm});
            skLineSegment(sketch, "E8.22.10.2", {"start": v(1478.67, -504) * mm, "end": v(1632.67, -504) * mm});
            skLineSegment(sketch, "E8.22.10.3", {"start": v(1478.67, -350) * mm, "end": v(1478.67, -504) * mm});
            skLineSegment(sketch, "E8.22.11.0", {"start": v(1478.67, -506) * mm, "end": v(1632.67, -506) * mm});
            skLineSegment(sketch, "E8.22.11.1", {"start": v(1632.67, -506) * mm, "end": v(1632.67, -660) * mm});
            skLineSegment(sketch, "E8.22.11.2", {"start": v(1478.67, -660) * mm, "end": v(1632.67, -660) * mm});
            skLineSegment(sketch, "E8.22.11.3", {"start": v(1478.67, -506) * mm, "end": v(1478.67, -660) * mm});
            skLineSegment(sketch, "E8.22.12.0", {"start": v(1478.67, -662) * mm, "end": v(1632.67, -662) * mm});
            skLineSegment(sketch, "E8.22.12.1", {"start": v(1632.67, -662) * mm, "end": v(1632.67, -816) * mm});
            skLineSegment(sketch, "E8.22.12.2", {"start": v(1478.67, -816) * mm, "end": v(1632.67, -816) * mm});
            skLineSegment(sketch, "E8.22.12.3", {"start": v(1478.67, -662) * mm, "end": v(1478.67, -816) * mm});
            skLineSegment(sketch, "E8.23.0.0", {"start": v(1634.67, 1210) * mm, "end": v(1788.67, 1210) * mm});
            skLineSegment(sketch, "E8.23.0.1", {"start": v(1788.67, 1210) * mm, "end": v(1788.67, 1056) * mm});
            skLineSegment(sketch, "E8.23.0.2", {"start": v(1634.67, 1056) * mm, "end": v(1788.67, 1056) * mm});
            skLineSegment(sketch, "E8.23.0.3", {"start": v(1634.67, 1210) * mm, "end": v(1634.67, 1056) * mm});
            skLineSegment(sketch, "E8.23.1.0", {"start": v(1634.67, 1054) * mm, "end": v(1788.67, 1054) * mm});
            skLineSegment(sketch, "E8.23.1.1", {"start": v(1788.67, 1054) * mm, "end": v(1788.67, 900) * mm});
            skLineSegment(sketch, "E8.23.1.2", {"start": v(1634.67, 900) * mm, "end": v(1788.67, 900) * mm});
            skLineSegment(sketch, "E8.23.1.3", {"start": v(1634.67, 1054) * mm, "end": v(1634.67, 900) * mm});
            skLineSegment(sketch, "E8.23.2.0", {"start": v(1634.67, 898) * mm, "end": v(1788.67, 898) * mm});
            skLineSegment(sketch, "E8.23.2.1", {"start": v(1788.67, 898) * mm, "end": v(1788.67, 744) * mm});
            skLineSegment(sketch, "E8.23.2.2", {"start": v(1634.67, 744) * mm, "end": v(1788.67, 744) * mm});
            skLineSegment(sketch, "E8.23.2.3", {"start": v(1634.67, 898) * mm, "end": v(1634.67, 744) * mm});
            skLineSegment(sketch, "E8.23.3.0", {"start": v(1634.67, 742) * mm, "end": v(1788.67, 742) * mm});
            skLineSegment(sketch, "E8.23.3.1", {"start": v(1788.67, 742) * mm, "end": v(1788.67, 588) * mm});
            skLineSegment(sketch, "E8.23.3.2", {"start": v(1634.67, 588) * mm, "end": v(1788.67, 588) * mm});
            skLineSegment(sketch, "E8.23.3.3", {"start": v(1634.67, 742) * mm, "end": v(1634.67, 588) * mm});
            skLineSegment(sketch, "E8.23.4.0", {"start": v(1634.67, 586) * mm, "end": v(1788.67, 586) * mm});
            skLineSegment(sketch, "E8.23.4.1", {"start": v(1788.67, 586) * mm, "end": v(1788.67, 432) * mm});
            skLineSegment(sketch, "E8.23.4.2", {"start": v(1634.67, 432) * mm, "end": v(1788.67, 432) * mm});
            skLineSegment(sketch, "E8.23.4.3", {"start": v(1634.67, 586) * mm, "end": v(1634.67, 432) * mm});
            skLineSegment(sketch, "E8.23.5.0", {"start": v(1634.67, 430) * mm, "end": v(1788.67, 430) * mm});
            skLineSegment(sketch, "E8.23.5.1", {"start": v(1788.67, 430) * mm, "end": v(1788.67, 276) * mm});
            skLineSegment(sketch, "E8.23.5.2", {"start": v(1634.67, 276) * mm, "end": v(1788.67, 276) * mm});
            skLineSegment(sketch, "E8.23.5.3", {"start": v(1634.67, 430) * mm, "end": v(1634.67, 276) * mm});
            skLineSegment(sketch, "E8.23.6.0", {"start": v(1634.67, 274) * mm, "end": v(1788.67, 274) * mm});
            skLineSegment(sketch, "E8.23.6.1", {"start": v(1788.67, 274) * mm, "end": v(1788.67, 120) * mm});
            skLineSegment(sketch, "E8.23.6.2", {"start": v(1634.67, 120) * mm, "end": v(1788.67, 120) * mm});
            skLineSegment(sketch, "E8.23.6.3", {"start": v(1634.67, 274) * mm, "end": v(1634.67, 120) * mm});
            skLineSegment(sketch, "E8.23.7.0", {"start": v(1634.67, 118) * mm, "end": v(1788.67, 118) * mm});
            skLineSegment(sketch, "E8.23.7.1", {"start": v(1788.67, 118) * mm, "end": v(1788.67, -36) * mm});
            skLineSegment(sketch, "E8.23.7.2", {"start": v(1634.67, -36) * mm, "end": v(1788.67, -36) * mm});
            skLineSegment(sketch, "E8.23.7.3", {"start": v(1634.67, 118) * mm, "end": v(1634.67, -36) * mm});
            skLineSegment(sketch, "E8.23.8.0", {"start": v(1634.67, -38) * mm, "end": v(1788.67, -38) * mm});
            skLineSegment(sketch, "E8.23.8.1", {"start": v(1788.67, -38) * mm, "end": v(1788.67, -192) * mm});
            skLineSegment(sketch, "E8.23.8.2", {"start": v(1634.67, -192) * mm, "end": v(1788.67, -192) * mm});
            skLineSegment(sketch, "E8.23.8.3", {"start": v(1634.67, -38) * mm, "end": v(1634.67, -192) * mm});
            skLineSegment(sketch, "E8.23.9.0", {"start": v(1634.67, -194) * mm, "end": v(1788.67, -194) * mm});
            skLineSegment(sketch, "E8.23.9.1", {"start": v(1788.67, -194) * mm, "end": v(1788.67, -348) * mm});
            skLineSegment(sketch, "E8.23.9.2", {"start": v(1634.67, -348) * mm, "end": v(1788.67, -348) * mm});
            skLineSegment(sketch, "E8.23.9.3", {"start": v(1634.67, -194) * mm, "end": v(1634.67, -348) * mm});
            skLineSegment(sketch, "E8.23.10.0", {"start": v(1634.67, -350) * mm, "end": v(1788.67, -350) * mm});
            skLineSegment(sketch, "E8.23.10.1", {"start": v(1788.67, -350) * mm, "end": v(1788.67, -504) * mm});
            skLineSegment(sketch, "E8.23.10.2", {"start": v(1634.67, -504) * mm, "end": v(1788.67, -504) * mm});
            skLineSegment(sketch, "E8.23.10.3", {"start": v(1634.67, -350) * mm, "end": v(1634.67, -504) * mm});
            skLineSegment(sketch, "E8.23.11.0", {"start": v(1634.67, -506) * mm, "end": v(1788.67, -506) * mm});
            skLineSegment(sketch, "E8.23.11.1", {"start": v(1788.67, -506) * mm, "end": v(1788.67, -660) * mm});
            skLineSegment(sketch, "E8.23.11.2", {"start": v(1634.67, -660) * mm, "end": v(1788.67, -660) * mm});
            skLineSegment(sketch, "E8.23.11.3", {"start": v(1634.67, -506) * mm, "end": v(1634.67, -660) * mm});
            skLineSegment(sketch, "E8.23.12.0", {"start": v(1634.67, -662) * mm, "end": v(1788.67, -662) * mm});
            skLineSegment(sketch, "E8.23.12.1", {"start": v(1788.67, -662) * mm, "end": v(1788.67, -816) * mm});
            skLineSegment(sketch, "E8.23.12.2", {"start": v(1634.67, -816) * mm, "end": v(1788.67, -816) * mm});
            skLineSegment(sketch, "E8.23.12.3", {"start": v(1634.67, -662) * mm, "end": v(1634.67, -816) * mm});
            skLineSegment(sketch, "E8.24.0.0", {"start": v(1790.67, 1210) * mm, "end": v(1944.67, 1210) * mm});
            skLineSegment(sketch, "E8.24.0.1", {"start": v(1944.67, 1210) * mm, "end": v(1944.67, 1056) * mm});
            skLineSegment(sketch, "E8.24.0.2", {"start": v(1790.67, 1056) * mm, "end": v(1944.67, 1056) * mm});
            skLineSegment(sketch, "E8.24.0.3", {"start": v(1790.67, 1210) * mm, "end": v(1790.67, 1056) * mm});
            skLineSegment(sketch, "E8.24.1.0", {"start": v(1790.67, 1054) * mm, "end": v(1944.67, 1054) * mm});
            skLineSegment(sketch, "E8.24.1.1", {"start": v(1944.67, 1054) * mm, "end": v(1944.67, 900) * mm});
            skLineSegment(sketch, "E8.24.1.2", {"start": v(1790.67, 900) * mm, "end": v(1944.67, 900) * mm});
            skLineSegment(sketch, "E8.24.1.3", {"start": v(1790.67, 1054) * mm, "end": v(1790.67, 900) * mm});
            skLineSegment(sketch, "E8.24.2.0", {"start": v(1790.67, 898) * mm, "end": v(1944.67, 898) * mm});
            skLineSegment(sketch, "E8.24.2.1", {"start": v(1944.67, 898) * mm, "end": v(1944.67, 744) * mm});
            skLineSegment(sketch, "E8.24.2.2", {"start": v(1790.67, 744) * mm, "end": v(1944.67, 744) * mm});
            skLineSegment(sketch, "E8.24.2.3", {"start": v(1790.67, 898) * mm, "end": v(1790.67, 744) * mm});
            skLineSegment(sketch, "E8.24.3.0", {"start": v(1790.67, 742) * mm, "end": v(1944.67, 742) * mm});
            skLineSegment(sketch, "E8.24.3.1", {"start": v(1944.67, 742) * mm, "end": v(1944.67, 588) * mm});
            skLineSegment(sketch, "E8.24.3.2", {"start": v(1790.67, 588) * mm, "end": v(1944.67, 588) * mm});
            skLineSegment(sketch, "E8.24.3.3", {"start": v(1790.67, 742) * mm, "end": v(1790.67, 588) * mm});
            skLineSegment(sketch, "E8.24.4.0", {"start": v(1790.67, 586) * mm, "end": v(1944.67, 586) * mm});
            skLineSegment(sketch, "E8.24.4.1", {"start": v(1944.67, 586) * mm, "end": v(1944.67, 432) * mm});
            skLineSegment(sketch, "E8.24.4.2", {"start": v(1790.67, 432) * mm, "end": v(1944.67, 432) * mm});
            skLineSegment(sketch, "E8.24.4.3", {"start": v(1790.67, 586) * mm, "end": v(1790.67, 432) * mm});
            skLineSegment(sketch, "E8.24.5.0", {"start": v(1790.67, 430) * mm, "end": v(1944.67, 430) * mm});
            skLineSegment(sketch, "E8.24.5.1", {"start": v(1944.67, 430) * mm, "end": v(1944.67, 276) * mm});
            skLineSegment(sketch, "E8.24.5.2", {"start": v(1790.67, 276) * mm, "end": v(1944.67, 276) * mm});
            skLineSegment(sketch, "E8.24.5.3", {"start": v(1790.67, 430) * mm, "end": v(1790.67, 276) * mm});
            skLineSegment(sketch, "E8.24.6.0", {"start": v(1790.67, 274) * mm, "end": v(1944.67, 274) * mm});
            skLineSegment(sketch, "E8.24.6.1", {"start": v(1944.67, 274) * mm, "end": v(1944.67, 120) * mm});
            skLineSegment(sketch, "E8.24.6.2", {"start": v(1790.67, 120) * mm, "end": v(1944.67, 120) * mm});
            skLineSegment(sketch, "E8.24.6.3", {"start": v(1790.67, 274) * mm, "end": v(1790.67, 120) * mm});
            skLineSegment(sketch, "E8.24.7.0", {"start": v(1790.67, 118) * mm, "end": v(1944.67, 118) * mm});
            skLineSegment(sketch, "E8.24.7.1", {"start": v(1944.67, 118) * mm, "end": v(1944.67, -36) * mm});
            skLineSegment(sketch, "E8.24.7.2", {"start": v(1790.67, -36) * mm, "end": v(1944.67, -36) * mm});
            skLineSegment(sketch, "E8.24.7.3", {"start": v(1790.67, 118) * mm, "end": v(1790.67, -36) * mm});
            skLineSegment(sketch, "E8.24.8.0", {"start": v(1790.67, -38) * mm, "end": v(1944.67, -38) * mm});
            skLineSegment(sketch, "E8.24.8.1", {"start": v(1944.67, -38) * mm, "end": v(1944.67, -192) * mm});
            skLineSegment(sketch, "E8.24.8.2", {"start": v(1790.67, -192) * mm, "end": v(1944.67, -192) * mm});
            skLineSegment(sketch, "E8.24.8.3", {"start": v(1790.67, -38) * mm, "end": v(1790.67, -192) * mm});
            skLineSegment(sketch, "E8.24.9.0", {"start": v(1790.67, -194) * mm, "end": v(1944.67, -194) * mm});
            skLineSegment(sketch, "E8.24.9.1", {"start": v(1944.67, -194) * mm, "end": v(1944.67, -348) * mm});
            skLineSegment(sketch, "E8.24.9.2", {"start": v(1790.67, -348) * mm, "end": v(1944.67, -348) * mm});
            skLineSegment(sketch, "E8.24.9.3", {"start": v(1790.67, -194) * mm, "end": v(1790.67, -348) * mm});
            skLineSegment(sketch, "E8.24.10.0", {"start": v(1790.67, -350) * mm, "end": v(1944.67, -350) * mm});
            skLineSegment(sketch, "E8.24.10.1", {"start": v(1944.67, -350) * mm, "end": v(1944.67, -504) * mm});
            skLineSegment(sketch, "E8.24.10.2", {"start": v(1790.67, -504) * mm, "end": v(1944.67, -504) * mm});
            skLineSegment(sketch, "E8.24.10.3", {"start": v(1790.67, -350) * mm, "end": v(1790.67, -504) * mm});
            skLineSegment(sketch, "E8.24.11.0", {"start": v(1790.67, -506) * mm, "end": v(1944.67, -506) * mm});
            skLineSegment(sketch, "E8.24.11.1", {"start": v(1944.67, -506) * mm, "end": v(1944.67, -660) * mm});
            skLineSegment(sketch, "E8.24.11.2", {"start": v(1790.67, -660) * mm, "end": v(1944.67, -660) * mm});
            skLineSegment(sketch, "E8.24.11.3", {"start": v(1790.67, -506) * mm, "end": v(1790.67, -660) * mm});
            skLineSegment(sketch, "E8.24.12.0", {"start": v(1790.67, -662) * mm, "end": v(1944.67, -662) * mm});
            skLineSegment(sketch, "E8.24.12.1", {"start": v(1944.67, -662) * mm, "end": v(1944.67, -816) * mm});
            skLineSegment(sketch, "E8.24.12.2", {"start": v(1790.67, -816) * mm, "end": v(1944.67, -816) * mm});
            skLineSegment(sketch, "E8.24.12.3", {"start": v(1790.67, -662) * mm, "end": v(1790.67, -816) * mm});
            skLineSegment(sketch, "E8.25.0.0", {"start": v(1946.67, 1210) * mm, "end": v(2100.67, 1210) * mm});
            skLineSegment(sketch, "E8.25.0.1", {"start": v(2100.67, 1210) * mm, "end": v(2100.67, 1056) * mm});
            skLineSegment(sketch, "E8.25.0.2", {"start": v(1946.67, 1056) * mm, "end": v(2100.67, 1056) * mm});
            skLineSegment(sketch, "E8.25.0.3", {"start": v(1946.67, 1210) * mm, "end": v(1946.67, 1056) * mm});
            skLineSegment(sketch, "E8.25.1.0", {"start": v(1946.67, 1054) * mm, "end": v(2100.67, 1054) * mm});
            skLineSegment(sketch, "E8.25.1.1", {"start": v(2100.67, 1054) * mm, "end": v(2100.67, 900) * mm});
            skLineSegment(sketch, "E8.25.1.2", {"start": v(1946.67, 900) * mm, "end": v(2100.67, 900) * mm});
            skLineSegment(sketch, "E8.25.1.3", {"start": v(1946.67, 1054) * mm, "end": v(1946.67, 900) * mm});
            skLineSegment(sketch, "E8.25.2.0", {"start": v(1946.67, 898) * mm, "end": v(2100.67, 898) * mm});
            skLineSegment(sketch, "E8.25.2.1", {"start": v(2100.67, 898) * mm, "end": v(2100.67, 744) * mm});
            skLineSegment(sketch, "E8.25.2.2", {"start": v(1946.67, 744) * mm, "end": v(2100.67, 744) * mm});
            skLineSegment(sketch, "E8.25.2.3", {"start": v(1946.67, 898) * mm, "end": v(1946.67, 744) * mm});
            skLineSegment(sketch, "E8.25.3.0", {"start": v(1946.67, 742) * mm, "end": v(2100.67, 742) * mm});
            skLineSegment(sketch, "E8.25.3.1", {"start": v(2100.67, 742) * mm, "end": v(2100.67, 588) * mm});
            skLineSegment(sketch, "E8.25.3.2", {"start": v(1946.67, 588) * mm, "end": v(2100.67, 588) * mm});
            skLineSegment(sketch, "E8.25.3.3", {"start": v(1946.67, 742) * mm, "end": v(1946.67, 588) * mm});
            skLineSegment(sketch, "E8.25.4.0", {"start": v(1946.67, 586) * mm, "end": v(2100.67, 586) * mm});
            skLineSegment(sketch, "E8.25.4.1", {"start": v(2100.67, 586) * mm, "end": v(2100.67, 432) * mm});
            skLineSegment(sketch, "E8.25.4.2", {"start": v(1946.67, 432) * mm, "end": v(2100.67, 432) * mm});
            skLineSegment(sketch, "E8.25.4.3", {"start": v(1946.67, 586) * mm, "end": v(1946.67, 432) * mm});
            skLineSegment(sketch, "E8.25.5.0", {"start": v(1946.67, 430) * mm, "end": v(2100.67, 430) * mm});
            skLineSegment(sketch, "E8.25.5.1", {"start": v(2100.67, 430) * mm, "end": v(2100.67, 276) * mm});
            skLineSegment(sketch, "E8.25.5.2", {"start": v(1946.67, 276) * mm, "end": v(2100.67, 276) * mm});
            skLineSegment(sketch, "E8.25.5.3", {"start": v(1946.67, 430) * mm, "end": v(1946.67, 276) * mm});
            skLineSegment(sketch, "E8.25.6.0", {"start": v(1946.67, 274) * mm, "end": v(2100.67, 274) * mm});
            skLineSegment(sketch, "E8.25.6.1", {"start": v(2100.67, 274) * mm, "end": v(2100.67, 120) * mm});
            skLineSegment(sketch, "E8.25.6.2", {"start": v(1946.67, 120) * mm, "end": v(2100.67, 120) * mm});
            skLineSegment(sketch, "E8.25.6.3", {"start": v(1946.67, 274) * mm, "end": v(1946.67, 120) * mm});
            skLineSegment(sketch, "E8.25.7.0", {"start": v(1946.67, 118) * mm, "end": v(2100.67, 118) * mm});
            skLineSegment(sketch, "E8.25.7.1", {"start": v(2100.67, 118) * mm, "end": v(2100.67, -36) * mm});
            skLineSegment(sketch, "E8.25.7.2", {"start": v(1946.67, -36) * mm, "end": v(2100.67, -36) * mm});
            skLineSegment(sketch, "E8.25.7.3", {"start": v(1946.67, 118) * mm, "end": v(1946.67, -36) * mm});
            skLineSegment(sketch, "E8.25.8.0", {"start": v(1946.67, -38) * mm, "end": v(2100.67, -38) * mm});
            skLineSegment(sketch, "E8.25.8.1", {"start": v(2100.67, -38) * mm, "end": v(2100.67, -192) * mm});
            skLineSegment(sketch, "E8.25.8.2", {"start": v(1946.67, -192) * mm, "end": v(2100.67, -192) * mm});
            skLineSegment(sketch, "E8.25.8.3", {"start": v(1946.67, -38) * mm, "end": v(1946.67, -192) * mm});
            skLineSegment(sketch, "E8.25.9.0", {"start": v(1946.67, -194) * mm, "end": v(2100.67, -194) * mm});
            skLineSegment(sketch, "E8.25.9.1", {"start": v(2100.67, -194) * mm, "end": v(2100.67, -348) * mm});
            skLineSegment(sketch, "E8.25.9.2", {"start": v(1946.67, -348) * mm, "end": v(2100.67, -348) * mm});
            skLineSegment(sketch, "E8.25.9.3", {"start": v(1946.67, -194) * mm, "end": v(1946.67, -348) * mm});
            skLineSegment(sketch, "E8.25.10.0", {"start": v(1946.67, -350) * mm, "end": v(2100.67, -350) * mm});
            skLineSegment(sketch, "E8.25.10.1", {"start": v(2100.67, -350) * mm, "end": v(2100.67, -504) * mm});
            skLineSegment(sketch, "E8.25.10.2", {"start": v(1946.67, -504) * mm, "end": v(2100.67, -504) * mm});
            skLineSegment(sketch, "E8.25.10.3", {"start": v(1946.67, -350) * mm, "end": v(1946.67, -504) * mm});
            skLineSegment(sketch, "E8.25.11.0", {"start": v(1946.67, -506) * mm, "end": v(2100.67, -506) * mm});
            skLineSegment(sketch, "E8.25.11.1", {"start": v(2100.67, -506) * mm, "end": v(2100.67, -660) * mm});
            skLineSegment(sketch, "E8.25.11.2", {"start": v(1946.67, -660) * mm, "end": v(2100.67, -660) * mm});
            skLineSegment(sketch, "E8.25.11.3", {"start": v(1946.67, -506) * mm, "end": v(1946.67, -660) * mm});
            skLineSegment(sketch, "E8.25.12.0", {"start": v(1946.67, -662) * mm, "end": v(2100.67, -662) * mm});
            skLineSegment(sketch, "E8.25.12.1", {"start": v(2100.67, -662) * mm, "end": v(2100.67, -816) * mm});
            skLineSegment(sketch, "E8.25.12.2", {"start": v(1946.67, -816) * mm, "end": v(2100.67, -816) * mm});
            skLineSegment(sketch, "E8.25.12.3", {"start": v(1946.67, -662) * mm, "end": v(1946.67, -816) * mm});
            skLineSegment(sketch, "E8.26.0.0", {"start": v(2102.67, 1210) * mm, "end": v(2256.67, 1210) * mm});
            skLineSegment(sketch, "E8.26.0.1", {"start": v(2256.67, 1210) * mm, "end": v(2256.67, 1056) * mm});
            skLineSegment(sketch, "E8.26.0.2", {"start": v(2102.67, 1056) * mm, "end": v(2256.67, 1056) * mm});
            skLineSegment(sketch, "E8.26.0.3", {"start": v(2102.67, 1210) * mm, "end": v(2102.67, 1056) * mm});
            skLineSegment(sketch, "E8.26.1.0", {"start": v(2102.67, 1054) * mm, "end": v(2256.67, 1054) * mm});
            skLineSegment(sketch, "E8.26.1.1", {"start": v(2256.67, 1054) * mm, "end": v(2256.67, 900) * mm});
            skLineSegment(sketch, "E8.26.1.2", {"start": v(2102.67, 900) * mm, "end": v(2256.67, 900) * mm});
            skLineSegment(sketch, "E8.26.1.3", {"start": v(2102.67, 1054) * mm, "end": v(2102.67, 900) * mm});
            skLineSegment(sketch, "E8.26.2.0", {"start": v(2102.67, 898) * mm, "end": v(2256.67, 898) * mm});
            skLineSegment(sketch, "E8.26.2.1", {"start": v(2256.67, 898) * mm, "end": v(2256.67, 744) * mm});
            skLineSegment(sketch, "E8.26.2.2", {"start": v(2102.67, 744) * mm, "end": v(2256.67, 744) * mm});
            skLineSegment(sketch, "E8.26.2.3", {"start": v(2102.67, 898) * mm, "end": v(2102.67, 744) * mm});
            skLineSegment(sketch, "E8.26.3.0", {"start": v(2102.67, 742) * mm, "end": v(2256.67, 742) * mm});
            skLineSegment(sketch, "E8.26.3.1", {"start": v(2256.67, 742) * mm, "end": v(2256.67, 588) * mm});
            skLineSegment(sketch, "E8.26.3.2", {"start": v(2102.67, 588) * mm, "end": v(2256.67, 588) * mm});
            skLineSegment(sketch, "E8.26.3.3", {"start": v(2102.67, 742) * mm, "end": v(2102.67, 588) * mm});
            skLineSegment(sketch, "E8.26.4.0", {"start": v(2102.67, 586) * mm, "end": v(2256.67, 586) * mm});
            skLineSegment(sketch, "E8.26.4.1", {"start": v(2256.67, 586) * mm, "end": v(2256.67, 432) * mm});
            skLineSegment(sketch, "E8.26.4.2", {"start": v(2102.67, 432) * mm, "end": v(2256.67, 432) * mm});
            skLineSegment(sketch, "E8.26.4.3", {"start": v(2102.67, 586) * mm, "end": v(2102.67, 432) * mm});
            skLineSegment(sketch, "E8.26.5.0", {"start": v(2102.67, 430) * mm, "end": v(2256.67, 430) * mm});
            skLineSegment(sketch, "E8.26.5.1", {"start": v(2256.67, 430) * mm, "end": v(2256.67, 276) * mm});
            skLineSegment(sketch, "E8.26.5.2", {"start": v(2102.67, 276) * mm, "end": v(2256.67, 276) * mm});
            skLineSegment(sketch, "E8.26.5.3", {"start": v(2102.67, 430) * mm, "end": v(2102.67, 276) * mm});
            skLineSegment(sketch, "E8.26.6.0", {"start": v(2102.67, 274) * mm, "end": v(2256.67, 274) * mm});
            skLineSegment(sketch, "E8.26.6.1", {"start": v(2256.67, 274) * mm, "end": v(2256.67, 120) * mm});
            skLineSegment(sketch, "E8.26.6.2", {"start": v(2102.67, 120) * mm, "end": v(2256.67, 120) * mm});
            skLineSegment(sketch, "E8.26.6.3", {"start": v(2102.67, 274) * mm, "end": v(2102.67, 120) * mm});
            skLineSegment(sketch, "E8.26.7.0", {"start": v(2102.67, 118) * mm, "end": v(2256.67, 118) * mm});
            skLineSegment(sketch, "E8.26.7.1", {"start": v(2256.67, 118) * mm, "end": v(2256.67, -36) * mm});
            skLineSegment(sketch, "E8.26.7.2", {"start": v(2102.67, -36) * mm, "end": v(2256.67, -36) * mm});
            skLineSegment(sketch, "E8.26.7.3", {"start": v(2102.67, 118) * mm, "end": v(2102.67, -36) * mm});
            skLineSegment(sketch, "E8.26.8.0", {"start": v(2102.67, -38) * mm, "end": v(2256.67, -38) * mm});
            skLineSegment(sketch, "E8.26.8.1", {"start": v(2256.67, -38) * mm, "end": v(2256.67, -192) * mm});
            skLineSegment(sketch, "E8.26.8.2", {"start": v(2102.67, -192) * mm, "end": v(2256.67, -192) * mm});
            skLineSegment(sketch, "E8.26.8.3", {"start": v(2102.67, -38) * mm, "end": v(2102.67, -192) * mm});
            skLineSegment(sketch, "E8.26.9.0", {"start": v(2102.67, -194) * mm, "end": v(2256.67, -194) * mm});
            skLineSegment(sketch, "E8.26.9.1", {"start": v(2256.67, -194) * mm, "end": v(2256.67, -348) * mm});
            skLineSegment(sketch, "E8.26.9.2", {"start": v(2102.67, -348) * mm, "end": v(2256.67, -348) * mm});
            skLineSegment(sketch, "E8.26.9.3", {"start": v(2102.67, -194) * mm, "end": v(2102.67, -348) * mm});
            skLineSegment(sketch, "E8.26.10.0", {"start": v(2102.67, -350) * mm, "end": v(2256.67, -350) * mm});
            skLineSegment(sketch, "E8.26.10.1", {"start": v(2256.67, -350) * mm, "end": v(2256.67, -504) * mm});
            skLineSegment(sketch, "E8.26.10.2", {"start": v(2102.67, -504) * mm, "end": v(2256.67, -504) * mm});
            skLineSegment(sketch, "E8.26.10.3", {"start": v(2102.67, -350) * mm, "end": v(2102.67, -504) * mm});
            skLineSegment(sketch, "E8.26.11.0", {"start": v(2102.67, -506) * mm, "end": v(2256.67, -506) * mm});
            skLineSegment(sketch, "E8.26.11.1", {"start": v(2256.67, -506) * mm, "end": v(2256.67, -660) * mm});
            skLineSegment(sketch, "E8.26.11.2", {"start": v(2102.67, -660) * mm, "end": v(2256.67, -660) * mm});
            skLineSegment(sketch, "E8.26.11.3", {"start": v(2102.67, -506) * mm, "end": v(2102.67, -660) * mm});
            skLineSegment(sketch, "E8.26.12.0", {"start": v(2102.67, -662) * mm, "end": v(2256.67, -662) * mm});
            skLineSegment(sketch, "E8.26.12.1", {"start": v(2256.67, -662) * mm, "end": v(2256.67, -816) * mm});
            skLineSegment(sketch, "E8.26.12.2", {"start": v(2102.67, -816) * mm, "end": v(2256.67, -816) * mm});
            skLineSegment(sketch, "E8.26.12.3", {"start": v(2102.67, -662) * mm, "end": v(2102.67, -816) * mm});
            skLineSegment(sketch, "E8.27.0.0", {"start": v(2258.67, 1210) * mm, "end": v(2412.67, 1210) * mm});
            skLineSegment(sketch, "E8.27.0.1", {"start": v(2412.67, 1210) * mm, "end": v(2412.67, 1056) * mm});
            skLineSegment(sketch, "E8.27.0.2", {"start": v(2258.67, 1056) * mm, "end": v(2412.67, 1056) * mm});
            skLineSegment(sketch, "E8.27.0.3", {"start": v(2258.67, 1210) * mm, "end": v(2258.67, 1056) * mm});
            skLineSegment(sketch, "E8.27.1.0", {"start": v(2258.67, 1054) * mm, "end": v(2412.67, 1054) * mm});
            skLineSegment(sketch, "E8.27.1.1", {"start": v(2412.67, 1054) * mm, "end": v(2412.67, 900) * mm});
            skLineSegment(sketch, "E8.27.1.2", {"start": v(2258.67, 900) * mm, "end": v(2412.67, 900) * mm});
            skLineSegment(sketch, "E8.27.1.3", {"start": v(2258.67, 1054) * mm, "end": v(2258.67, 900) * mm});
            skLineSegment(sketch, "E8.27.2.0", {"start": v(2258.67, 898) * mm, "end": v(2412.67, 898) * mm});
            skLineSegment(sketch, "E8.27.2.1", {"start": v(2412.67, 898) * mm, "end": v(2412.67, 744) * mm});
            skLineSegment(sketch, "E8.27.2.2", {"start": v(2258.67, 744) * mm, "end": v(2412.67, 744) * mm});
            skLineSegment(sketch, "E8.27.2.3", {"start": v(2258.67, 898) * mm, "end": v(2258.67, 744) * mm});
            skLineSegment(sketch, "E8.27.3.0", {"start": v(2258.67, 742) * mm, "end": v(2412.67, 742) * mm});
            skLineSegment(sketch, "E8.27.3.1", {"start": v(2412.67, 742) * mm, "end": v(2412.67, 588) * mm});
            skLineSegment(sketch, "E8.27.3.2", {"start": v(2258.67, 588) * mm, "end": v(2412.67, 588) * mm});
            skLineSegment(sketch, "E8.27.3.3", {"start": v(2258.67, 742) * mm, "end": v(2258.67, 588) * mm});
            skLineSegment(sketch, "E8.27.4.0", {"start": v(2258.67, 586) * mm, "end": v(2412.67, 586) * mm});
            skLineSegment(sketch, "E8.27.4.1", {"start": v(2412.67, 586) * mm, "end": v(2412.67, 432) * mm});
            skLineSegment(sketch, "E8.27.4.2", {"start": v(2258.67, 432) * mm, "end": v(2412.67, 432) * mm});
            skLineSegment(sketch, "E8.27.4.3", {"start": v(2258.67, 586) * mm, "end": v(2258.67, 432) * mm});
            skLineSegment(sketch, "E8.27.5.0", {"start": v(2258.67, 430) * mm, "end": v(2412.67, 430) * mm});
            skLineSegment(sketch, "E8.27.5.1", {"start": v(2412.67, 430) * mm, "end": v(2412.67, 276) * mm});
            skLineSegment(sketch, "E8.27.5.2", {"start": v(2258.67, 276) * mm, "end": v(2412.67, 276) * mm});
            skLineSegment(sketch, "E8.27.5.3", {"start": v(2258.67, 430) * mm, "end": v(2258.67, 276) * mm});
            skLineSegment(sketch, "E8.27.6.0", {"start": v(2258.67, 274) * mm, "end": v(2412.67, 274) * mm});
            skLineSegment(sketch, "E8.27.6.1", {"start": v(2412.67, 274) * mm, "end": v(2412.67, 120) * mm});
            skLineSegment(sketch, "E8.27.6.2", {"start": v(2258.67, 120) * mm, "end": v(2412.67, 120) * mm});
            skLineSegment(sketch, "E8.27.6.3", {"start": v(2258.67, 274) * mm, "end": v(2258.67, 120) * mm});
            skLineSegment(sketch, "E8.27.7.0", {"start": v(2258.67, 118) * mm, "end": v(2412.67, 118) * mm});
            skLineSegment(sketch, "E8.27.7.1", {"start": v(2412.67, 118) * mm, "end": v(2412.67, -36) * mm});
            skLineSegment(sketch, "E8.27.7.2", {"start": v(2258.67, -36) * mm, "end": v(2412.67, -36) * mm});
            skLineSegment(sketch, "E8.27.7.3", {"start": v(2258.67, 118) * mm, "end": v(2258.67, -36) * mm});
            skLineSegment(sketch, "E8.27.8.0", {"start": v(2258.67, -38) * mm, "end": v(2412.67, -38) * mm});
            skLineSegment(sketch, "E8.27.8.1", {"start": v(2412.67, -38) * mm, "end": v(2412.67, -192) * mm});
            skLineSegment(sketch, "E8.27.8.2", {"start": v(2258.67, -192) * mm, "end": v(2412.67, -192) * mm});
            skLineSegment(sketch, "E8.27.8.3", {"start": v(2258.67, -38) * mm, "end": v(2258.67, -192) * mm});
            skLineSegment(sketch, "E8.27.9.0", {"start": v(2258.67, -194) * mm, "end": v(2412.67, -194) * mm});
            skLineSegment(sketch, "E8.27.9.1", {"start": v(2412.67, -194) * mm, "end": v(2412.67, -348) * mm});
            skLineSegment(sketch, "E8.27.9.2", {"start": v(2258.67, -348) * mm, "end": v(2412.67, -348) * mm});
            skLineSegment(sketch, "E8.27.9.3", {"start": v(2258.67, -194) * mm, "end": v(2258.67, -348) * mm});
            skLineSegment(sketch, "E8.27.10.0", {"start": v(2258.67, -350) * mm, "end": v(2412.67, -350) * mm});
            skLineSegment(sketch, "E8.27.10.1", {"start": v(2412.67, -350) * mm, "end": v(2412.67, -504) * mm});
            skLineSegment(sketch, "E8.27.10.2", {"start": v(2258.67, -504) * mm, "end": v(2412.67, -504) * mm});
            skLineSegment(sketch, "E8.27.10.3", {"start": v(2258.67, -350) * mm, "end": v(2258.67, -504) * mm});
            skLineSegment(sketch, "E8.27.11.0", {"start": v(2258.67, -506) * mm, "end": v(2412.67, -506) * mm});
            skLineSegment(sketch, "E8.27.11.1", {"start": v(2412.67, -506) * mm, "end": v(2412.67, -660) * mm});
            skLineSegment(sketch, "E8.27.11.2", {"start": v(2258.67, -660) * mm, "end": v(2412.67, -660) * mm});
            skLineSegment(sketch, "E8.27.11.3", {"start": v(2258.67, -506) * mm, "end": v(2258.67, -660) * mm});
            skLineSegment(sketch, "E8.27.12.0", {"start": v(2258.67, -662) * mm, "end": v(2412.67, -662) * mm});
            skLineSegment(sketch, "E8.27.12.1", {"start": v(2412.67, -662) * mm, "end": v(2412.67, -816) * mm});
            skLineSegment(sketch, "E8.27.12.2", {"start": v(2258.67, -816) * mm, "end": v(2412.67, -816) * mm});
            skLineSegment(sketch, "E8.27.12.3", {"start": v(2258.67, -662) * mm, "end": v(2258.67, -816) * mm});
            skLineSegment(sketch, "E8.28.0.0", {"start": v(2414.67, 1210) * mm, "end": v(2568.67, 1210) * mm});
            skLineSegment(sketch, "E8.28.0.1", {"start": v(2568.67, 1210) * mm, "end": v(2568.67, 1056) * mm});
            skLineSegment(sketch, "E8.28.0.2", {"start": v(2414.67, 1056) * mm, "end": v(2568.67, 1056) * mm});
            skLineSegment(sketch, "E8.28.0.3", {"start": v(2414.67, 1210) * mm, "end": v(2414.67, 1056) * mm});
            skLineSegment(sketch, "E8.28.1.0", {"start": v(2414.67, 1054) * mm, "end": v(2568.67, 1054) * mm});
            skLineSegment(sketch, "E8.28.1.1", {"start": v(2568.67, 1054) * mm, "end": v(2568.67, 900) * mm});
            skLineSegment(sketch, "E8.28.1.2", {"start": v(2414.67, 900) * mm, "end": v(2568.67, 900) * mm});
            skLineSegment(sketch, "E8.28.1.3", {"start": v(2414.67, 1054) * mm, "end": v(2414.67, 900) * mm});
            skLineSegment(sketch, "E8.28.2.0", {"start": v(2414.67, 898) * mm, "end": v(2568.67, 898) * mm});
            skLineSegment(sketch, "E8.28.2.1", {"start": v(2568.67, 898) * mm, "end": v(2568.67, 744) * mm});
            skLineSegment(sketch, "E8.28.2.2", {"start": v(2414.67, 744) * mm, "end": v(2568.67, 744) * mm});
            skLineSegment(sketch, "E8.28.2.3", {"start": v(2414.67, 898) * mm, "end": v(2414.67, 744) * mm});
            skLineSegment(sketch, "E8.28.3.0", {"start": v(2414.67, 742) * mm, "end": v(2568.67, 742) * mm});
            skLineSegment(sketch, "E8.28.3.1", {"start": v(2568.67, 742) * mm, "end": v(2568.67, 588) * mm});
            skLineSegment(sketch, "E8.28.3.2", {"start": v(2414.67, 588) * mm, "end": v(2568.67, 588) * mm});
            skLineSegment(sketch, "E8.28.3.3", {"start": v(2414.67, 742) * mm, "end": v(2414.67, 588) * mm});
            skLineSegment(sketch, "E8.28.4.0", {"start": v(2414.67, 586) * mm, "end": v(2568.67, 586) * mm});
            skLineSegment(sketch, "E8.28.4.1", {"start": v(2568.67, 586) * mm, "end": v(2568.67, 432) * mm});
            skLineSegment(sketch, "E8.28.4.2", {"start": v(2414.67, 432) * mm, "end": v(2568.67, 432) * mm});
            skLineSegment(sketch, "E8.28.4.3", {"start": v(2414.67, 586) * mm, "end": v(2414.67, 432) * mm});
            skLineSegment(sketch, "E8.28.5.0", {"start": v(2414.67, 430) * mm, "end": v(2568.67, 430) * mm});
            skLineSegment(sketch, "E8.28.5.1", {"start": v(2568.67, 430) * mm, "end": v(2568.67, 276) * mm});
            skLineSegment(sketch, "E8.28.5.2", {"start": v(2414.67, 276) * mm, "end": v(2568.67, 276) * mm});
            skLineSegment(sketch, "E8.28.5.3", {"start": v(2414.67, 430) * mm, "end": v(2414.67, 276) * mm});
            skLineSegment(sketch, "E8.28.6.0", {"start": v(2414.67, 274) * mm, "end": v(2568.67, 274) * mm});
            skLineSegment(sketch, "E8.28.6.1", {"start": v(2568.67, 274) * mm, "end": v(2568.67, 120) * mm});
            skLineSegment(sketch, "E8.28.6.2", {"start": v(2414.67, 120) * mm, "end": v(2568.67, 120) * mm});
            skLineSegment(sketch, "E8.28.6.3", {"start": v(2414.67, 274) * mm, "end": v(2414.67, 120) * mm});
            skLineSegment(sketch, "E8.28.7.0", {"start": v(2414.67, 118) * mm, "end": v(2568.67, 118) * mm});
            skLineSegment(sketch, "E8.28.7.1", {"start": v(2568.67, 118) * mm, "end": v(2568.67, -36) * mm});
            skLineSegment(sketch, "E8.28.7.2", {"start": v(2414.67, -36) * mm, "end": v(2568.67, -36) * mm});
            skLineSegment(sketch, "E8.28.7.3", {"start": v(2414.67, 118) * mm, "end": v(2414.67, -36) * mm});
            skLineSegment(sketch, "E8.28.8.0", {"start": v(2414.67, -38) * mm, "end": v(2568.67, -38) * mm});
            skLineSegment(sketch, "E8.28.8.1", {"start": v(2568.67, -38) * mm, "end": v(2568.67, -192) * mm});
            skLineSegment(sketch, "E8.28.8.2", {"start": v(2414.67, -192) * mm, "end": v(2568.67, -192) * mm});
            skLineSegment(sketch, "E8.28.8.3", {"start": v(2414.67, -38) * mm, "end": v(2414.67, -192) * mm});
            skLineSegment(sketch, "E8.28.9.0", {"start": v(2414.67, -194) * mm, "end": v(2568.67, -194) * mm});
            skLineSegment(sketch, "E8.28.9.1", {"start": v(2568.67, -194) * mm, "end": v(2568.67, -348) * mm});
            skLineSegment(sketch, "E8.28.9.2", {"start": v(2414.67, -348) * mm, "end": v(2568.67, -348) * mm});
            skLineSegment(sketch, "E8.28.9.3", {"start": v(2414.67, -194) * mm, "end": v(2414.67, -348) * mm});
            skLineSegment(sketch, "E8.28.10.0", {"start": v(2414.67, -350) * mm, "end": v(2568.67, -350) * mm});
            skLineSegment(sketch, "E8.28.10.1", {"start": v(2568.67, -350) * mm, "end": v(2568.67, -504) * mm});
            skLineSegment(sketch, "E8.28.10.2", {"start": v(2414.67, -504) * mm, "end": v(2568.67, -504) * mm});
            skLineSegment(sketch, "E8.28.10.3", {"start": v(2414.67, -350) * mm, "end": v(2414.67, -504) * mm});
            skLineSegment(sketch, "E8.28.11.0", {"start": v(2414.67, -506) * mm, "end": v(2568.67, -506) * mm});
            skLineSegment(sketch, "E8.28.11.1", {"start": v(2568.67, -506) * mm, "end": v(2568.67, -660) * mm});
            skLineSegment(sketch, "E8.28.11.2", {"start": v(2414.67, -660) * mm, "end": v(2568.67, -660) * mm});
            skLineSegment(sketch, "E8.28.11.3", {"start": v(2414.67, -506) * mm, "end": v(2414.67, -660) * mm});
            skLineSegment(sketch, "E8.28.12.0", {"start": v(2414.67, -662) * mm, "end": v(2568.67, -662) * mm});
            skLineSegment(sketch, "E8.28.12.1", {"start": v(2568.67, -662) * mm, "end": v(2568.67, -816) * mm});
            skLineSegment(sketch, "E8.28.12.2", {"start": v(2414.67, -816) * mm, "end": v(2568.67, -816) * mm});
            skLineSegment(sketch, "E8.28.12.3", {"start": v(2414.67, -662) * mm, "end": v(2414.67, -816) * mm});
            skLineSegment(sketch, "E8.29.0.0", {"start": v(2570.67, 1210) * mm, "end": v(2724.67, 1210) * mm});
            skLineSegment(sketch, "E8.29.0.1", {"start": v(2724.67, 1210) * mm, "end": v(2724.67, 1056) * mm});
            skLineSegment(sketch, "E8.29.0.2", {"start": v(2570.67, 1056) * mm, "end": v(2724.67, 1056) * mm});
            skLineSegment(sketch, "E8.29.0.3", {"start": v(2570.67, 1210) * mm, "end": v(2570.67, 1056) * mm});
            skLineSegment(sketch, "E8.29.1.0", {"start": v(2570.67, 1054) * mm, "end": v(2724.67, 1054) * mm});
            skLineSegment(sketch, "E8.29.1.1", {"start": v(2724.67, 1054) * mm, "end": v(2724.67, 900) * mm});
            skLineSegment(sketch, "E8.29.1.2", {"start": v(2570.67, 900) * mm, "end": v(2724.67, 900) * mm});
            skLineSegment(sketch, "E8.29.1.3", {"start": v(2570.67, 1054) * mm, "end": v(2570.67, 900) * mm});
            skLineSegment(sketch, "E8.29.2.0", {"start": v(2570.67, 898) * mm, "end": v(2724.67, 898) * mm});
            skLineSegment(sketch, "E8.29.2.1", {"start": v(2724.67, 898) * mm, "end": v(2724.67, 744) * mm});
            skLineSegment(sketch, "E8.29.2.2", {"start": v(2570.67, 744) * mm, "end": v(2724.67, 744) * mm});
            skLineSegment(sketch, "E8.29.2.3", {"start": v(2570.67, 898) * mm, "end": v(2570.67, 744) * mm});
            skLineSegment(sketch, "E8.29.3.0", {"start": v(2570.67, 742) * mm, "end": v(2724.67, 742) * mm});
            skLineSegment(sketch, "E8.29.3.1", {"start": v(2724.67, 742) * mm, "end": v(2724.67, 588) * mm});
            skLineSegment(sketch, "E8.29.3.2", {"start": v(2570.67, 588) * mm, "end": v(2724.67, 588) * mm});
            skLineSegment(sketch, "E8.29.3.3", {"start": v(2570.67, 742) * mm, "end": v(2570.67, 588) * mm});
            skLineSegment(sketch, "E8.29.4.0", {"start": v(2570.67, 586) * mm, "end": v(2724.67, 586) * mm});
            skLineSegment(sketch, "E8.29.4.1", {"start": v(2724.67, 586) * mm, "end": v(2724.67, 432) * mm});
            skLineSegment(sketch, "E8.29.4.2", {"start": v(2570.67, 432) * mm, "end": v(2724.67, 432) * mm});
            skLineSegment(sketch, "E8.29.4.3", {"start": v(2570.67, 586) * mm, "end": v(2570.67, 432) * mm});
            skLineSegment(sketch, "E8.29.5.0", {"start": v(2570.67, 430) * mm, "end": v(2724.67, 430) * mm});
            skLineSegment(sketch, "E8.29.5.1", {"start": v(2724.67, 430) * mm, "end": v(2724.67, 276) * mm});
            skLineSegment(sketch, "E8.29.5.2", {"start": v(2570.67, 276) * mm, "end": v(2724.67, 276) * mm});
            skLineSegment(sketch, "E8.29.5.3", {"start": v(2570.67, 430) * mm, "end": v(2570.67, 276) * mm});
            skLineSegment(sketch, "E8.29.6.0", {"start": v(2570.67, 274) * mm, "end": v(2724.67, 274) * mm});
            skLineSegment(sketch, "E8.29.6.1", {"start": v(2724.67, 274) * mm, "end": v(2724.67, 120) * mm});
            skLineSegment(sketch, "E8.29.6.2", {"start": v(2570.67, 120) * mm, "end": v(2724.67, 120) * mm});
            skLineSegment(sketch, "E8.29.6.3", {"start": v(2570.67, 274) * mm, "end": v(2570.67, 120) * mm});
            skLineSegment(sketch, "E8.29.7.0", {"start": v(2570.67, 118) * mm, "end": v(2724.67, 118) * mm});
            skLineSegment(sketch, "E8.29.7.1", {"start": v(2724.67, 118) * mm, "end": v(2724.67, -36) * mm});
            skLineSegment(sketch, "E8.29.7.2", {"start": v(2570.67, -36) * mm, "end": v(2724.67, -36) * mm});
            skLineSegment(sketch, "E8.29.7.3", {"start": v(2570.67, 118) * mm, "end": v(2570.67, -36) * mm});
            skLineSegment(sketch, "E8.29.8.0", {"start": v(2570.67, -38) * mm, "end": v(2724.67, -38) * mm});
            skLineSegment(sketch, "E8.29.8.1", {"start": v(2724.67, -38) * mm, "end": v(2724.67, -192) * mm});
            skLineSegment(sketch, "E8.29.8.2", {"start": v(2570.67, -192) * mm, "end": v(2724.67, -192) * mm});
            skLineSegment(sketch, "E8.29.8.3", {"start": v(2570.67, -38) * mm, "end": v(2570.67, -192) * mm});
            skLineSegment(sketch, "E8.29.9.0", {"start": v(2570.67, -194) * mm, "end": v(2724.67, -194) * mm});
            skLineSegment(sketch, "E8.29.9.1", {"start": v(2724.67, -194) * mm, "end": v(2724.67, -348) * mm});
            skLineSegment(sketch, "E8.29.9.2", {"start": v(2570.67, -348) * mm, "end": v(2724.67, -348) * mm});
            skLineSegment(sketch, "E8.29.9.3", {"start": v(2570.67, -194) * mm, "end": v(2570.67, -348) * mm});
            skLineSegment(sketch, "E8.29.10.0", {"start": v(2570.67, -350) * mm, "end": v(2724.67, -350) * mm});
            skLineSegment(sketch, "E8.29.10.1", {"start": v(2724.67, -350) * mm, "end": v(2724.67, -504) * mm});
            skLineSegment(sketch, "E8.29.10.2", {"start": v(2570.67, -504) * mm, "end": v(2724.67, -504) * mm});
            skLineSegment(sketch, "E8.29.10.3", {"start": v(2570.67, -350) * mm, "end": v(2570.67, -504) * mm});
            skLineSegment(sketch, "E8.29.11.0", {"start": v(2570.67, -506) * mm, "end": v(2724.67, -506) * mm});
            skLineSegment(sketch, "E8.29.11.1", {"start": v(2724.67, -506) * mm, "end": v(2724.67, -660) * mm});
            skLineSegment(sketch, "E8.29.11.2", {"start": v(2570.67, -660) * mm, "end": v(2724.67, -660) * mm});
            skLineSegment(sketch, "E8.29.11.3", {"start": v(2570.67, -506) * mm, "end": v(2570.67, -660) * mm});
            skLineSegment(sketch, "E8.29.12.0", {"start": v(2570.67, -662) * mm, "end": v(2724.67, -662) * mm});
            skLineSegment(sketch, "E8.29.12.1", {"start": v(2724.67, -662) * mm, "end": v(2724.67, -816) * mm});
            skLineSegment(sketch, "E8.29.12.2", {"start": v(2570.67, -816) * mm, "end": v(2724.67, -816) * mm});
            skLineSegment(sketch, "E8.29.12.3", {"start": v(2570.67, -662) * mm, "end": v(2570.67, -816) * mm});
            skLineSegment(sketch, "E8.30.0.0", {"start": v(2726.67, 1210) * mm, "end": v(2880.67, 1210) * mm});
            skLineSegment(sketch, "E8.30.0.1", {"start": v(2880.67, 1210) * mm, "end": v(2880.67, 1056) * mm});
            skLineSegment(sketch, "E8.30.0.2", {"start": v(2726.67, 1056) * mm, "end": v(2880.67, 1056) * mm});
            skLineSegment(sketch, "E8.30.0.3", {"start": v(2726.67, 1210) * mm, "end": v(2726.67, 1056) * mm});
            skLineSegment(sketch, "E8.30.1.0", {"start": v(2726.67, 1054) * mm, "end": v(2880.67, 1054) * mm});
            skLineSegment(sketch, "E8.30.1.1", {"start": v(2880.67, 1054) * mm, "end": v(2880.67, 900) * mm});
            skLineSegment(sketch, "E8.30.1.2", {"start": v(2726.67, 900) * mm, "end": v(2880.67, 900) * mm});
            skLineSegment(sketch, "E8.30.1.3", {"start": v(2726.67, 1054) * mm, "end": v(2726.67, 900) * mm});
            skLineSegment(sketch, "E8.30.2.0", {"start": v(2726.67, 898) * mm, "end": v(2880.67, 898) * mm});
            skLineSegment(sketch, "E8.30.2.1", {"start": v(2880.67, 898) * mm, "end": v(2880.67, 744) * mm});
            skLineSegment(sketch, "E8.30.2.2", {"start": v(2726.67, 744) * mm, "end": v(2880.67, 744) * mm});
            skLineSegment(sketch, "E8.30.2.3", {"start": v(2726.67, 898) * mm, "end": v(2726.67, 744) * mm});
            skLineSegment(sketch, "E8.30.3.0", {"start": v(2726.67, 742) * mm, "end": v(2880.67, 742) * mm});
            skLineSegment(sketch, "E8.30.3.1", {"start": v(2880.67, 742) * mm, "end": v(2880.67, 588) * mm});
            skLineSegment(sketch, "E8.30.3.2", {"start": v(2726.67, 588) * mm, "end": v(2880.67, 588) * mm});
            skLineSegment(sketch, "E8.30.3.3", {"start": v(2726.67, 742) * mm, "end": v(2726.67, 588) * mm});
            skLineSegment(sketch, "E8.30.4.0", {"start": v(2726.67, 586) * mm, "end": v(2880.67, 586) * mm});
            skLineSegment(sketch, "E8.30.4.1", {"start": v(2880.67, 586) * mm, "end": v(2880.67, 432) * mm});
            skLineSegment(sketch, "E8.30.4.2", {"start": v(2726.67, 432) * mm, "end": v(2880.67, 432) * mm});
            skLineSegment(sketch, "E8.30.4.3", {"start": v(2726.67, 586) * mm, "end": v(2726.67, 432) * mm});
            skLineSegment(sketch, "E8.30.5.0", {"start": v(2726.67, 430) * mm, "end": v(2880.67, 430) * mm});
            skLineSegment(sketch, "E8.30.5.1", {"start": v(2880.67, 430) * mm, "end": v(2880.67, 276) * mm});
            skLineSegment(sketch, "E8.30.5.2", {"start": v(2726.67, 276) * mm, "end": v(2880.67, 276) * mm});
            skLineSegment(sketch, "E8.30.5.3", {"start": v(2726.67, 430) * mm, "end": v(2726.67, 276) * mm});
            skLineSegment(sketch, "E8.30.6.0", {"start": v(2726.67, 274) * mm, "end": v(2880.67, 274) * mm});
            skLineSegment(sketch, "E8.30.6.1", {"start": v(2880.67, 274) * mm, "end": v(2880.67, 120) * mm});
            skLineSegment(sketch, "E8.30.6.2", {"start": v(2726.67, 120) * mm, "end": v(2880.67, 120) * mm});
            skLineSegment(sketch, "E8.30.6.3", {"start": v(2726.67, 274) * mm, "end": v(2726.67, 120) * mm});
            skLineSegment(sketch, "E8.30.7.0", {"start": v(2726.67, 118) * mm, "end": v(2880.67, 118) * mm});
            skLineSegment(sketch, "E8.30.7.1", {"start": v(2880.67, 118) * mm, "end": v(2880.67, -36) * mm});
            skLineSegment(sketch, "E8.30.7.2", {"start": v(2726.67, -36) * mm, "end": v(2880.67, -36) * mm});
            skLineSegment(sketch, "E8.30.7.3", {"start": v(2726.67, 118) * mm, "end": v(2726.67, -36) * mm});
            skLineSegment(sketch, "E8.30.8.0", {"start": v(2726.67, -38) * mm, "end": v(2880.67, -38) * mm});
            skLineSegment(sketch, "E8.30.8.1", {"start": v(2880.67, -38) * mm, "end": v(2880.67, -192) * mm});
            skLineSegment(sketch, "E8.30.8.2", {"start": v(2726.67, -192) * mm, "end": v(2880.67, -192) * mm});
            skLineSegment(sketch, "E8.30.8.3", {"start": v(2726.67, -38) * mm, "end": v(2726.67, -192) * mm});
            skLineSegment(sketch, "E8.30.9.0", {"start": v(2726.67, -194) * mm, "end": v(2880.67, -194) * mm});
            skLineSegment(sketch, "E8.30.9.1", {"start": v(2880.67, -194) * mm, "end": v(2880.67, -348) * mm});
            skLineSegment(sketch, "E8.30.9.2", {"start": v(2726.67, -348) * mm, "end": v(2880.67, -348) * mm});
            skLineSegment(sketch, "E8.30.9.3", {"start": v(2726.67, -194) * mm, "end": v(2726.67, -348) * mm});
            skLineSegment(sketch, "E8.30.10.0", {"start": v(2726.67, -350) * mm, "end": v(2880.67, -350) * mm});
            skLineSegment(sketch, "E8.30.10.1", {"start": v(2880.67, -350) * mm, "end": v(2880.67, -504) * mm});
            skLineSegment(sketch, "E8.30.10.2", {"start": v(2726.67, -504) * mm, "end": v(2880.67, -504) * mm});
            skLineSegment(sketch, "E8.30.10.3", {"start": v(2726.67, -350) * mm, "end": v(2726.67, -504) * mm});
            skLineSegment(sketch, "E8.30.11.0", {"start": v(2726.67, -506) * mm, "end": v(2880.67, -506) * mm});
            skLineSegment(sketch, "E8.30.11.1", {"start": v(2880.67, -506) * mm, "end": v(2880.67, -660) * mm});
            skLineSegment(sketch, "E8.30.11.2", {"start": v(2726.67, -660) * mm, "end": v(2880.67, -660) * mm});
            skLineSegment(sketch, "E8.30.11.3", {"start": v(2726.67, -506) * mm, "end": v(2726.67, -660) * mm});
            skLineSegment(sketch, "E8.30.12.0", {"start": v(2726.67, -662) * mm, "end": v(2880.67, -662) * mm});
            skLineSegment(sketch, "E8.30.12.1", {"start": v(2880.67, -662) * mm, "end": v(2880.67, -816) * mm});
            skLineSegment(sketch, "E8.30.12.2", {"start": v(2726.67, -816) * mm, "end": v(2880.67, -816) * mm});
            skLineSegment(sketch, "E8.30.12.3", {"start": v(2726.67, -662) * mm, "end": v(2726.67, -816) * mm});
            skLineSegment(sketch, "E8.31.0.0", {"start": v(2882.67, 1210) * mm, "end": v(3036.67, 1210) * mm});
            skLineSegment(sketch, "E8.31.0.1", {"start": v(3036.67, 1210) * mm, "end": v(3036.67, 1056) * mm});
            skLineSegment(sketch, "E8.31.0.2", {"start": v(2882.67, 1056) * mm, "end": v(3036.67, 1056) * mm});
            skLineSegment(sketch, "E8.31.0.3", {"start": v(2882.67, 1210) * mm, "end": v(2882.67, 1056) * mm});
            skLineSegment(sketch, "E8.31.1.0", {"start": v(2882.67, 1054) * mm, "end": v(3036.67, 1054) * mm});
            skLineSegment(sketch, "E8.31.1.1", {"start": v(3036.67, 1054) * mm, "end": v(3036.67, 900) * mm});
            skLineSegment(sketch, "E8.31.1.2", {"start": v(2882.67, 900) * mm, "end": v(3036.67, 900) * mm});
            skLineSegment(sketch, "E8.31.1.3", {"start": v(2882.67, 1054) * mm, "end": v(2882.67, 900) * mm});
            skLineSegment(sketch, "E8.31.2.0", {"start": v(2882.67, 898) * mm, "end": v(3036.67, 898) * mm});
            skLineSegment(sketch, "E8.31.2.1", {"start": v(3036.67, 898) * mm, "end": v(3036.67, 744) * mm});
            skLineSegment(sketch, "E8.31.2.2", {"start": v(2882.67, 744) * mm, "end": v(3036.67, 744) * mm});
            skLineSegment(sketch, "E8.31.2.3", {"start": v(2882.67, 898) * mm, "end": v(2882.67, 744) * mm});
            skLineSegment(sketch, "E8.31.3.0", {"start": v(2882.67, 742) * mm, "end": v(3036.67, 742) * mm});
            skLineSegment(sketch, "E8.31.3.1", {"start": v(3036.67, 742) * mm, "end": v(3036.67, 588) * mm});
            skLineSegment(sketch, "E8.31.3.2", {"start": v(2882.67, 588) * mm, "end": v(3036.67, 588) * mm});
            skLineSegment(sketch, "E8.31.3.3", {"start": v(2882.67, 742) * mm, "end": v(2882.67, 588) * mm});
            skLineSegment(sketch, "E8.31.4.0", {"start": v(2882.67, 586) * mm, "end": v(3036.67, 586) * mm});
            skLineSegment(sketch, "E8.31.4.1", {"start": v(3036.67, 586) * mm, "end": v(3036.67, 432) * mm});
            skLineSegment(sketch, "E8.31.4.2", {"start": v(2882.67, 432) * mm, "end": v(3036.67, 432) * mm});
            skLineSegment(sketch, "E8.31.4.3", {"start": v(2882.67, 586) * mm, "end": v(2882.67, 432) * mm});
            skLineSegment(sketch, "E8.31.5.0", {"start": v(2882.67, 430) * mm, "end": v(3036.67, 430) * mm});
            skLineSegment(sketch, "E8.31.5.1", {"start": v(3036.67, 430) * mm, "end": v(3036.67, 276) * mm});
            skLineSegment(sketch, "E8.31.5.2", {"start": v(2882.67, 276) * mm, "end": v(3036.67, 276) * mm});
            skLineSegment(sketch, "E8.31.5.3", {"start": v(2882.67, 430) * mm, "end": v(2882.67, 276) * mm});
            skLineSegment(sketch, "E8.31.6.0", {"start": v(2882.67, 274) * mm, "end": v(3036.67, 274) * mm});
            skLineSegment(sketch, "E8.31.6.1", {"start": v(3036.67, 274) * mm, "end": v(3036.67, 120) * mm});
            skLineSegment(sketch, "E8.31.6.2", {"start": v(2882.67, 120) * mm, "end": v(3036.67, 120) * mm});
            skLineSegment(sketch, "E8.31.6.3", {"start": v(2882.67, 274) * mm, "end": v(2882.67, 120) * mm});
            skLineSegment(sketch, "E8.31.7.0", {"start": v(2882.67, 118) * mm, "end": v(3036.67, 118) * mm});
            skLineSegment(sketch, "E8.31.7.1", {"start": v(3036.67, 118) * mm, "end": v(3036.67, -36) * mm});
            skLineSegment(sketch, "E8.31.7.2", {"start": v(2882.67, -36) * mm, "end": v(3036.67, -36) * mm});
            skLineSegment(sketch, "E8.31.7.3", {"start": v(2882.67, 118) * mm, "end": v(2882.67, -36) * mm});
            skLineSegment(sketch, "E8.31.8.0", {"start": v(2882.67, -38) * mm, "end": v(3036.67, -38) * mm});
            skLineSegment(sketch, "E8.31.8.1", {"start": v(3036.67, -38) * mm, "end": v(3036.67, -192) * mm});
            skLineSegment(sketch, "E8.31.8.2", {"start": v(2882.67, -192) * mm, "end": v(3036.67, -192) * mm});
            skLineSegment(sketch, "E8.31.8.3", {"start": v(2882.67, -38) * mm, "end": v(2882.67, -192) * mm});
            skLineSegment(sketch, "E8.31.9.0", {"start": v(2882.67, -194) * mm, "end": v(3036.67, -194) * mm});
            skLineSegment(sketch, "E8.31.9.1", {"start": v(3036.67, -194) * mm, "end": v(3036.67, -348) * mm});
            skLineSegment(sketch, "E8.31.9.2", {"start": v(2882.67, -348) * mm, "end": v(3036.67, -348) * mm});
            skLineSegment(sketch, "E8.31.9.3", {"start": v(2882.67, -194) * mm, "end": v(2882.67, -348) * mm});
            skLineSegment(sketch, "E8.31.10.0", {"start": v(2882.67, -350) * mm, "end": v(3036.67, -350) * mm});
            skLineSegment(sketch, "E8.31.10.1", {"start": v(3036.67, -350) * mm, "end": v(3036.67, -504) * mm});
            skLineSegment(sketch, "E8.31.10.2", {"start": v(2882.67, -504) * mm, "end": v(3036.67, -504) * mm});
            skLineSegment(sketch, "E8.31.10.3", {"start": v(2882.67, -350) * mm, "end": v(2882.67, -504) * mm});
            skLineSegment(sketch, "E8.31.11.0", {"start": v(2882.67, -506) * mm, "end": v(3036.67, -506) * mm});
            skLineSegment(sketch, "E8.31.11.1", {"start": v(3036.67, -506) * mm, "end": v(3036.67, -660) * mm});
            skLineSegment(sketch, "E8.31.11.2", {"start": v(2882.67, -660) * mm, "end": v(3036.67, -660) * mm});
            skLineSegment(sketch, "E8.31.11.3", {"start": v(2882.67, -506) * mm, "end": v(2882.67, -660) * mm});
            skLineSegment(sketch, "E8.31.12.0", {"start": v(2882.67, -662) * mm, "end": v(3036.67, -662) * mm});
            skLineSegment(sketch, "E8.31.12.1", {"start": v(3036.67, -662) * mm, "end": v(3036.67, -816) * mm});
            skLineSegment(sketch, "E8.31.12.2", {"start": v(2882.67, -816) * mm, "end": v(3036.67, -816) * mm});
            skLineSegment(sketch, "E8.31.12.3", {"start": v(2882.67, -662) * mm, "end": v(2882.67, -816) * mm});
            skLineSegment(sketch, "E8.32.0.0", {"start": v(3038.67, 1210) * mm, "end": v(3192.67, 1210) * mm});
            skLineSegment(sketch, "E8.32.0.1", {"start": v(3192.67, 1210) * mm, "end": v(3192.67, 1056) * mm});
            skLineSegment(sketch, "E8.32.0.2", {"start": v(3038.67, 1056) * mm, "end": v(3192.67, 1056) * mm});
            skLineSegment(sketch, "E8.32.0.3", {"start": v(3038.67, 1210) * mm, "end": v(3038.67, 1056) * mm});
            skLineSegment(sketch, "E8.32.1.0", {"start": v(3038.67, 1054) * mm, "end": v(3192.67, 1054) * mm});
            skLineSegment(sketch, "E8.32.1.1", {"start": v(3192.67, 1054) * mm, "end": v(3192.67, 900) * mm});
            skLineSegment(sketch, "E8.32.1.2", {"start": v(3038.67, 900) * mm, "end": v(3192.67, 900) * mm});
            skLineSegment(sketch, "E8.32.1.3", {"start": v(3038.67, 1054) * mm, "end": v(3038.67, 900) * mm});
            skLineSegment(sketch, "E8.32.2.0", {"start": v(3038.67, 898) * mm, "end": v(3192.67, 898) * mm});
            skLineSegment(sketch, "E8.32.2.1", {"start": v(3192.67, 898) * mm, "end": v(3192.67, 744) * mm});
            skLineSegment(sketch, "E8.32.2.2", {"start": v(3038.67, 744) * mm, "end": v(3192.67, 744) * mm});
            skLineSegment(sketch, "E8.32.2.3", {"start": v(3038.67, 898) * mm, "end": v(3038.67, 744) * mm});
            skLineSegment(sketch, "E8.32.3.0", {"start": v(3038.67, 742) * mm, "end": v(3192.67, 742) * mm});
            skLineSegment(sketch, "E8.32.3.1", {"start": v(3192.67, 742) * mm, "end": v(3192.67, 588) * mm});
            skLineSegment(sketch, "E8.32.3.2", {"start": v(3038.67, 588) * mm, "end": v(3192.67, 588) * mm});
            skLineSegment(sketch, "E8.32.3.3", {"start": v(3038.67, 742) * mm, "end": v(3038.67, 588) * mm});
            skLineSegment(sketch, "E8.32.4.0", {"start": v(3038.67, 586) * mm, "end": v(3192.67, 586) * mm});
            skLineSegment(sketch, "E8.32.4.1", {"start": v(3192.67, 586) * mm, "end": v(3192.67, 432) * mm});
            skLineSegment(sketch, "E8.32.4.2", {"start": v(3038.67, 432) * mm, "end": v(3192.67, 432) * mm});
            skLineSegment(sketch, "E8.32.4.3", {"start": v(3038.67, 586) * mm, "end": v(3038.67, 432) * mm});
            skLineSegment(sketch, "E8.32.5.0", {"start": v(3038.67, 430) * mm, "end": v(3192.67, 430) * mm});
            skLineSegment(sketch, "E8.32.5.1", {"start": v(3192.67, 430) * mm, "end": v(3192.67, 276) * mm});
            skLineSegment(sketch, "E8.32.5.2", {"start": v(3038.67, 276) * mm, "end": v(3192.67, 276) * mm});
            skLineSegment(sketch, "E8.32.5.3", {"start": v(3038.67, 430) * mm, "end": v(3038.67, 276) * mm});
            skLineSegment(sketch, "E8.32.6.0", {"start": v(3038.67, 274) * mm, "end": v(3192.67, 274) * mm});
            skLineSegment(sketch, "E8.32.6.1", {"start": v(3192.67, 274) * mm, "end": v(3192.67, 120) * mm});
            skLineSegment(sketch, "E8.32.6.2", {"start": v(3038.67, 120) * mm, "end": v(3192.67, 120) * mm});
            skLineSegment(sketch, "E8.32.6.3", {"start": v(3038.67, 274) * mm, "end": v(3038.67, 120) * mm});
            skLineSegment(sketch, "E8.32.7.0", {"start": v(3038.67, 118) * mm, "end": v(3192.67, 118) * mm});
            skLineSegment(sketch, "E8.32.7.1", {"start": v(3192.67, 118) * mm, "end": v(3192.67, -36) * mm});
            skLineSegment(sketch, "E8.32.7.2", {"start": v(3038.67, -36) * mm, "end": v(3192.67, -36) * mm});
            skLineSegment(sketch, "E8.32.7.3", {"start": v(3038.67, 118) * mm, "end": v(3038.67, -36) * mm});
            skLineSegment(sketch, "E8.32.8.0", {"start": v(3038.67, -38) * mm, "end": v(3192.67, -38) * mm});
            skLineSegment(sketch, "E8.32.8.1", {"start": v(3192.67, -38) * mm, "end": v(3192.67, -192) * mm});
            skLineSegment(sketch, "E8.32.8.2", {"start": v(3038.67, -192) * mm, "end": v(3192.67, -192) * mm});
            skLineSegment(sketch, "E8.32.8.3", {"start": v(3038.67, -38) * mm, "end": v(3038.67, -192) * mm});
            skLineSegment(sketch, "E8.32.9.0", {"start": v(3038.67, -194) * mm, "end": v(3192.67, -194) * mm});
            skLineSegment(sketch, "E8.32.9.1", {"start": v(3192.67, -194) * mm, "end": v(3192.67, -348) * mm});
            skLineSegment(sketch, "E8.32.9.2", {"start": v(3038.67, -348) * mm, "end": v(3192.67, -348) * mm});
            skLineSegment(sketch, "E8.32.9.3", {"start": v(3038.67, -194) * mm, "end": v(3038.67, -348) * mm});
            skLineSegment(sketch, "E8.32.10.0", {"start": v(3038.67, -350) * mm, "end": v(3192.67, -350) * mm});
            skLineSegment(sketch, "E8.32.10.1", {"start": v(3192.67, -350) * mm, "end": v(3192.67, -504) * mm});
            skLineSegment(sketch, "E8.32.10.2", {"start": v(3038.67, -504) * mm, "end": v(3192.67, -504) * mm});
            skLineSegment(sketch, "E8.32.10.3", {"start": v(3038.67, -350) * mm, "end": v(3038.67, -504) * mm});
            skLineSegment(sketch, "E8.32.11.0", {"start": v(3038.67, -506) * mm, "end": v(3192.67, -506) * mm});
            skLineSegment(sketch, "E8.32.11.1", {"start": v(3192.67, -506) * mm, "end": v(3192.67, -660) * mm});
            skLineSegment(sketch, "E8.32.11.2", {"start": v(3038.67, -660) * mm, "end": v(3192.67, -660) * mm});
            skLineSegment(sketch, "E8.32.11.3", {"start": v(3038.67, -506) * mm, "end": v(3038.67, -660) * mm});
            skLineSegment(sketch, "E8.32.12.0", {"start": v(3038.67, -662) * mm, "end": v(3192.67, -662) * mm});
            skLineSegment(sketch, "E8.32.12.1", {"start": v(3192.67, -662) * mm, "end": v(3192.67, -816) * mm});
            skLineSegment(sketch, "E8.32.12.2", {"start": v(3038.67, -816) * mm, "end": v(3192.67, -816) * mm});
            skLineSegment(sketch, "E8.32.12.3", {"start": v(3038.67, -662) * mm, "end": v(3038.67, -816) * mm});
            skLineSegment(sketch, "E8.33.0.0", {"start": v(3194.67, 1210) * mm, "end": v(3348.67, 1210) * mm});
            skLineSegment(sketch, "E8.33.0.1", {"start": v(3348.67, 1210) * mm, "end": v(3348.67, 1056) * mm});
            skLineSegment(sketch, "E8.33.0.2", {"start": v(3194.67, 1056) * mm, "end": v(3348.67, 1056) * mm});
            skLineSegment(sketch, "E8.33.0.3", {"start": v(3194.67, 1210) * mm, "end": v(3194.67, 1056) * mm});
            skLineSegment(sketch, "E8.33.1.0", {"start": v(3194.67, 1054) * mm, "end": v(3348.67, 1054) * mm});
            skLineSegment(sketch, "E8.33.1.1", {"start": v(3348.67, 1054) * mm, "end": v(3348.67, 900) * mm});
            skLineSegment(sketch, "E8.33.1.2", {"start": v(3194.67, 900) * mm, "end": v(3348.67, 900) * mm});
            skLineSegment(sketch, "E8.33.1.3", {"start": v(3194.67, 1054) * mm, "end": v(3194.67, 900) * mm});
            skLineSegment(sketch, "E8.33.2.0", {"start": v(3194.67, 898) * mm, "end": v(3348.67, 898) * mm});
            skLineSegment(sketch, "E8.33.2.1", {"start": v(3348.67, 898) * mm, "end": v(3348.67, 744) * mm});
            skLineSegment(sketch, "E8.33.2.2", {"start": v(3194.67, 744) * mm, "end": v(3348.67, 744) * mm});
            skLineSegment(sketch, "E8.33.2.3", {"start": v(3194.67, 898) * mm, "end": v(3194.67, 744) * mm});
            skLineSegment(sketch, "E8.33.3.0", {"start": v(3194.67, 742) * mm, "end": v(3348.67, 742) * mm});
            skLineSegment(sketch, "E8.33.3.1", {"start": v(3348.67, 742) * mm, "end": v(3348.67, 588) * mm});
            skLineSegment(sketch, "E8.33.3.2", {"start": v(3194.67, 588) * mm, "end": v(3348.67, 588) * mm});
            skLineSegment(sketch, "E8.33.3.3", {"start": v(3194.67, 742) * mm, "end": v(3194.67, 588) * mm});
            skLineSegment(sketch, "E8.33.4.0", {"start": v(3194.67, 586) * mm, "end": v(3348.67, 586) * mm});
            skLineSegment(sketch, "E8.33.4.1", {"start": v(3348.67, 586) * mm, "end": v(3348.67, 432) * mm});
            skLineSegment(sketch, "E8.33.4.2", {"start": v(3194.67, 432) * mm, "end": v(3348.67, 432) * mm});
            skLineSegment(sketch, "E8.33.4.3", {"start": v(3194.67, 586) * mm, "end": v(3194.67, 432) * mm});
            skLineSegment(sketch, "E8.33.5.0", {"start": v(3194.67, 430) * mm, "end": v(3348.67, 430) * mm});
            skLineSegment(sketch, "E8.33.5.1", {"start": v(3348.67, 430) * mm, "end": v(3348.67, 276) * mm});
            skLineSegment(sketch, "E8.33.5.2", {"start": v(3194.67, 276) * mm, "end": v(3348.67, 276) * mm});
            skLineSegment(sketch, "E8.33.5.3", {"start": v(3194.67, 430) * mm, "end": v(3194.67, 276) * mm});
            skLineSegment(sketch, "E8.33.6.0", {"start": v(3194.67, 274) * mm, "end": v(3348.67, 274) * mm});
            skLineSegment(sketch, "E8.33.6.1", {"start": v(3348.67, 274) * mm, "end": v(3348.67, 120) * mm});
            skLineSegment(sketch, "E8.33.6.2", {"start": v(3194.67, 120) * mm, "end": v(3348.67, 120) * mm});
            skLineSegment(sketch, "E8.33.6.3", {"start": v(3194.67, 274) * mm, "end": v(3194.67, 120) * mm});
            skLineSegment(sketch, "E8.33.7.0", {"start": v(3194.67, 118) * mm, "end": v(3348.67, 118) * mm});
            skLineSegment(sketch, "E8.33.7.1", {"start": v(3348.67, 118) * mm, "end": v(3348.67, -36) * mm});
            skLineSegment(sketch, "E8.33.7.2", {"start": v(3194.67, -36) * mm, "end": v(3348.67, -36) * mm});
            skLineSegment(sketch, "E8.33.7.3", {"start": v(3194.67, 118) * mm, "end": v(3194.67, -36) * mm});
            skLineSegment(sketch, "E8.33.8.0", {"start": v(3194.67, -38) * mm, "end": v(3348.67, -38) * mm});
            skLineSegment(sketch, "E8.33.8.1", {"start": v(3348.67, -38) * mm, "end": v(3348.67, -192) * mm});
            skLineSegment(sketch, "E8.33.8.2", {"start": v(3194.67, -192) * mm, "end": v(3348.67, -192) * mm});
            skLineSegment(sketch, "E8.33.8.3", {"start": v(3194.67, -38) * mm, "end": v(3194.67, -192) * mm});
            skLineSegment(sketch, "E8.33.9.0", {"start": v(3194.67, -194) * mm, "end": v(3348.67, -194) * mm});
            skLineSegment(sketch, "E8.33.9.1", {"start": v(3348.67, -194) * mm, "end": v(3348.67, -348) * mm});
            skLineSegment(sketch, "E8.33.9.2", {"start": v(3194.67, -348) * mm, "end": v(3348.67, -348) * mm});
            skLineSegment(sketch, "E8.33.9.3", {"start": v(3194.67, -194) * mm, "end": v(3194.67, -348) * mm});
            skLineSegment(sketch, "E8.33.10.0", {"start": v(3194.67, -350) * mm, "end": v(3348.67, -350) * mm});
            skLineSegment(sketch, "E8.33.10.1", {"start": v(3348.67, -350) * mm, "end": v(3348.67, -504) * mm});
            skLineSegment(sketch, "E8.33.10.2", {"start": v(3194.67, -504) * mm, "end": v(3348.67, -504) * mm});
            skLineSegment(sketch, "E8.33.10.3", {"start": v(3194.67, -350) * mm, "end": v(3194.67, -504) * mm});
            skLineSegment(sketch, "E8.33.11.0", {"start": v(3194.67, -506) * mm, "end": v(3348.67, -506) * mm});
            skLineSegment(sketch, "E8.33.11.1", {"start": v(3348.67, -506) * mm, "end": v(3348.67, -660) * mm});
            skLineSegment(sketch, "E8.33.11.2", {"start": v(3194.67, -660) * mm, "end": v(3348.67, -660) * mm});
            skLineSegment(sketch, "E8.33.11.3", {"start": v(3194.67, -506) * mm, "end": v(3194.67, -660) * mm});
            skLineSegment(sketch, "E8.33.12.0", {"start": v(3194.67, -662) * mm, "end": v(3348.67, -662) * mm});
            skLineSegment(sketch, "E8.33.12.1", {"start": v(3348.67, -662) * mm, "end": v(3348.67, -816) * mm});
            skLineSegment(sketch, "E8.33.12.2", {"start": v(3194.67, -816) * mm, "end": v(3348.67, -816) * mm});
            skLineSegment(sketch, "E8.33.12.3", {"start": v(3194.67, -662) * mm, "end": v(3194.67, -816) * mm});
            skLineSegment(sketch, "E8.34.0.0", {"start": v(3350.67, 1210) * mm, "end": v(3504.67, 1210) * mm});
            skLineSegment(sketch, "E8.34.0.1", {"start": v(3504.67, 1210) * mm, "end": v(3504.67, 1056) * mm});
            skLineSegment(sketch, "E8.34.0.2", {"start": v(3350.67, 1056) * mm, "end": v(3504.67, 1056) * mm});
            skLineSegment(sketch, "E8.34.0.3", {"start": v(3350.67, 1210) * mm, "end": v(3350.67, 1056) * mm});
            skLineSegment(sketch, "E8.34.1.0", {"start": v(3350.67, 1054) * mm, "end": v(3504.67, 1054) * mm});
            skLineSegment(sketch, "E8.34.1.1", {"start": v(3504.67, 1054) * mm, "end": v(3504.67, 900) * mm});
            skLineSegment(sketch, "E8.34.1.2", {"start": v(3350.67, 900) * mm, "end": v(3504.67, 900) * mm});
            skLineSegment(sketch, "E8.34.1.3", {"start": v(3350.67, 1054) * mm, "end": v(3350.67, 900) * mm});
            skLineSegment(sketch, "E8.34.2.0", {"start": v(3350.67, 898) * mm, "end": v(3504.67, 898) * mm});
            skLineSegment(sketch, "E8.34.2.1", {"start": v(3504.67, 898) * mm, "end": v(3504.67, 744) * mm});
            skLineSegment(sketch, "E8.34.2.2", {"start": v(3350.67, 744) * mm, "end": v(3504.67, 744) * mm});
            skLineSegment(sketch, "E8.34.2.3", {"start": v(3350.67, 898) * mm, "end": v(3350.67, 744) * mm});
            skLineSegment(sketch, "E8.34.3.0", {"start": v(3350.67, 742) * mm, "end": v(3504.67, 742) * mm});
            skLineSegment(sketch, "E8.34.3.1", {"start": v(3504.67, 742) * mm, "end": v(3504.67, 588) * mm});
            skLineSegment(sketch, "E8.34.3.2", {"start": v(3350.67, 588) * mm, "end": v(3504.67, 588) * mm});
            skLineSegment(sketch, "E8.34.3.3", {"start": v(3350.67, 742) * mm, "end": v(3350.67, 588) * mm});
            skLineSegment(sketch, "E8.34.4.0", {"start": v(3350.67, 586) * mm, "end": v(3504.67, 586) * mm});
            skLineSegment(sketch, "E8.34.4.1", {"start": v(3504.67, 586) * mm, "end": v(3504.67, 432) * mm});
            skLineSegment(sketch, "E8.34.4.2", {"start": v(3350.67, 432) * mm, "end": v(3504.67, 432) * mm});
            skLineSegment(sketch, "E8.34.4.3", {"start": v(3350.67, 586) * mm, "end": v(3350.67, 432) * mm});
            skLineSegment(sketch, "E8.34.5.0", {"start": v(3350.67, 430) * mm, "end": v(3504.67, 430) * mm});
            skLineSegment(sketch, "E8.34.5.1", {"start": v(3504.67, 430) * mm, "end": v(3504.67, 276) * mm});
            skLineSegment(sketch, "E8.34.5.2", {"start": v(3350.67, 276) * mm, "end": v(3504.67, 276) * mm});
            skLineSegment(sketch, "E8.34.5.3", {"start": v(3350.67, 430) * mm, "end": v(3350.67, 276) * mm});
            skLineSegment(sketch, "E8.34.6.0", {"start": v(3350.67, 274) * mm, "end": v(3504.67, 274) * mm});
            skLineSegment(sketch, "E8.34.6.1", {"start": v(3504.67, 274) * mm, "end": v(3504.67, 120) * mm});
            skLineSegment(sketch, "E8.34.6.2", {"start": v(3350.67, 120) * mm, "end": v(3504.67, 120) * mm});
            skLineSegment(sketch, "E8.34.6.3", {"start": v(3350.67, 274) * mm, "end": v(3350.67, 120) * mm});
            skLineSegment(sketch, "E8.34.7.0", {"start": v(3350.67, 118) * mm, "end": v(3504.67, 118) * mm});
            skLineSegment(sketch, "E8.34.7.1", {"start": v(3504.67, 118) * mm, "end": v(3504.67, -36) * mm});
            skLineSegment(sketch, "E8.34.7.2", {"start": v(3350.67, -36) * mm, "end": v(3504.67, -36) * mm});
            skLineSegment(sketch, "E8.34.7.3", {"start": v(3350.67, 118) * mm, "end": v(3350.67, -36) * mm});
            skLineSegment(sketch, "E8.34.8.0", {"start": v(3350.67, -38) * mm, "end": v(3504.67, -38) * mm});
            skLineSegment(sketch, "E8.34.8.1", {"start": v(3504.67, -38) * mm, "end": v(3504.67, -192) * mm});
            skLineSegment(sketch, "E8.34.8.2", {"start": v(3350.67, -192) * mm, "end": v(3504.67, -192) * mm});
            skLineSegment(sketch, "E8.34.8.3", {"start": v(3350.67, -38) * mm, "end": v(3350.67, -192) * mm});
            skLineSegment(sketch, "E8.34.9.0", {"start": v(3350.67, -194) * mm, "end": v(3504.67, -194) * mm});
            skLineSegment(sketch, "E8.34.9.1", {"start": v(3504.67, -194) * mm, "end": v(3504.67, -348) * mm});
            skLineSegment(sketch, "E8.34.9.2", {"start": v(3350.67, -348) * mm, "end": v(3504.67, -348) * mm});
            skLineSegment(sketch, "E8.34.9.3", {"start": v(3350.67, -194) * mm, "end": v(3350.67, -348) * mm});
            skLineSegment(sketch, "E8.34.10.0", {"start": v(3350.67, -350) * mm, "end": v(3504.67, -350) * mm});
            skLineSegment(sketch, "E8.34.10.1", {"start": v(3504.67, -350) * mm, "end": v(3504.67, -504) * mm});
            skLineSegment(sketch, "E8.34.10.2", {"start": v(3350.67, -504) * mm, "end": v(3504.67, -504) * mm});
            skLineSegment(sketch, "E8.34.10.3", {"start": v(3350.67, -350) * mm, "end": v(3350.67, -504) * mm});
            skLineSegment(sketch, "E8.34.11.0", {"start": v(3350.67, -506) * mm, "end": v(3504.67, -506) * mm});
            skLineSegment(sketch, "E8.34.11.1", {"start": v(3504.67, -506) * mm, "end": v(3504.67, -660) * mm});
            skLineSegment(sketch, "E8.34.11.2", {"start": v(3350.67, -660) * mm, "end": v(3504.67, -660) * mm});
            skLineSegment(sketch, "E8.34.11.3", {"start": v(3350.67, -506) * mm, "end": v(3350.67, -660) * mm});
            skLineSegment(sketch, "E8.34.12.0", {"start": v(3350.67, -662) * mm, "end": v(3504.67, -662) * mm});
            skLineSegment(sketch, "E8.34.12.1", {"start": v(3504.67, -662) * mm, "end": v(3504.67, -816) * mm});
            skLineSegment(sketch, "E8.34.12.2", {"start": v(3350.67, -816) * mm, "end": v(3504.67, -816) * mm});
            skLineSegment(sketch, "E8.34.12.3", {"start": v(3350.67, -662) * mm, "end": v(3350.67, -816) * mm});
            skLineSegment(sketch, "E8.35.0.0", {"start": v(3506.67, 1210) * mm, "end": v(3660.67, 1210) * mm});
            skLineSegment(sketch, "E8.35.0.1", {"start": v(3660.67, 1210) * mm, "end": v(3660.67, 1056) * mm});
            skLineSegment(sketch, "E8.35.0.2", {"start": v(3506.67, 1056) * mm, "end": v(3660.67, 1056) * mm});
            skLineSegment(sketch, "E8.35.0.3", {"start": v(3506.67, 1210) * mm, "end": v(3506.67, 1056) * mm});
            skLineSegment(sketch, "E8.35.1.0", {"start": v(3506.67, 1054) * mm, "end": v(3660.67, 1054) * mm});
            skLineSegment(sketch, "E8.35.1.1", {"start": v(3660.67, 1054) * mm, "end": v(3660.67, 900) * mm});
            skLineSegment(sketch, "E8.35.1.2", {"start": v(3506.67, 900) * mm, "end": v(3660.67, 900) * mm});
            skLineSegment(sketch, "E8.35.1.3", {"start": v(3506.67, 1054) * mm, "end": v(3506.67, 900) * mm});
            skLineSegment(sketch, "E8.35.2.0", {"start": v(3506.67, 898) * mm, "end": v(3660.67, 898) * mm});
            skLineSegment(sketch, "E8.35.2.1", {"start": v(3660.67, 898) * mm, "end": v(3660.67, 744) * mm});
            skLineSegment(sketch, "E8.35.2.2", {"start": v(3506.67, 744) * mm, "end": v(3660.67, 744) * mm});
            skLineSegment(sketch, "E8.35.2.3", {"start": v(3506.67, 898) * mm, "end": v(3506.67, 744) * mm});
            skLineSegment(sketch, "E8.35.3.0", {"start": v(3506.67, 742) * mm, "end": v(3660.67, 742) * mm});
            skLineSegment(sketch, "E8.35.3.1", {"start": v(3660.67, 742) * mm, "end": v(3660.67, 588) * mm});
            skLineSegment(sketch, "E8.35.3.2", {"start": v(3506.67, 588) * mm, "end": v(3660.67, 588) * mm});
            skLineSegment(sketch, "E8.35.3.3", {"start": v(3506.67, 742) * mm, "end": v(3506.67, 588) * mm});
            skLineSegment(sketch, "E8.35.4.0", {"start": v(3506.67, 586) * mm, "end": v(3660.67, 586) * mm});
            skLineSegment(sketch, "E8.35.4.1", {"start": v(3660.67, 586) * mm, "end": v(3660.67, 432) * mm});
            skLineSegment(sketch, "E8.35.4.2", {"start": v(3506.67, 432) * mm, "end": v(3660.67, 432) * mm});
            skLineSegment(sketch, "E8.35.4.3", {"start": v(3506.67, 586) * mm, "end": v(3506.67, 432) * mm});
            skLineSegment(sketch, "E8.35.5.0", {"start": v(3506.67, 430) * mm, "end": v(3660.67, 430) * mm});
            skLineSegment(sketch, "E8.35.5.1", {"start": v(3660.67, 430) * mm, "end": v(3660.67, 276) * mm});
            skLineSegment(sketch, "E8.35.5.2", {"start": v(3506.67, 276) * mm, "end": v(3660.67, 276) * mm});
            skLineSegment(sketch, "E8.35.5.3", {"start": v(3506.67, 430) * mm, "end": v(3506.67, 276) * mm});
            skLineSegment(sketch, "E8.35.6.0", {"start": v(3506.67, 274) * mm, "end": v(3660.67, 274) * mm});
            skLineSegment(sketch, "E8.35.6.1", {"start": v(3660.67, 274) * mm, "end": v(3660.67, 120) * mm});
            skLineSegment(sketch, "E8.35.6.2", {"start": v(3506.67, 120) * mm, "end": v(3660.67, 120) * mm});
            skLineSegment(sketch, "E8.35.6.3", {"start": v(3506.67, 274) * mm, "end": v(3506.67, 120) * mm});
            skLineSegment(sketch, "E8.35.7.0", {"start": v(3506.67, 118) * mm, "end": v(3660.67, 118) * mm});
            skLineSegment(sketch, "E8.35.7.1", {"start": v(3660.67, 118) * mm, "end": v(3660.67, -36) * mm});
            skLineSegment(sketch, "E8.35.7.2", {"start": v(3506.67, -36) * mm, "end": v(3660.67, -36) * mm});
            skLineSegment(sketch, "E8.35.7.3", {"start": v(3506.67, 118) * mm, "end": v(3506.67, -36) * mm});
            skLineSegment(sketch, "E8.35.8.0", {"start": v(3506.67, -38) * mm, "end": v(3660.67, -38) * mm});
            skLineSegment(sketch, "E8.35.8.1", {"start": v(3660.67, -38) * mm, "end": v(3660.67, -192) * mm});
            skLineSegment(sketch, "E8.35.8.2", {"start": v(3506.67, -192) * mm, "end": v(3660.67, -192) * mm});
            skLineSegment(sketch, "E8.35.8.3", {"start": v(3506.67, -38) * mm, "end": v(3506.67, -192) * mm});
            skLineSegment(sketch, "E8.35.9.0", {"start": v(3506.67, -194) * mm, "end": v(3660.67, -194) * mm});
            skLineSegment(sketch, "E8.35.9.1", {"start": v(3660.67, -194) * mm, "end": v(3660.67, -348) * mm});
            skLineSegment(sketch, "E8.35.9.2", {"start": v(3506.67, -348) * mm, "end": v(3660.67, -348) * mm});
            skLineSegment(sketch, "E8.35.9.3", {"start": v(3506.67, -194) * mm, "end": v(3506.67, -348) * mm});
            skLineSegment(sketch, "E8.35.10.0", {"start": v(3506.67, -350) * mm, "end": v(3660.67, -350) * mm});
            skLineSegment(sketch, "E8.35.10.1", {"start": v(3660.67, -350) * mm, "end": v(3660.67, -504) * mm});
            skLineSegment(sketch, "E8.35.10.2", {"start": v(3506.67, -504) * mm, "end": v(3660.67, -504) * mm});
            skLineSegment(sketch, "E8.35.10.3", {"start": v(3506.67, -350) * mm, "end": v(3506.67, -504) * mm});
            skLineSegment(sketch, "E8.35.11.0", {"start": v(3506.67, -506) * mm, "end": v(3660.67, -506) * mm});
            skLineSegment(sketch, "E8.35.11.1", {"start": v(3660.67, -506) * mm, "end": v(3660.67, -660) * mm});
            skLineSegment(sketch, "E8.35.11.2", {"start": v(3506.67, -660) * mm, "end": v(3660.67, -660) * mm});
            skLineSegment(sketch, "E8.35.11.3", {"start": v(3506.67, -506) * mm, "end": v(3506.67, -660) * mm});
            skLineSegment(sketch, "E8.35.12.0", {"start": v(3506.67, -662) * mm, "end": v(3660.67, -662) * mm});
            skLineSegment(sketch, "E8.35.12.1", {"start": v(3660.67, -662) * mm, "end": v(3660.67, -816) * mm});
            skLineSegment(sketch, "E8.35.12.2", {"start": v(3506.67, -816) * mm, "end": v(3660.67, -816) * mm});
            skLineSegment(sketch, "E8.35.12.3", {"start": v(3506.67, -662) * mm, "end": v(3506.67, -816) * mm});
            skLineSegment(sketch, "E8.36.0.0", {"start": v(3662.67, 1210) * mm, "end": v(3816.67, 1210) * mm});
            skLineSegment(sketch, "E8.36.0.1", {"start": v(3816.67, 1210) * mm, "end": v(3816.67, 1056) * mm});
            skLineSegment(sketch, "E8.36.0.2", {"start": v(3662.67, 1056) * mm, "end": v(3816.67, 1056) * mm});
            skLineSegment(sketch, "E8.36.0.3", {"start": v(3662.67, 1210) * mm, "end": v(3662.67, 1056) * mm});
            skLineSegment(sketch, "E8.36.1.0", {"start": v(3662.67, 1054) * mm, "end": v(3816.67, 1054) * mm});
            skLineSegment(sketch, "E8.36.1.1", {"start": v(3816.67, 1054) * mm, "end": v(3816.67, 900) * mm});
            skLineSegment(sketch, "E8.36.1.2", {"start": v(3662.67, 900) * mm, "end": v(3816.67, 900) * mm});
            skLineSegment(sketch, "E8.36.1.3", {"start": v(3662.67, 1054) * mm, "end": v(3662.67, 900) * mm});
            skLineSegment(sketch, "E8.36.2.0", {"start": v(3662.67, 898) * mm, "end": v(3816.67, 898) * mm});
            skLineSegment(sketch, "E8.36.2.1", {"start": v(3816.67, 898) * mm, "end": v(3816.67, 744) * mm});
            skLineSegment(sketch, "E8.36.2.2", {"start": v(3662.67, 744) * mm, "end": v(3816.67, 744) * mm});
            skLineSegment(sketch, "E8.36.2.3", {"start": v(3662.67, 898) * mm, "end": v(3662.67, 744) * mm});
            skLineSegment(sketch, "E8.36.3.0", {"start": v(3662.67, 742) * mm, "end": v(3816.67, 742) * mm});
            skLineSegment(sketch, "E8.36.3.1", {"start": v(3816.67, 742) * mm, "end": v(3816.67, 588) * mm});
            skLineSegment(sketch, "E8.36.3.2", {"start": v(3662.67, 588) * mm, "end": v(3816.67, 588) * mm});
            skLineSegment(sketch, "E8.36.3.3", {"start": v(3662.67, 742) * mm, "end": v(3662.67, 588) * mm});
            skLineSegment(sketch, "E8.36.4.0", {"start": v(3662.67, 586) * mm, "end": v(3816.67, 586) * mm});
            skLineSegment(sketch, "E8.36.4.1", {"start": v(3816.67, 586) * mm, "end": v(3816.67, 432) * mm});
            skLineSegment(sketch, "E8.36.4.2", {"start": v(3662.67, 432) * mm, "end": v(3816.67, 432) * mm});
            skLineSegment(sketch, "E8.36.4.3", {"start": v(3662.67, 586) * mm, "end": v(3662.67, 432) * mm});
            skLineSegment(sketch, "E8.36.5.0", {"start": v(3662.67, 430) * mm, "end": v(3816.67, 430) * mm});
            skLineSegment(sketch, "E8.36.5.1", {"start": v(3816.67, 430) * mm, "end": v(3816.67, 276) * mm});
            skLineSegment(sketch, "E8.36.5.2", {"start": v(3662.67, 276) * mm, "end": v(3816.67, 276) * mm});
            skLineSegment(sketch, "E8.36.5.3", {"start": v(3662.67, 430) * mm, "end": v(3662.67, 276) * mm});
            skLineSegment(sketch, "E8.36.6.0", {"start": v(3662.67, 274) * mm, "end": v(3816.67, 274) * mm});
            skLineSegment(sketch, "E8.36.6.1", {"start": v(3816.67, 274) * mm, "end": v(3816.67, 120) * mm});
            skLineSegment(sketch, "E8.36.6.2", {"start": v(3662.67, 120) * mm, "end": v(3816.67, 120) * mm});
            skLineSegment(sketch, "E8.36.6.3", {"start": v(3662.67, 274) * mm, "end": v(3662.67, 120) * mm});
            skLineSegment(sketch, "E8.36.7.0", {"start": v(3662.67, 118) * mm, "end": v(3816.67, 118) * mm});
            skLineSegment(sketch, "E8.36.7.1", {"start": v(3816.67, 118) * mm, "end": v(3816.67, -36) * mm});
            skLineSegment(sketch, "E8.36.7.2", {"start": v(3662.67, -36) * mm, "end": v(3816.67, -36) * mm});
            skLineSegment(sketch, "E8.36.7.3", {"start": v(3662.67, 118) * mm, "end": v(3662.67, -36) * mm});
            skLineSegment(sketch, "E8.36.8.0", {"start": v(3662.67, -38) * mm, "end": v(3816.67, -38) * mm});
            skLineSegment(sketch, "E8.36.8.1", {"start": v(3816.67, -38) * mm, "end": v(3816.67, -192) * mm});
            skLineSegment(sketch, "E8.36.8.2", {"start": v(3662.67, -192) * mm, "end": v(3816.67, -192) * mm});
            skLineSegment(sketch, "E8.36.8.3", {"start": v(3662.67, -38) * mm, "end": v(3662.67, -192) * mm});
            skLineSegment(sketch, "E8.36.9.0", {"start": v(3662.67, -194) * mm, "end": v(3816.67, -194) * mm});
            skLineSegment(sketch, "E8.36.9.1", {"start": v(3816.67, -194) * mm, "end": v(3816.67, -348) * mm});
            skLineSegment(sketch, "E8.36.9.2", {"start": v(3662.67, -348) * mm, "end": v(3816.67, -348) * mm});
            skLineSegment(sketch, "E8.36.9.3", {"start": v(3662.67, -194) * mm, "end": v(3662.67, -348) * mm});
            skLineSegment(sketch, "E8.36.10.0", {"start": v(3662.67, -350) * mm, "end": v(3816.67, -350) * mm});
            skLineSegment(sketch, "E8.36.10.1", {"start": v(3816.67, -350) * mm, "end": v(3816.67, -504) * mm});
            skLineSegment(sketch, "E8.36.10.2", {"start": v(3662.67, -504) * mm, "end": v(3816.67, -504) * mm});
            skLineSegment(sketch, "E8.36.10.3", {"start": v(3662.67, -350) * mm, "end": v(3662.67, -504) * mm});
            skLineSegment(sketch, "E8.36.11.0", {"start": v(3662.67, -506) * mm, "end": v(3816.67, -506) * mm});
            skLineSegment(sketch, "E8.36.11.1", {"start": v(3816.67, -506) * mm, "end": v(3816.67, -660) * mm});
            skLineSegment(sketch, "E8.36.11.2", {"start": v(3662.67, -660) * mm, "end": v(3816.67, -660) * mm});
            skLineSegment(sketch, "E8.36.11.3", {"start": v(3662.67, -506) * mm, "end": v(3662.67, -660) * mm});
            skLineSegment(sketch, "E8.36.12.0", {"start": v(3662.67, -662) * mm, "end": v(3816.67, -662) * mm});
            skLineSegment(sketch, "E8.36.12.1", {"start": v(3816.67, -662) * mm, "end": v(3816.67, -816) * mm});
            skLineSegment(sketch, "E8.36.12.2", {"start": v(3662.67, -816) * mm, "end": v(3816.67, -816) * mm});
            skLineSegment(sketch, "E8.36.12.3", {"start": v(3662.67, -662) * mm, "end": v(3662.67, -816) * mm});
            skLineSegment(sketch, "E8.direction1", {"start": v(-1953.33, 1056) * mm, "end": v(-1797.33, 1056) * mm, "construction": true});
            skLineSegment(sketch, "E8.direction2", {"start": v(-1953.33, 1056) * mm, "end": v(-1953.33, 900) * mm, "construction": true});
            skSolve(sketch);
        }
        {
            var Q0;
            Q0=sQuery(id+"F0.wireOp",EDGE,"E0.bottom");
            cPlane(context, id + "F2", {"entities" : qUnion([Q0]), "cplaneType" : CPlaneType.LINE_ANGLE, "offset" : 25 * mm, "angle" : 90 * degree, "width" : 150 * mm, "height" : 150 * mm});
        }
        {
            var Q0;
            Q0=qCreatedBy(id+"F2.planeOp",FACE);
            var sketch = newSketch(context, id + "F3", { "sketchPlane" : qUnion([Q0])});
            skLineSegment(sketch, "E9", {"start": v(-1953.33, 0) * mm, "end": v(-1953.33, 80) * mm});
            skLineSegment(sketch, "E10", {"start": v(-1953.33, 80) * mm, "end": v(-283.34, 84.29) * mm});
            skLineSegment(sketch, "E11", {"start": v(-283.34, 84.29) * mm, "end": v(-275.26, 37.99) * mm});
            skLineSegment(sketch, "E12", {"start": v(-275.26, 37.99) * mm, "end": v(-35.33, 32) * mm});
            skLineSegment(sketch, "E13", {"start": v(-35.33, 32) * mm, "end": v(-35.33, 92) * mm});
            skLineSegment(sketch, "E14", {"start": v(-35.33, 92) * mm, "end": v(46.67, 92) * mm});
            skLineSegment(sketch, "E15", {"start": v(907.25, 0) * mm, "end": v(907.25, 325) * mm, "construction": true});
            skLineSegment(sketch, "E16", {"start": v(46.67, 0) * mm, "end": v(46.67, 92) * mm});
            skLineSegment(sketch, "E17", {"start": v(-275.26, 37.99) * mm, "end": v(-276.2, 0) * mm, "construction": true});
            skLineSegment(sketch, "E18", {"start": v(-35.33, 32) * mm, "end": v(-36.13, 0) * mm, "construction": true});
            skLineSegment(sketch, "E19", {"start": v(-1953.33, 0) * mm, "end": v(-276.2, 0) * mm});
            skLineSegment(sketch, "E20", {"start": v(-36.13, 0) * mm, "end": v(46.67, 0) * mm});
            skLineSegment(sketch, "E21", {"start": v(-276.2, 0) * mm, "end": v(-36.13, 0) * mm});
            skPoint(sketch, "E22", {"position": v(46.67, 92) * mm});
            skLineSegment(sketch, "E23", {"start": v(46.67, 92) * mm, "end": v(46.67, 320) * mm, "construction": true});
            skLineSegment(sketch, "E24.bottom", {"start": v(74.67, 0) * mm, "end": v(852.67, 0) * mm});
            skLineSegment(sketch, "E24.left", {"start": v(74.67, 0) * mm, "end": v(98.78, 41.77) * mm});
            skLineSegment(sketch, "E24.right", {"start": v(852.67, 0) * mm, "end": v(876.78, 41.77) * mm});
            skPoint(sketch, "E25", {"position": v(86.73, 20.89) * mm});
            skLineSegment(sketch, "E26", {"start": v(86.73, 20.89) * mm, "end": v(136.73, 20.89) * mm, "construction": true});
            skLineSegment(sketch, "E27", {"start": v(401.16, 26.37) * mm, "end": v(386.86, 0) * mm, "construction": true});
            skLineSegment(sketch, "E28", {"start": v(136.73, 20.89) * mm, "end": v(864.73, 20.89) * mm, "construction": true});
            skCircle(sketch, "E29", {"center": v(136.73, 20.89) * mm, "radius": 43.31 * mm, "construction": true});
            skLineSegment(sketch, "E30", {"start": v(98.78, 41.77) * mm, "end": v(876.78, 41.77) * mm});
            skLineSegment(sketch, "E31.bottom", {"start": v(47.67, 92.5) * mm, "end": v(66.17, 92.5) * mm});
            skLineSegment(sketch, "E31.top", {"start": v(47.67, 112) * mm, "end": v(66.17, 112) * mm});
            skLineSegment(sketch, "E31.left", {"start": v(47.17, 93) * mm, "end": v(47.17, 111.5) * mm});
            skLineSegment(sketch, "E31.right", {"start": v(66.67, 93) * mm, "end": v(66.67, 111.5) * mm});
            skPoint(sketch, "E32.visualSharp", {"position": v(66.67, 112) * mm});
            skArc(sketch, "E32.filletArc", {"start": v(66.67, 111.5) * mm, "mid": v(66.52, 111.84) * mm, "end": v(66.17, 112) * mm});
            skPoint(sketch, "E33.visualSharp", {"position": v(47.17, 112) * mm});
            skArc(sketch, "E33.filletArc", {"start": v(47.67, 112) * mm, "mid": v(47.31, 111.84) * mm, "end": v(47.17, 111.5) * mm});
            skPoint(sketch, "E34.visualSharp", {"position": v(47.17, 92.5) * mm});
            skArc(sketch, "E34.filletArc", {"start": v(47.17, 93) * mm, "mid": v(47.31, 92.64) * mm, "end": v(47.67, 92.5) * mm});
            skPoint(sketch, "E35.visualSharp", {"position": v(66.67, 92.5) * mm});
            skArc(sketch, "E35.filletArc", {"start": v(66.17, 92.5) * mm, "mid": v(66.52, 92.64) * mm, "end": v(66.67, 93) * mm});
            skArc(sketch, "E36.0", {"start": v(47.67, 112.5) * mm, "mid": v(46.96, 112.2) * mm, "end": v(46.67, 111.5) * mm});
            skLineSegment(sketch, "E36.1", {"start": v(46.67, 93) * mm, "end": v(46.67, 111.5) * mm});
            skLineSegment(sketch, "E36.2", {"start": v(47.67, 112.5) * mm, "end": v(66.17, 112.5) * mm});
            skArc(sketch, "E36.3", {"start": v(46.67, 93) * mm, "mid": v(46.96, 92.28) * mm, "end": v(47.67, 92) * mm});
            skArc(sketch, "E36.4", {"start": v(67.17, 111.5) * mm, "mid": v(66.87, 112.2) * mm, "end": v(66.17, 112.5) * mm});
            skLineSegment(sketch, "E36.5", {"start": v(67.17, 93) * mm, "end": v(67.17, 111.5) * mm});
            skArc(sketch, "E36.6", {"start": v(66.17, 92) * mm, "mid": v(66.87, 92.28) * mm, "end": v(67.17, 93) * mm});
            skLineSegment(sketch, "E36.7", {"start": v(47.67, 92) * mm, "end": v(66.17, 92) * mm});
            skLineSegment(sketch, "E37", {"start": v(46.67, 92) * mm, "end": v(907.25, 92) * mm, "construction": true});
            skSolve(sketch);
        }
        {
            var Q0;
            Q0=sQuery(id+"F3.wireOp",VERTEX,"E16.end");
            var Q1;
            Q1=sQuery(id+"F0.wireOp",VERTEX,"E0.bottom.end");
            var Q2;
            Q2=sQuery(id+"F0.wireOp",VERTEX,"E0.top.end");
            cPlane(context, id + "F4", {"entities" : qUnion([Q0, Q1, Q2]), "cplaneType" : CPlaneType.THREE_POINT, "offset" : 25 * mm, "width" : 150 * mm, "height" : 150 * mm});
        }
        {
            var Q0;
            Q0=makeQuery(id+"F3.imprint","IMPRINT",FACE,{"disambiguationData":[TD([[makeQuery(id+"F3.imprint","IMPRINT",EDGE,{"derivedFrom":sQuery(id+"F3.wireOp",EDGE,"E9")}),-1.0]])]});
            var Q1;
            Q1=sQuery(id+"F0.wireOp",VERTEX,"E0.top.end");
            extrude(context, id + "F5", {"entities" : qUnion([Q0]), "endBound" : BoundingType.UP_TO_VERTEX, "oppositeDirection" : true, "depth" : 25 * mm, "endBoundEntityVertex" : qUnion([Q1]), "offsetDistance" : 25 * mm});
        }
    });
